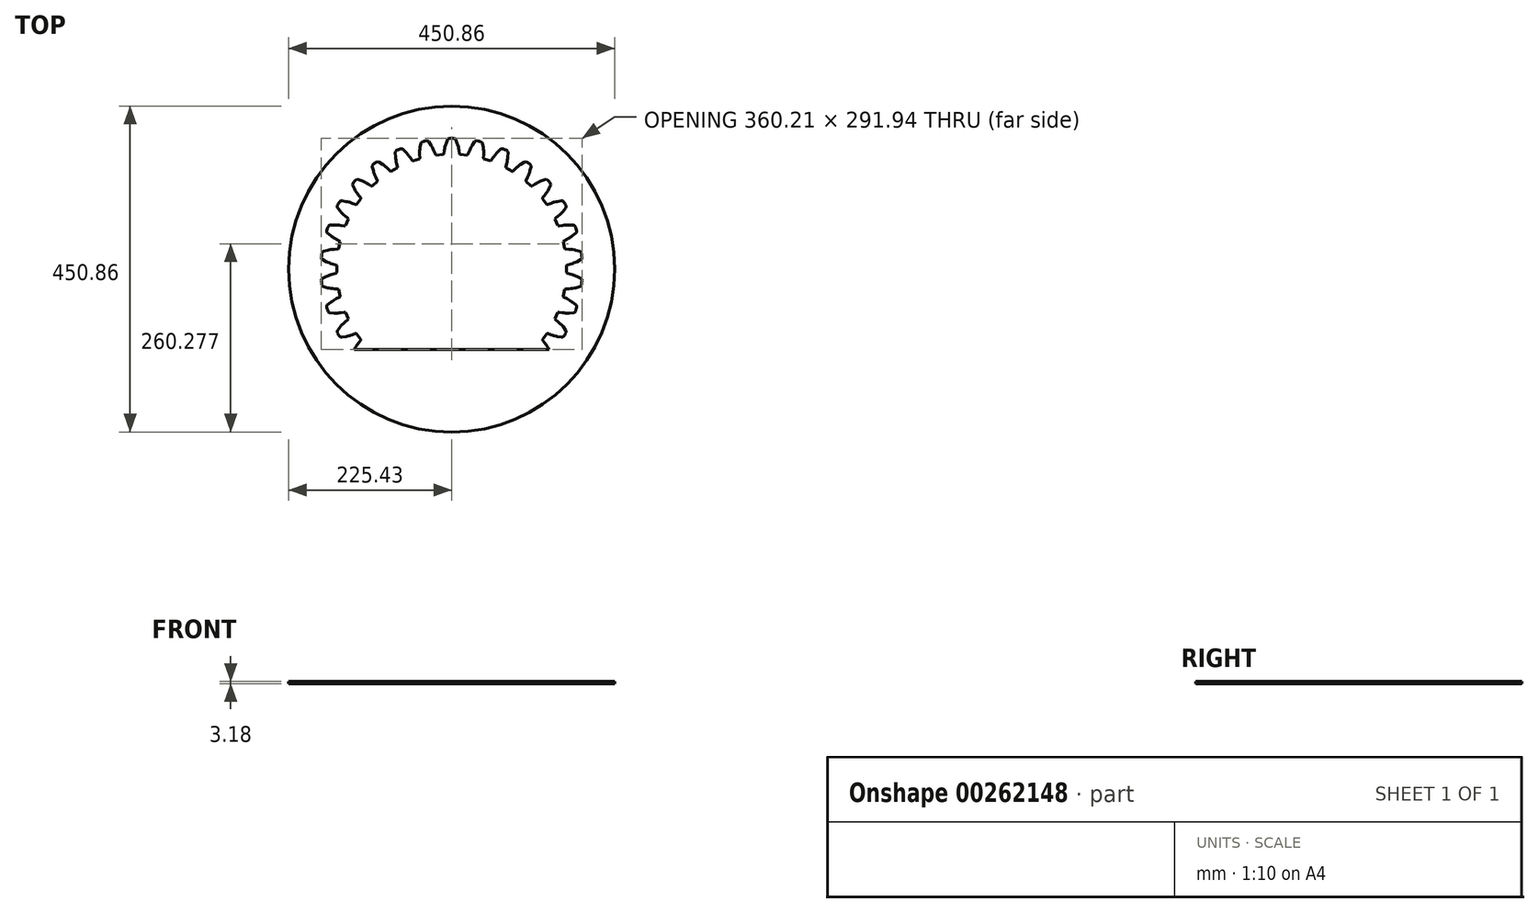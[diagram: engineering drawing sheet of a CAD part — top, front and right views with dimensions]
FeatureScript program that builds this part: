
annotation { "Feature Type Name" : "Feature", "Feature Type Description" : "" }
export const myFeature = defineFeature(function(context is Context, id is Id, definition is map)
    precondition{}
    {
        {
            var Q0;
            Q0=qCreatedBy(makeId("Top.planeOp"),FACE);
            var sketch = newSketch(context, id + "F0", { "sketchPlane" : qUnion([Q0])});
            skLineSegment(sketch, "E0", {"start": v(226.67, 0) * mm, "end": v(221.71, 47.13) * mm});
            skLineSegment(sketch, "E1", {"start": v(221.71, 47.13) * mm, "end": v(207.07, 92.2) * mm});
            skLineSegment(sketch, "E2", {"start": v(207.07, 92.2) * mm, "end": v(183.38, 133.23) * mm});
            skLineSegment(sketch, "E3", {"start": v(183.38, 133.23) * mm, "end": v(151.67, 168.45) * mm});
            skLineSegment(sketch, "E4", {"start": v(151.67, 168.45) * mm, "end": v(113.33, 196.3) * mm});
            skLineSegment(sketch, "E5", {"start": v(113.33, 196.3) * mm, "end": v(70.04, 215.57) * mm});
            skLineSegment(sketch, "E6", {"start": v(70.04, 215.57) * mm, "end": v(23.7, 225.42) * mm});
            skLineSegment(sketch, "E7", {"start": v(23.7, 225.43) * mm, "end": v(-23.7, 225.43) * mm});
            skLineSegment(sketch, "E8", {"start": v(-23.7, 225.43) * mm, "end": v(-70.04, 215.57) * mm});
            skLineSegment(sketch, "E9", {"start": v(-70.04, 215.57) * mm, "end": v(-113.33, 196.3) * mm});
            skLineSegment(sketch, "E10", {"start": v(-113.33, 196.3) * mm, "end": v(-151.67, 168.45) * mm});
            skLineSegment(sketch, "E11", {"start": v(-151.67, 168.45) * mm, "end": v(-183.38, 133.23) * mm});
            skLineSegment(sketch, "E12", {"start": v(-183.38, 133.23) * mm, "end": v(-207.07, 92.2) * mm});
            skLineSegment(sketch, "E13", {"start": v(-207.07, 92.2) * mm, "end": v(-221.71, 47.13) * mm});
            skLineSegment(sketch, "E14", {"start": v(-221.71, 47.13) * mm, "end": v(-226.67, 0) * mm});
            skLineSegment(sketch, "E15", {"start": v(-226.67, 0) * mm, "end": v(-221.71, -47.13) * mm});
            skLineSegment(sketch, "E16", {"start": v(-221.71, -47.13) * mm, "end": v(-207.07, -92.2) * mm});
            skLineSegment(sketch, "E17", {"start": v(-207.07, -92.2) * mm, "end": v(-183.38, -133.23) * mm});
            skLineSegment(sketch, "E18", {"start": v(-183.38, -133.23) * mm, "end": v(-151.67, -168.45) * mm});
            skLineSegment(sketch, "E19", {"start": v(-151.67, -168.45) * mm, "end": v(-113.33, -196.3) * mm});
            skLineSegment(sketch, "E20", {"start": v(-113.33, -196.3) * mm, "end": v(-70.04, -215.57) * mm});
            skLineSegment(sketch, "E21", {"start": v(-70.04, -215.57) * mm, "end": v(-23.7, -225.42) * mm});
            skLineSegment(sketch, "E22", {"start": v(-23.7, -225.43) * mm, "end": v(23.7, -225.43) * mm});
            skLineSegment(sketch, "E23", {"start": v(23.7, -225.43) * mm, "end": v(70.04, -215.57) * mm});
            skLineSegment(sketch, "E24", {"start": v(70.04, -215.57) * mm, "end": v(113.33, -196.3) * mm});
            skLineSegment(sketch, "E25", {"start": v(113.33, -196.3) * mm, "end": v(151.67, -168.45) * mm});
            skLineSegment(sketch, "E26", {"start": v(151.67, -168.45) * mm, "end": v(183.38, -133.23) * mm});
            skLineSegment(sketch, "E27", {"start": v(183.38, -133.23) * mm, "end": v(207.07, -92.2) * mm});
            skLineSegment(sketch, "E28", {"start": v(207.07, -92.2) * mm, "end": v(221.71, -47.13) * mm});
            skLineSegment(sketch, "E29", {"start": v(221.71, -47.13) * mm, "end": v(226.67, 0) * mm});
            skLineSegment(sketch, "E30", {"start": v(-179.94, 17.83) * mm, "end": v(-179.83, 18.9) * mm});
            skLineSegment(sketch, "E31", {"start": v(-179.83, 18.9) * mm, "end": v(-179.72, 19.97) * mm});
            skLineSegment(sketch, "E32", {"start": v(-179.72, 19.97) * mm, "end": v(-179.54, 21.6) * mm});
            skLineSegment(sketch, "E33", {"start": v(-179.54, 21.6) * mm, "end": v(-178.6, 23.6) * mm});
            skLineSegment(sketch, "E34", {"start": v(-178.6, 23.6) * mm, "end": v(-177.2, 24.4) * mm});
            skLineSegment(sketch, "E35", {"start": v(-177.2, 24.4) * mm, "end": v(-171.49, 25.97) * mm});
            skLineSegment(sketch, "E36", {"start": v(-171.49, 25.97) * mm, "end": v(-169.86, 26.35) * mm});
            skLineSegment(sketch, "E37", {"start": v(-169.86, 26.35) * mm, "end": v(-166.94, 26.84) * mm});
            skLineSegment(sketch, "E38", {"start": v(-166.94, 26.84) * mm, "end": v(-166.45, 26.9) * mm});
            skLineSegment(sketch, "E39", {"start": v(-166.45, 26.9) * mm, "end": v(-164.79, 27.1) * mm});
            skLineSegment(sketch, "E40", {"start": v(-164.79, 27.1) * mm, "end": v(-162.13, 27.32) * mm});
            skLineSegment(sketch, "E41", {"start": v(-162.13, 27.32) * mm, "end": v(-157.52, 27.56) * mm});
            skLineSegment(sketch, "E42", {"start": v(-157.52, 27.56) * mm, "end": v(-156.75, 27.92) * mm});
            skLineSegment(sketch, "E43", {"start": v(-156.75, 27.92) * mm, "end": v(-156.27, 28.27) * mm});
            skLineSegment(sketch, "E44", {"start": v(-156.27, 28.27) * mm, "end": v(-154.26, 37.73) * mm});
            skLineSegment(sketch, "E45", {"start": v(-154.26, 37.73) * mm, "end": v(-154.55, 38.25) * mm});
            skLineSegment(sketch, "E46", {"start": v(-154.55, 38.25) * mm, "end": v(-155.1, 38.9) * mm});
            skLineSegment(sketch, "E47", {"start": v(-155.1, 38.9) * mm, "end": v(-159.22, 40.98) * mm});
            skLineSegment(sketch, "E48", {"start": v(-159.22, 40.98) * mm, "end": v(-161.57, 42.26) * mm});
            skLineSegment(sketch, "E49", {"start": v(-161.57, 42.26) * mm, "end": v(-163, 43.12) * mm});
            skLineSegment(sketch, "E50", {"start": v(-163, 43.12) * mm, "end": v(-163.43, 43.38) * mm});
            skLineSegment(sketch, "E51", {"start": v(-163.43, 43.38) * mm, "end": v(-165.9, 45.01) * mm});
            skLineSegment(sketch, "E52", {"start": v(-165.9, 45.01) * mm, "end": v(-167.22, 46.03) * mm});
            skLineSegment(sketch, "E53", {"start": v(-167.22, 46.03) * mm, "end": v(-171.8, 49.77) * mm});
            skLineSegment(sketch, "E54", {"start": v(-171.8, 49.77) * mm, "end": v(-172.76, 51.08) * mm});
            skLineSegment(sketch, "E55", {"start": v(-172.76, 51.08) * mm, "end": v(-172.8, 53.3) * mm});
            skLineSegment(sketch, "E56", {"start": v(-172.8, 53.3) * mm, "end": v(-172.3, 54.85) * mm});
            skLineSegment(sketch, "E57", {"start": v(-172.3, 54.85) * mm, "end": v(-171.97, 55.88) * mm});
            skLineSegment(sketch, "E58", {"start": v(-171.97, 55.88) * mm, "end": v(-171.64, 56.9) * mm});
            skLineSegment(sketch, "E59", {"start": v(-171.64, 56.9) * mm, "end": v(-171.12, 58.45) * mm});
            skLineSegment(sketch, "E60", {"start": v(-171.12, 58.45) * mm, "end": v(-169.79, 60.22) * mm});
            skLineSegment(sketch, "E61", {"start": v(-169.79, 60.22) * mm, "end": v(-168.24, 60.71) * mm});
            skLineSegment(sketch, "E62", {"start": v(-168.24, 60.71) * mm, "end": v(-162.34, 61.06) * mm});
            skLineSegment(sketch, "E63", {"start": v(-162.34, 61.06) * mm, "end": v(-160.67, 61.1) * mm});
            skLineSegment(sketch, "E64", {"start": v(-160.67, 61.1) * mm, "end": v(-157.71, 60.97) * mm});
            skLineSegment(sketch, "E65", {"start": v(-157.71, 60.97) * mm, "end": v(-157.22, 60.93) * mm});
            skLineSegment(sketch, "E66", {"start": v(-157.22, 60.93) * mm, "end": v(-155.55, 60.78) * mm});
            skLineSegment(sketch, "E67", {"start": v(-155.55, 60.78) * mm, "end": v(-152.9, 60.43) * mm});
            skLineSegment(sketch, "E68", {"start": v(-152.9, 60.43) * mm, "end": v(-148.35, 59.7) * mm});
            skLineSegment(sketch, "E69", {"start": v(-148.35, 59.7) * mm, "end": v(-147.52, 59.9) * mm});
            skLineSegment(sketch, "E70", {"start": v(-147.52, 59.9) * mm, "end": v(-146.98, 60.14) * mm});
            skLineSegment(sketch, "E71", {"start": v(-146.98, 60.14) * mm, "end": v(-143.04, 68.98) * mm});
            skLineSegment(sketch, "E72", {"start": v(-143.04, 68.98) * mm, "end": v(-143.22, 69.54) * mm});
            skLineSegment(sketch, "E73", {"start": v(-143.22, 69.54) * mm, "end": v(-143.63, 70.3) * mm});
            skLineSegment(sketch, "E74", {"start": v(-143.63, 70.3) * mm, "end": v(-147.22, 73.19) * mm});
            skLineSegment(sketch, "E75", {"start": v(-147.22, 73.19) * mm, "end": v(-149.25, 74.93) * mm});
            skLineSegment(sketch, "E76", {"start": v(-149.25, 74.93) * mm, "end": v(-150.48, 76.07) * mm});
            skLineSegment(sketch, "E77", {"start": v(-150.48, 76.07) * mm, "end": v(-150.84, 76.4) * mm});
            skLineSegment(sketch, "E78", {"start": v(-150.84, 76.4) * mm, "end": v(-152.91, 78.52) * mm});
            skLineSegment(sketch, "E79", {"start": v(-152.91, 78.52) * mm, "end": v(-154, 79.79) * mm});
            skLineSegment(sketch, "E80", {"start": v(-154, 79.79) * mm, "end": v(-157.7, 84.4) * mm});
            skLineSegment(sketch, "E81", {"start": v(-157.7, 84.4) * mm, "end": v(-158.36, 85.89) * mm});
            skLineSegment(sketch, "E82", {"start": v(-158.36, 85.89) * mm, "end": v(-157.94, 88.06) * mm});
            skLineSegment(sketch, "E83", {"start": v(-157.94, 88.06) * mm, "end": v(-157.13, 89.47) * mm});
            skLineSegment(sketch, "E84", {"start": v(-157.13, 89.47) * mm, "end": v(-156.6, 90.4) * mm});
            skLineSegment(sketch, "E85", {"start": v(-156.6, 90.4) * mm, "end": v(-156.05, 91.34) * mm});
            skLineSegment(sketch, "E86", {"start": v(-156.05, 91.34) * mm, "end": v(-155.23, 92.75) * mm});
            skLineSegment(sketch, "E87", {"start": v(-155.23, 92.75) * mm, "end": v(-153.56, 94.2) * mm});
            skLineSegment(sketch, "E88", {"start": v(-153.56, 94.2) * mm, "end": v(-151.94, 94.37) * mm});
            skLineSegment(sketch, "E89", {"start": v(-151.94, 94.37) * mm, "end": v(-146.1, 93.48) * mm});
            skLineSegment(sketch, "E90", {"start": v(-146.1, 93.48) * mm, "end": v(-144.46, 93.17) * mm});
            skLineSegment(sketch, "E91", {"start": v(-144.46, 93.17) * mm, "end": v(-141.6, 92.43) * mm});
            skLineSegment(sketch, "E92", {"start": v(-141.6, 92.43) * mm, "end": v(-141.11, 92.28) * mm});
            skLineSegment(sketch, "E93", {"start": v(-141.11, 92.28) * mm, "end": v(-139.51, 91.8) * mm});
            skLineSegment(sketch, "E94", {"start": v(-139.51, 91.8) * mm, "end": v(-137, 90.9) * mm});
            skLineSegment(sketch, "E95", {"start": v(-137, 90.9) * mm, "end": v(-132.7, 89.24) * mm});
            skLineSegment(sketch, "E96", {"start": v(-132.7, 89.24) * mm, "end": v(-131.84, 89.26) * mm});
            skLineSegment(sketch, "E97", {"start": v(-131.84, 89.26) * mm, "end": v(-131.26, 89.39) * mm});
            skLineSegment(sketch, "E98", {"start": v(-131.26, 89.39) * mm, "end": v(-125.58, 97.21) * mm});
            skLineSegment(sketch, "E99", {"start": v(-125.58, 97.21) * mm, "end": v(-125.63, 97.8) * mm});
            skLineSegment(sketch, "E100", {"start": v(-125.63, 97.8) * mm, "end": v(-125.88, 98.62) * mm});
            skLineSegment(sketch, "E101", {"start": v(-125.88, 98.62) * mm, "end": v(-128.79, 102.2) * mm});
            skLineSegment(sketch, "E102", {"start": v(-128.79, 102.2) * mm, "end": v(-130.4, 104.32) * mm});
            skLineSegment(sketch, "E103", {"start": v(-130.4, 104.32) * mm, "end": v(-131.37, 105.69) * mm});
            skLineSegment(sketch, "E104", {"start": v(-131.37, 105.69) * mm, "end": v(-131.66, 106.1) * mm});
            skLineSegment(sketch, "E105", {"start": v(-131.66, 106.1) * mm, "end": v(-133.25, 108.6) * mm});
            skLineSegment(sketch, "E106", {"start": v(-133.25, 108.6) * mm, "end": v(-134.05, 110.06) * mm});
            skLineSegment(sketch, "E107", {"start": v(-134.05, 110.06) * mm, "end": v(-136.7, 115.35) * mm});
            skLineSegment(sketch, "E108", {"start": v(-136.7, 115.35) * mm, "end": v(-137.04, 116.93) * mm});
            skLineSegment(sketch, "E109", {"start": v(-137.04, 116.93) * mm, "end": v(-136.18, 118.97) * mm});
            skLineSegment(sketch, "E110", {"start": v(-136.18, 118.97) * mm, "end": v(-135.1, 120.19) * mm});
            skLineSegment(sketch, "E111", {"start": v(-135.1, 120.19) * mm, "end": v(-134.37, 120.99) * mm});
            skLineSegment(sketch, "E112", {"start": v(-134.37, 120.99) * mm, "end": v(-133.65, 121.8) * mm});
            skLineSegment(sketch, "E113", {"start": v(-133.65, 121.8) * mm, "end": v(-132.55, 123) * mm});
            skLineSegment(sketch, "E114", {"start": v(-132.55, 123) * mm, "end": v(-130.62, 124.07) * mm});
            skLineSegment(sketch, "E115", {"start": v(-130.62, 124.07) * mm, "end": v(-129, 123.9) * mm});
            skLineSegment(sketch, "E116", {"start": v(-129, 123.9) * mm, "end": v(-123.47, 121.8) * mm});
            skLineSegment(sketch, "E117", {"start": v(-123.47, 121.8) * mm, "end": v(-121.93, 121.16) * mm});
            skLineSegment(sketch, "E118", {"start": v(-121.93, 121.16) * mm, "end": v(-119.28, 119.84) * mm});
            skLineSegment(sketch, "E119", {"start": v(-119.28, 119.84) * mm, "end": v(-118.84, 119.6) * mm});
            skLineSegment(sketch, "E120", {"start": v(-118.84, 119.6) * mm, "end": v(-117.38, 118.8) * mm});
            skLineSegment(sketch, "E121", {"start": v(-117.38, 118.8) * mm, "end": v(-115.1, 117.4) * mm});
            skLineSegment(sketch, "E122", {"start": v(-115.1, 117.4) * mm, "end": v(-111.24, 114.88) * mm});
            skLineSegment(sketch, "E123", {"start": v(-111.24, 114.88) * mm, "end": v(-110.4, 114.72) * mm});
            skLineSegment(sketch, "E124", {"start": v(-110.4, 114.72) * mm, "end": v(-109.8, 114.73) * mm});
            skLineSegment(sketch, "E125", {"start": v(-109.8, 114.73) * mm, "end": v(-102.62, 121.2) * mm});
            skLineSegment(sketch, "E126", {"start": v(-102.62, 121.2) * mm, "end": v(-102.55, 121.79) * mm});
            skLineSegment(sketch, "E127", {"start": v(-102.55, 121.79) * mm, "end": v(-102.62, 122.64) * mm});
            skLineSegment(sketch, "E128", {"start": v(-102.62, 122.64) * mm, "end": v(-104.73, 126.74) * mm});
            skLineSegment(sketch, "E129", {"start": v(-104.73, 126.74) * mm, "end": v(-105.87, 129.15) * mm});
            skLineSegment(sketch, "E130", {"start": v(-105.87, 129.15) * mm, "end": v(-106.53, 130.7) * mm});
            skLineSegment(sketch, "E131", {"start": v(-106.53, 130.7) * mm, "end": v(-106.72, 131.16) * mm});
            skLineSegment(sketch, "E132", {"start": v(-106.72, 131.16) * mm, "end": v(-107.76, 133.93) * mm});
            skLineSegment(sketch, "E133", {"start": v(-107.76, 133.93) * mm, "end": v(-108.23, 135.53) * mm});
            skLineSegment(sketch, "E134", {"start": v(-108.23, 135.53) * mm, "end": v(-109.73, 141.25) * mm});
            skLineSegment(sketch, "E135", {"start": v(-109.73, 141.25) * mm, "end": v(-109.74, 142.87) * mm});
            skLineSegment(sketch, "E136", {"start": v(-109.74, 142.87) * mm, "end": v(-108.47, 144.68) * mm});
            skLineSegment(sketch, "E137", {"start": v(-108.47, 144.68) * mm, "end": v(-107.16, 145.65) * mm});
            skLineSegment(sketch, "E138", {"start": v(-107.16, 145.65) * mm, "end": v(-106.28, 146.28) * mm});
            skLineSegment(sketch, "E139", {"start": v(-106.28, 146.28) * mm, "end": v(-105.4, 146.92) * mm});
            skLineSegment(sketch, "E140", {"start": v(-105.4, 146.92) * mm, "end": v(-104.08, 147.87) * mm});
            skLineSegment(sketch, "E141", {"start": v(-104.08, 147.87) * mm, "end": v(-101.97, 148.52) * mm});
            skLineSegment(sketch, "E142", {"start": v(-101.97, 148.52) * mm, "end": v(-100.42, 148) * mm});
            skLineSegment(sketch, "E143", {"start": v(-100.42, 148) * mm, "end": v(-95.45, 144.82) * mm});
            skLineSegment(sketch, "E144", {"start": v(-95.45, 144.82) * mm, "end": v(-94.08, 143.87) * mm});
            skLineSegment(sketch, "E145", {"start": v(-94.08, 143.87) * mm, "end": v(-91.76, 142.03) * mm});
            skLineSegment(sketch, "E146", {"start": v(-91.76, 142.03) * mm, "end": v(-91.38, 141.7) * mm});
            skLineSegment(sketch, "E147", {"start": v(-91.38, 141.7) * mm, "end": v(-90.12, 140.6) * mm});
            skLineSegment(sketch, "E148", {"start": v(-90.12, 140.6) * mm, "end": v(-88.18, 138.77) * mm});
            skLineSegment(sketch, "E149", {"start": v(-88.18, 138.77) * mm, "end": v(-84.92, 135.5) * mm});
            skLineSegment(sketch, "E150", {"start": v(-84.92, 135.5) * mm, "end": v(-84.13, 135.17) * mm});
            skLineSegment(sketch, "E151", {"start": v(-84.13, 135.17) * mm, "end": v(-83.55, 135.05) * mm});
            skLineSegment(sketch, "E152", {"start": v(-83.55, 135.05) * mm, "end": v(-75.18, 139.89) * mm});
            skLineSegment(sketch, "E153", {"start": v(-75.18, 139.89) * mm, "end": v(-75, 140.45) * mm});
            skLineSegment(sketch, "E154", {"start": v(-75, 140.45) * mm, "end": v(-74.88, 141.3) * mm});
            skLineSegment(sketch, "E155", {"start": v(-74.88, 141.3) * mm, "end": v(-76.09, 145.75) * mm});
            skLineSegment(sketch, "E156", {"start": v(-76.09, 145.75) * mm, "end": v(-76.7, 148.34) * mm});
            skLineSegment(sketch, "E157", {"start": v(-76.7, 148.34) * mm, "end": v(-77.03, 149.99) * mm});
            skLineSegment(sketch, "E158", {"start": v(-77.03, 149.99) * mm, "end": v(-77.12, 150.48) * mm});
            skLineSegment(sketch, "E159", {"start": v(-77.12, 150.48) * mm, "end": v(-77.56, 153.4) * mm});
            skLineSegment(sketch, "E160", {"start": v(-77.56, 153.4) * mm, "end": v(-77.7, 155.07) * mm});
            skLineSegment(sketch, "E161", {"start": v(-77.7, 155.07) * mm, "end": v(-77.97, 160.98) * mm});
            skLineSegment(sketch, "E162", {"start": v(-77.97, 160.98) * mm, "end": v(-77.63, 162.57) * mm});
            skLineSegment(sketch, "E163", {"start": v(-77.63, 162.57) * mm, "end": v(-76.02, 164.08) * mm});
            skLineSegment(sketch, "E164", {"start": v(-76.02, 164.08) * mm, "end": v(-74.53, 164.75) * mm});
            skLineSegment(sketch, "E165", {"start": v(-74.53, 164.75) * mm, "end": v(-73.54, 165.18) * mm});
            skLineSegment(sketch, "E166", {"start": v(-73.54, 165.18) * mm, "end": v(-72.56, 165.63) * mm});
            skLineSegment(sketch, "E167", {"start": v(-72.56, 165.63) * mm, "end": v(-71.06, 166.28) * mm});
            skLineSegment(sketch, "E168", {"start": v(-71.06, 166.28) * mm, "end": v(-68.86, 166.47) * mm});
            skLineSegment(sketch, "E169", {"start": v(-68.86, 166.47) * mm, "end": v(-67.46, 165.65) * mm});
            skLineSegment(sketch, "E170", {"start": v(-67.46, 165.65) * mm, "end": v(-63.25, 161.5) * mm});
            skLineSegment(sketch, "E171", {"start": v(-63.25, 161.5) * mm, "end": v(-62.1, 160.28) * mm});
            skLineSegment(sketch, "E172", {"start": v(-62.1, 160.28) * mm, "end": v(-60.22, 158) * mm});
            skLineSegment(sketch, "E173", {"start": v(-60.22, 158) * mm, "end": v(-59.92, 157.6) * mm});
            skLineSegment(sketch, "E174", {"start": v(-59.92, 157.6) * mm, "end": v(-58.92, 156.26) * mm});
            skLineSegment(sketch, "E175", {"start": v(-58.92, 156.26) * mm, "end": v(-57.4, 154.07) * mm});
            skLineSegment(sketch, "E176", {"start": v(-57.4, 154.07) * mm, "end": v(-54.9, 150.2) * mm});
            skLineSegment(sketch, "E177", {"start": v(-54.9, 150.2) * mm, "end": v(-54.2, 149.7) * mm});
            skLineSegment(sketch, "E178", {"start": v(-54.2, 149.7) * mm, "end": v(-53.65, 149.47) * mm});
            skLineSegment(sketch, "E179", {"start": v(-53.65, 149.47) * mm, "end": v(-44.45, 152.46) * mm});
            skLineSegment(sketch, "E180", {"start": v(-44.45, 152.46) * mm, "end": v(-44.15, 152.97) * mm});
            skLineSegment(sketch, "E181", {"start": v(-44.15, 152.97) * mm, "end": v(-43.87, 153.78) * mm});
            skLineSegment(sketch, "E182", {"start": v(-43.87, 153.78) * mm, "end": v(-44.12, 158.38) * mm});
            skLineSegment(sketch, "E183", {"start": v(-44.12, 158.38) * mm, "end": v(-44.19, 161.05) * mm});
            skLineSegment(sketch, "E184", {"start": v(-44.19, 161.05) * mm, "end": v(-44.16, 162.72) * mm});
            skLineSegment(sketch, "E185", {"start": v(-44.16, 162.72) * mm, "end": v(-44.15, 163.22) * mm});
            skLineSegment(sketch, "E186", {"start": v(-44.15, 163.22) * mm, "end": v(-43.97, 166.18) * mm});
            skLineSegment(sketch, "E187", {"start": v(-43.97, 166.18) * mm, "end": v(-43.75, 167.83) * mm});
            skLineSegment(sketch, "E188", {"start": v(-43.75, 167.83) * mm, "end": v(-42.8, 173.67) * mm});
            skLineSegment(sketch, "E189", {"start": v(-42.8, 173.67) * mm, "end": v(-42.14, 175.15) * mm});
            skLineSegment(sketch, "E190", {"start": v(-42.14, 175.15) * mm, "end": v(-40.25, 176.3) * mm});
            skLineSegment(sketch, "E191", {"start": v(-40.25, 176.3) * mm, "end": v(-38.65, 176.64) * mm});
            skLineSegment(sketch, "E192", {"start": v(-38.65, 176.64) * mm, "end": v(-37.6, 176.87) * mm});
            skLineSegment(sketch, "E193", {"start": v(-37.6, 176.87) * mm, "end": v(-36.54, 177.1) * mm});
            skLineSegment(sketch, "E194", {"start": v(-36.54, 177.1) * mm, "end": v(-34.94, 177.42) * mm});
            skLineSegment(sketch, "E195", {"start": v(-34.94, 177.42) * mm, "end": v(-32.75, 177.15) * mm});
            skLineSegment(sketch, "E196", {"start": v(-32.75, 177.15) * mm, "end": v(-31.54, 176.06) * mm});
            skLineSegment(sketch, "E197", {"start": v(-31.54, 176.06) * mm, "end": v(-28.3, 171.12) * mm});
            skLineSegment(sketch, "E198", {"start": v(-28.3, 171.12) * mm, "end": v(-27.43, 169.7) * mm});
            skLineSegment(sketch, "E199", {"start": v(-27.43, 169.7) * mm, "end": v(-26.06, 167.07) * mm});
            skLineSegment(sketch, "E200", {"start": v(-26.06, 167.07) * mm, "end": v(-25.84, 166.62) * mm});
            skLineSegment(sketch, "E201", {"start": v(-25.84, 166.62) * mm, "end": v(-25.14, 165.1) * mm});
            skLineSegment(sketch, "E202", {"start": v(-25.14, 165.1) * mm, "end": v(-24.11, 162.63) * mm});
            skLineSegment(sketch, "E203", {"start": v(-24.11, 162.63) * mm, "end": v(-22.47, 158.33) * mm});
            skLineSegment(sketch, "E204", {"start": v(-22.47, 158.33) * mm, "end": v(-21.88, 157.7) * mm});
            skLineSegment(sketch, "E205", {"start": v(-21.88, 157.7) * mm, "end": v(-21.4, 157.36) * mm});
            skLineSegment(sketch, "E206", {"start": v(-21.4, 157.36) * mm, "end": v(-11.78, 158.37) * mm});
            skLineSegment(sketch, "E207", {"start": v(-11.78, 158.37) * mm, "end": v(-11.38, 158.8) * mm});
            skLineSegment(sketch, "E208", {"start": v(-11.38, 158.8) * mm, "end": v(-10.94, 159.54) * mm});
            skLineSegment(sketch, "E209", {"start": v(-10.94, 159.54) * mm, "end": v(-10.23, 164.1) * mm});
            skLineSegment(sketch, "E210", {"start": v(-10.23, 164.1) * mm, "end": v(-9.74, 166.72) * mm});
            skLineSegment(sketch, "E211", {"start": v(-9.74, 166.72) * mm, "end": v(-9.36, 168.35) * mm});
            skLineSegment(sketch, "E212", {"start": v(-9.36, 168.35) * mm, "end": v(-9.25, 168.84) * mm});
            skLineSegment(sketch, "E213", {"start": v(-9.25, 168.84) * mm, "end": v(-8.45, 171.69) * mm});
            skLineSegment(sketch, "E214", {"start": v(-8.45, 171.69) * mm, "end": v(-7.9, 173.26) * mm});
            skLineSegment(sketch, "E215", {"start": v(-7.9, 173.26) * mm, "end": v(-5.75, 178.77) * mm});
            skLineSegment(sketch, "E216", {"start": v(-5.75, 178.77) * mm, "end": v(-4.8, 180.09) * mm});
            skLineSegment(sketch, "E217", {"start": v(-4.8, 180.09) * mm, "end": v(-2.71, 180.81) * mm});
            skLineSegment(sketch, "E218", {"start": v(-2.71, 180.81) * mm, "end": v(-1.08, 180.82) * mm});
            skLineSegment(sketch, "E219", {"start": v(-1.08, 180.82) * mm, "end": v(0, 180.82) * mm});
            skLineSegment(sketch, "E220", {"start": v(0, 180.82) * mm, "end": v(1.08, 180.82) * mm});
            skLineSegment(sketch, "E221", {"start": v(1.08, 180.82) * mm, "end": v(2.71, 180.81) * mm});
            skLineSegment(sketch, "E222", {"start": v(2.71, 180.81) * mm, "end": v(4.8, 180.09) * mm});
            skLineSegment(sketch, "E223", {"start": v(4.8, 180.09) * mm, "end": v(5.75, 178.77) * mm});
            skLineSegment(sketch, "E224", {"start": v(5.75, 178.77) * mm, "end": v(7.9, 173.26) * mm});
            skLineSegment(sketch, "E225", {"start": v(7.9, 173.26) * mm, "end": v(8.45, 171.69) * mm});
            skLineSegment(sketch, "E226", {"start": v(8.45, 171.69) * mm, "end": v(9.25, 168.84) * mm});
            skLineSegment(sketch, "E227", {"start": v(9.25, 168.84) * mm, "end": v(9.36, 168.35) * mm});
            skLineSegment(sketch, "E228", {"start": v(9.36, 168.35) * mm, "end": v(9.74, 166.72) * mm});
            skLineSegment(sketch, "E229", {"start": v(9.74, 166.72) * mm, "end": v(10.23, 164.1) * mm});
            skLineSegment(sketch, "E230", {"start": v(10.23, 164.1) * mm, "end": v(10.94, 159.54) * mm});
            skLineSegment(sketch, "E231", {"start": v(10.94, 159.54) * mm, "end": v(11.38, 158.8) * mm});
            skLineSegment(sketch, "E232", {"start": v(11.38, 158.8) * mm, "end": v(11.78, 158.37) * mm});
            skLineSegment(sketch, "E233", {"start": v(11.78, 158.37) * mm, "end": v(21.4, 157.36) * mm});
            skLineSegment(sketch, "E234", {"start": v(21.4, 157.36) * mm, "end": v(21.88, 157.7) * mm});
            skLineSegment(sketch, "E235", {"start": v(21.88, 157.7) * mm, "end": v(22.47, 158.33) * mm});
            skLineSegment(sketch, "E236", {"start": v(22.47, 158.33) * mm, "end": v(24.11, 162.63) * mm});
            skLineSegment(sketch, "E237", {"start": v(24.11, 162.63) * mm, "end": v(25.14, 165.1) * mm});
            skLineSegment(sketch, "E238", {"start": v(25.14, 165.1) * mm, "end": v(25.84, 166.62) * mm});
            skLineSegment(sketch, "E239", {"start": v(25.84, 166.62) * mm, "end": v(26.06, 167.07) * mm});
            skLineSegment(sketch, "E240", {"start": v(26.06, 167.07) * mm, "end": v(27.43, 169.7) * mm});
            skLineSegment(sketch, "E241", {"start": v(27.43, 169.7) * mm, "end": v(28.3, 171.12) * mm});
            skLineSegment(sketch, "E242", {"start": v(28.3, 171.12) * mm, "end": v(31.54, 176.06) * mm});
            skLineSegment(sketch, "E243", {"start": v(31.54, 176.06) * mm, "end": v(32.75, 177.15) * mm});
            skLineSegment(sketch, "E244", {"start": v(32.75, 177.15) * mm, "end": v(34.94, 177.42) * mm});
            skLineSegment(sketch, "E245", {"start": v(34.94, 177.42) * mm, "end": v(36.54, 177.1) * mm});
            skLineSegment(sketch, "E246", {"start": v(36.54, 177.1) * mm, "end": v(37.6, 176.87) * mm});
            skLineSegment(sketch, "E247", {"start": v(37.6, 176.87) * mm, "end": v(38.65, 176.64) * mm});
            skLineSegment(sketch, "E248", {"start": v(38.65, 176.64) * mm, "end": v(40.25, 176.3) * mm});
            skLineSegment(sketch, "E249", {"start": v(40.25, 176.3) * mm, "end": v(42.14, 175.15) * mm});
            skLineSegment(sketch, "E250", {"start": v(42.14, 175.15) * mm, "end": v(42.8, 173.67) * mm});
            skLineSegment(sketch, "E251", {"start": v(42.8, 173.67) * mm, "end": v(43.75, 167.83) * mm});
            skLineSegment(sketch, "E252", {"start": v(43.75, 167.83) * mm, "end": v(43.97, 166.18) * mm});
            skLineSegment(sketch, "E253", {"start": v(43.97, 166.18) * mm, "end": v(44.15, 163.22) * mm});
            skLineSegment(sketch, "E254", {"start": v(44.15, 163.22) * mm, "end": v(44.16, 162.72) * mm});
            skLineSegment(sketch, "E255", {"start": v(44.16, 162.72) * mm, "end": v(44.19, 161.05) * mm});
            skLineSegment(sketch, "E256", {"start": v(44.19, 161.05) * mm, "end": v(44.12, 158.38) * mm});
            skLineSegment(sketch, "E257", {"start": v(44.12, 158.38) * mm, "end": v(43.87, 153.78) * mm});
            skLineSegment(sketch, "E258", {"start": v(43.87, 153.78) * mm, "end": v(44.15, 152.97) * mm});
            skLineSegment(sketch, "E259", {"start": v(44.15, 152.97) * mm, "end": v(44.45, 152.46) * mm});
            skLineSegment(sketch, "E260", {"start": v(44.45, 152.46) * mm, "end": v(53.65, 149.47) * mm});
            skLineSegment(sketch, "E261", {"start": v(53.65, 149.47) * mm, "end": v(54.2, 149.7) * mm});
            skLineSegment(sketch, "E262", {"start": v(54.2, 149.7) * mm, "end": v(54.9, 150.2) * mm});
            skLineSegment(sketch, "E263", {"start": v(54.9, 150.2) * mm, "end": v(57.4, 154.07) * mm});
            skLineSegment(sketch, "E264", {"start": v(57.4, 154.07) * mm, "end": v(58.92, 156.26) * mm});
            skLineSegment(sketch, "E265", {"start": v(58.92, 156.26) * mm, "end": v(59.92, 157.6) * mm});
            skLineSegment(sketch, "E266", {"start": v(59.92, 157.6) * mm, "end": v(60.22, 158) * mm});
            skLineSegment(sketch, "E267", {"start": v(60.22, 158) * mm, "end": v(62.1, 160.28) * mm});
            skLineSegment(sketch, "E268", {"start": v(62.1, 160.28) * mm, "end": v(63.25, 161.5) * mm});
            skLineSegment(sketch, "E269", {"start": v(63.25, 161.5) * mm, "end": v(67.46, 165.65) * mm});
            skLineSegment(sketch, "E270", {"start": v(67.46, 165.65) * mm, "end": v(68.86, 166.47) * mm});
            skLineSegment(sketch, "E271", {"start": v(68.86, 166.47) * mm, "end": v(71.06, 166.28) * mm});
            skLineSegment(sketch, "E272", {"start": v(71.06, 166.28) * mm, "end": v(72.56, 165.63) * mm});
            skLineSegment(sketch, "E273", {"start": v(72.56, 165.63) * mm, "end": v(73.54, 165.18) * mm});
            skLineSegment(sketch, "E274", {"start": v(73.54, 165.18) * mm, "end": v(74.53, 164.75) * mm});
            skLineSegment(sketch, "E275", {"start": v(74.53, 164.75) * mm, "end": v(76.02, 164.08) * mm});
            skLineSegment(sketch, "E276", {"start": v(76.02, 164.08) * mm, "end": v(77.63, 162.57) * mm});
            skLineSegment(sketch, "E277", {"start": v(77.63, 162.57) * mm, "end": v(77.97, 160.98) * mm});
            skLineSegment(sketch, "E278", {"start": v(77.97, 160.98) * mm, "end": v(77.7, 155.07) * mm});
            skLineSegment(sketch, "E279", {"start": v(77.7, 155.07) * mm, "end": v(77.56, 153.4) * mm});
            skLineSegment(sketch, "E280", {"start": v(77.56, 153.4) * mm, "end": v(77.12, 150.48) * mm});
            skLineSegment(sketch, "E281", {"start": v(77.12, 150.48) * mm, "end": v(77.03, 149.99) * mm});
            skLineSegment(sketch, "E282", {"start": v(77.03, 149.99) * mm, "end": v(76.7, 148.34) * mm});
            skLineSegment(sketch, "E283", {"start": v(76.7, 148.34) * mm, "end": v(76.09, 145.75) * mm});
            skLineSegment(sketch, "E284", {"start": v(76.09, 145.75) * mm, "end": v(74.88, 141.3) * mm});
            skLineSegment(sketch, "E285", {"start": v(74.88, 141.3) * mm, "end": v(75, 140.45) * mm});
            skLineSegment(sketch, "E286", {"start": v(75, 140.45) * mm, "end": v(75.18, 139.89) * mm});
            skLineSegment(sketch, "E287", {"start": v(75.18, 139.89) * mm, "end": v(83.55, 135.05) * mm});
            skLineSegment(sketch, "E288", {"start": v(83.55, 135.05) * mm, "end": v(84.13, 135.17) * mm});
            skLineSegment(sketch, "E289", {"start": v(84.13, 135.17) * mm, "end": v(84.92, 135.5) * mm});
            skLineSegment(sketch, "E290", {"start": v(84.92, 135.5) * mm, "end": v(88.18, 138.77) * mm});
            skLineSegment(sketch, "E291", {"start": v(88.18, 138.77) * mm, "end": v(90.12, 140.6) * mm});
            skLineSegment(sketch, "E292", {"start": v(90.12, 140.6) * mm, "end": v(91.38, 141.7) * mm});
            skLineSegment(sketch, "E293", {"start": v(91.38, 141.7) * mm, "end": v(91.76, 142.03) * mm});
            skLineSegment(sketch, "E294", {"start": v(91.76, 142.03) * mm, "end": v(94.08, 143.87) * mm});
            skLineSegment(sketch, "E295", {"start": v(94.08, 143.87) * mm, "end": v(95.45, 144.82) * mm});
            skLineSegment(sketch, "E296", {"start": v(95.45, 144.82) * mm, "end": v(100.42, 148) * mm});
            skLineSegment(sketch, "E297", {"start": v(100.42, 148) * mm, "end": v(101.97, 148.52) * mm});
            skLineSegment(sketch, "E298", {"start": v(101.97, 148.52) * mm, "end": v(104.08, 147.87) * mm});
            skLineSegment(sketch, "E299", {"start": v(104.08, 147.87) * mm, "end": v(105.4, 146.92) * mm});
            skLineSegment(sketch, "E300", {"start": v(105.4, 146.92) * mm, "end": v(106.28, 146.28) * mm});
            skLineSegment(sketch, "E301", {"start": v(106.28, 146.28) * mm, "end": v(107.16, 145.65) * mm});
            skLineSegment(sketch, "E302", {"start": v(107.16, 145.65) * mm, "end": v(108.47, 144.68) * mm});
            skLineSegment(sketch, "E303", {"start": v(108.47, 144.68) * mm, "end": v(109.74, 142.87) * mm});
            skLineSegment(sketch, "E304", {"start": v(109.74, 142.87) * mm, "end": v(109.73, 141.25) * mm});
            skLineSegment(sketch, "E305", {"start": v(109.73, 141.25) * mm, "end": v(108.23, 135.53) * mm});
            skLineSegment(sketch, "E306", {"start": v(108.23, 135.53) * mm, "end": v(107.76, 133.93) * mm});
            skLineSegment(sketch, "E307", {"start": v(107.76, 133.93) * mm, "end": v(106.72, 131.16) * mm});
            skLineSegment(sketch, "E308", {"start": v(106.72, 131.16) * mm, "end": v(106.53, 130.7) * mm});
            skLineSegment(sketch, "E309", {"start": v(106.53, 130.7) * mm, "end": v(105.87, 129.15) * mm});
            skLineSegment(sketch, "E310", {"start": v(105.87, 129.15) * mm, "end": v(104.73, 126.74) * mm});
            skLineSegment(sketch, "E311", {"start": v(104.73, 126.74) * mm, "end": v(102.62, 122.64) * mm});
            skLineSegment(sketch, "E312", {"start": v(102.62, 122.64) * mm, "end": v(102.55, 121.79) * mm});
            skLineSegment(sketch, "E313", {"start": v(102.55, 121.79) * mm, "end": v(102.62, 121.2) * mm});
            skLineSegment(sketch, "E314", {"start": v(102.62, 121.2) * mm, "end": v(109.8, 114.73) * mm});
            skLineSegment(sketch, "E315", {"start": v(109.8, 114.73) * mm, "end": v(110.4, 114.72) * mm});
            skLineSegment(sketch, "E316", {"start": v(110.4, 114.72) * mm, "end": v(111.24, 114.88) * mm});
            skLineSegment(sketch, "E317", {"start": v(111.24, 114.88) * mm, "end": v(115.1, 117.4) * mm});
            skLineSegment(sketch, "E318", {"start": v(115.1, 117.4) * mm, "end": v(117.38, 118.8) * mm});
            skLineSegment(sketch, "E319", {"start": v(117.38, 118.8) * mm, "end": v(118.84, 119.6) * mm});
            skLineSegment(sketch, "E320", {"start": v(118.84, 119.6) * mm, "end": v(119.28, 119.84) * mm});
            skLineSegment(sketch, "E321", {"start": v(119.28, 119.84) * mm, "end": v(121.93, 121.16) * mm});
            skLineSegment(sketch, "E322", {"start": v(121.93, 121.16) * mm, "end": v(123.47, 121.8) * mm});
            skLineSegment(sketch, "E323", {"start": v(123.47, 121.8) * mm, "end": v(129, 123.9) * mm});
            skLineSegment(sketch, "E324", {"start": v(129, 123.9) * mm, "end": v(130.62, 124.07) * mm});
            skLineSegment(sketch, "E325", {"start": v(130.62, 124.07) * mm, "end": v(132.55, 123) * mm});
            skLineSegment(sketch, "E326", {"start": v(132.55, 123) * mm, "end": v(133.65, 121.8) * mm});
            skLineSegment(sketch, "E327", {"start": v(133.65, 121.8) * mm, "end": v(134.37, 120.99) * mm});
            skLineSegment(sketch, "E328", {"start": v(134.37, 120.99) * mm, "end": v(135.1, 120.19) * mm});
            skLineSegment(sketch, "E329", {"start": v(135.1, 120.19) * mm, "end": v(136.18, 118.97) * mm});
            skLineSegment(sketch, "E330", {"start": v(136.18, 118.97) * mm, "end": v(137.04, 116.93) * mm});
            skLineSegment(sketch, "E331", {"start": v(137.04, 116.93) * mm, "end": v(136.7, 115.35) * mm});
            skLineSegment(sketch, "E332", {"start": v(136.7, 115.35) * mm, "end": v(134.05, 110.06) * mm});
            skLineSegment(sketch, "E333", {"start": v(134.05, 110.06) * mm, "end": v(133.25, 108.6) * mm});
            skLineSegment(sketch, "E334", {"start": v(133.25, 108.6) * mm, "end": v(131.66, 106.1) * mm});
            skLineSegment(sketch, "E335", {"start": v(131.66, 106.1) * mm, "end": v(131.37, 105.69) * mm});
            skLineSegment(sketch, "E336", {"start": v(131.37, 105.69) * mm, "end": v(130.4, 104.32) * mm});
            skLineSegment(sketch, "E337", {"start": v(130.4, 104.32) * mm, "end": v(128.79, 102.2) * mm});
            skLineSegment(sketch, "E338", {"start": v(128.79, 102.2) * mm, "end": v(125.88, 98.62) * mm});
            skLineSegment(sketch, "E339", {"start": v(125.88, 98.62) * mm, "end": v(125.63, 97.8) * mm});
            skLineSegment(sketch, "E340", {"start": v(125.63, 97.8) * mm, "end": v(125.58, 97.21) * mm});
            skLineSegment(sketch, "E341", {"start": v(125.58, 97.21) * mm, "end": v(131.26, 89.39) * mm});
            skLineSegment(sketch, "E342", {"start": v(131.26, 89.39) * mm, "end": v(131.84, 89.26) * mm});
            skLineSegment(sketch, "E343", {"start": v(131.84, 89.26) * mm, "end": v(132.7, 89.24) * mm});
            skLineSegment(sketch, "E344", {"start": v(132.7, 89.24) * mm, "end": v(137, 90.9) * mm});
            skLineSegment(sketch, "E345", {"start": v(137, 90.9) * mm, "end": v(139.51, 91.8) * mm});
            skLineSegment(sketch, "E346", {"start": v(139.51, 91.8) * mm, "end": v(141.11, 92.28) * mm});
            skLineSegment(sketch, "E347", {"start": v(141.11, 92.28) * mm, "end": v(141.6, 92.43) * mm});
            skLineSegment(sketch, "E348", {"start": v(141.6, 92.43) * mm, "end": v(144.46, 93.17) * mm});
            skLineSegment(sketch, "E349", {"start": v(144.46, 93.17) * mm, "end": v(146.1, 93.48) * mm});
            skLineSegment(sketch, "E350", {"start": v(146.1, 93.48) * mm, "end": v(151.94, 94.37) * mm});
            skLineSegment(sketch, "E351", {"start": v(151.94, 94.37) * mm, "end": v(153.56, 94.2) * mm});
            skLineSegment(sketch, "E352", {"start": v(153.56, 94.2) * mm, "end": v(155.23, 92.75) * mm});
            skLineSegment(sketch, "E353", {"start": v(155.23, 92.75) * mm, "end": v(156.05, 91.34) * mm});
            skLineSegment(sketch, "E354", {"start": v(156.05, 91.34) * mm, "end": v(156.6, 90.4) * mm});
            skLineSegment(sketch, "E355", {"start": v(156.6, 90.4) * mm, "end": v(157.13, 89.47) * mm});
            skLineSegment(sketch, "E356", {"start": v(157.13, 89.47) * mm, "end": v(157.94, 88.06) * mm});
            skLineSegment(sketch, "E357", {"start": v(157.94, 88.06) * mm, "end": v(158.36, 85.89) * mm});
            skLineSegment(sketch, "E358", {"start": v(158.36, 85.89) * mm, "end": v(157.7, 84.4) * mm});
            skLineSegment(sketch, "E359", {"start": v(157.7, 84.4) * mm, "end": v(154, 79.79) * mm});
            skLineSegment(sketch, "E360", {"start": v(154, 79.79) * mm, "end": v(152.91, 78.52) * mm});
            skLineSegment(sketch, "E361", {"start": v(152.91, 78.52) * mm, "end": v(150.84, 76.4) * mm});
            skLineSegment(sketch, "E362", {"start": v(150.84, 76.4) * mm, "end": v(150.48, 76.07) * mm});
            skLineSegment(sketch, "E363", {"start": v(150.48, 76.07) * mm, "end": v(149.25, 74.93) * mm});
            skLineSegment(sketch, "E364", {"start": v(149.25, 74.93) * mm, "end": v(147.22, 73.19) * mm});
            skLineSegment(sketch, "E365", {"start": v(147.22, 73.19) * mm, "end": v(143.63, 70.3) * mm});
            skLineSegment(sketch, "E366", {"start": v(143.63, 70.3) * mm, "end": v(143.22, 69.54) * mm});
            skLineSegment(sketch, "E367", {"start": v(143.22, 69.54) * mm, "end": v(143.04, 68.98) * mm});
            skLineSegment(sketch, "E368", {"start": v(143.04, 68.98) * mm, "end": v(146.98, 60.14) * mm});
            skLineSegment(sketch, "E369", {"start": v(146.98, 60.14) * mm, "end": v(147.52, 59.9) * mm});
            skLineSegment(sketch, "E370", {"start": v(147.52, 59.9) * mm, "end": v(148.35, 59.7) * mm});
            skLineSegment(sketch, "E371", {"start": v(148.35, 59.7) * mm, "end": v(152.9, 60.43) * mm});
            skLineSegment(sketch, "E372", {"start": v(152.9, 60.43) * mm, "end": v(155.55, 60.78) * mm});
            skLineSegment(sketch, "E373", {"start": v(155.55, 60.78) * mm, "end": v(157.22, 60.93) * mm});
            skLineSegment(sketch, "E374", {"start": v(157.22, 60.93) * mm, "end": v(157.71, 60.97) * mm});
            skLineSegment(sketch, "E375", {"start": v(157.71, 60.97) * mm, "end": v(160.67, 61.1) * mm});
            skLineSegment(sketch, "E376", {"start": v(160.67, 61.1) * mm, "end": v(162.34, 61.06) * mm});
            skLineSegment(sketch, "E377", {"start": v(162.34, 61.06) * mm, "end": v(168.24, 60.71) * mm});
            skLineSegment(sketch, "E378", {"start": v(168.24, 60.71) * mm, "end": v(169.79, 60.22) * mm});
            skLineSegment(sketch, "E379", {"start": v(169.79, 60.22) * mm, "end": v(171.12, 58.45) * mm});
            skLineSegment(sketch, "E380", {"start": v(171.12, 58.45) * mm, "end": v(171.64, 56.9) * mm});
            skLineSegment(sketch, "E381", {"start": v(171.64, 56.9) * mm, "end": v(171.97, 55.88) * mm});
            skLineSegment(sketch, "E382", {"start": v(171.97, 55.88) * mm, "end": v(172.3, 54.85) * mm});
            skLineSegment(sketch, "E383", {"start": v(172.3, 54.85) * mm, "end": v(172.8, 53.3) * mm});
            skLineSegment(sketch, "E384", {"start": v(172.8, 53.3) * mm, "end": v(172.76, 51.08) * mm});
            skLineSegment(sketch, "E385", {"start": v(172.76, 51.08) * mm, "end": v(171.8, 49.77) * mm});
            skLineSegment(sketch, "E386", {"start": v(171.8, 49.77) * mm, "end": v(167.22, 46.03) * mm});
            skLineSegment(sketch, "E387", {"start": v(167.22, 46.03) * mm, "end": v(165.9, 45.01) * mm});
            skLineSegment(sketch, "E388", {"start": v(165.9, 45.01) * mm, "end": v(163.43, 43.38) * mm});
            skLineSegment(sketch, "E389", {"start": v(163.43, 43.38) * mm, "end": v(163, 43.12) * mm});
            skLineSegment(sketch, "E390", {"start": v(163, 43.12) * mm, "end": v(161.57, 42.26) * mm});
            skLineSegment(sketch, "E391", {"start": v(161.57, 42.26) * mm, "end": v(159.22, 40.98) * mm});
            skLineSegment(sketch, "E392", {"start": v(159.22, 40.98) * mm, "end": v(155.1, 38.9) * mm});
            skLineSegment(sketch, "E393", {"start": v(155.1, 38.9) * mm, "end": v(154.55, 38.25) * mm});
            skLineSegment(sketch, "E394", {"start": v(154.55, 38.25) * mm, "end": v(154.26, 37.73) * mm});
            skLineSegment(sketch, "E395", {"start": v(154.26, 37.73) * mm, "end": v(156.27, 28.27) * mm});
            skLineSegment(sketch, "E396", {"start": v(156.27, 28.27) * mm, "end": v(156.75, 27.92) * mm});
            skLineSegment(sketch, "E397", {"start": v(156.75, 27.92) * mm, "end": v(157.52, 27.56) * mm});
            skLineSegment(sketch, "E398", {"start": v(157.52, 27.56) * mm, "end": v(162.13, 27.32) * mm});
            skLineSegment(sketch, "E399", {"start": v(162.13, 27.32) * mm, "end": v(164.79, 27.1) * mm});
            skLineSegment(sketch, "E400", {"start": v(164.79, 27.1) * mm, "end": v(166.45, 26.9) * mm});
            skLineSegment(sketch, "E401", {"start": v(166.45, 26.9) * mm, "end": v(166.94, 26.84) * mm});
            skLineSegment(sketch, "E402", {"start": v(166.94, 26.84) * mm, "end": v(169.86, 26.35) * mm});
            skLineSegment(sketch, "E403", {"start": v(169.86, 26.35) * mm, "end": v(171.49, 25.97) * mm});
            skLineSegment(sketch, "E404", {"start": v(171.49, 25.97) * mm, "end": v(177.2, 24.4) * mm});
            skLineSegment(sketch, "E405", {"start": v(177.2, 24.4) * mm, "end": v(178.6, 23.6) * mm});
            skLineSegment(sketch, "E406", {"start": v(178.6, 23.6) * mm, "end": v(179.54, 21.6) * mm});
            skLineSegment(sketch, "E407", {"start": v(179.54, 21.6) * mm, "end": v(179.72, 19.97) * mm});
            skLineSegment(sketch, "E408", {"start": v(179.72, 19.97) * mm, "end": v(179.83, 18.9) * mm});
            skLineSegment(sketch, "E409", {"start": v(179.83, 18.9) * mm, "end": v(179.94, 17.83) * mm});
            skLineSegment(sketch, "E410", {"start": v(179.94, 17.83) * mm, "end": v(180.1, 16.2) * mm});
            skLineSegment(sketch, "E411", {"start": v(180.1, 16.2) * mm, "end": v(179.6, 14.05) * mm});
            skLineSegment(sketch, "E412", {"start": v(179.6, 14.05) * mm, "end": v(178.4, 12.97) * mm});
            skLineSegment(sketch, "E413", {"start": v(178.4, 12.97) * mm, "end": v(173.14, 10.25) * mm});
            skLineSegment(sketch, "E414", {"start": v(173.14, 10.25) * mm, "end": v(171.63, 9.54) * mm});
            skLineSegment(sketch, "E415", {"start": v(171.63, 9.54) * mm, "end": v(168.88, 8.45) * mm});
            skLineSegment(sketch, "E416", {"start": v(168.88, 8.45) * mm, "end": v(168.4, 8.29) * mm});
            skLineSegment(sketch, "E417", {"start": v(168.4, 8.29) * mm, "end": v(166.82, 7.74) * mm});
            skLineSegment(sketch, "E418", {"start": v(166.82, 7.74) * mm, "end": v(164.26, 6.98) * mm});
            skLineSegment(sketch, "E419", {"start": v(164.26, 6.98) * mm, "end": v(159.8, 5.8) * mm});
            skLineSegment(sketch, "E420", {"start": v(159.8, 5.8) * mm, "end": v(159.13, 5.28) * mm});
            skLineSegment(sketch, "E421", {"start": v(159.13, 5.28) * mm, "end": v(158.73, 4.84) * mm});
            skLineSegment(sketch, "E422", {"start": v(158.73, 4.84) * mm, "end": v(158.73, -4.84) * mm});
            skLineSegment(sketch, "E423", {"start": v(158.73, -4.84) * mm, "end": v(159.13, -5.28) * mm});
            skLineSegment(sketch, "E424", {"start": v(159.13, -5.28) * mm, "end": v(159.8, -5.8) * mm});
            skLineSegment(sketch, "E425", {"start": v(159.8, -5.8) * mm, "end": v(164.26, -6.98) * mm});
            skLineSegment(sketch, "E426", {"start": v(164.26, -6.98) * mm, "end": v(166.82, -7.74) * mm});
            skLineSegment(sketch, "E427", {"start": v(166.82, -7.74) * mm, "end": v(168.4, -8.29) * mm});
            skLineSegment(sketch, "E428", {"start": v(168.4, -8.29) * mm, "end": v(168.88, -8.45) * mm});
            skLineSegment(sketch, "E429", {"start": v(168.88, -8.45) * mm, "end": v(171.63, -9.54) * mm});
            skLineSegment(sketch, "E430", {"start": v(171.63, -9.54) * mm, "end": v(173.14, -10.25) * mm});
            skLineSegment(sketch, "E431", {"start": v(173.14, -10.25) * mm, "end": v(178.4, -12.97) * mm});
            skLineSegment(sketch, "E432", {"start": v(178.4, -12.97) * mm, "end": v(179.6, -14.05) * mm});
            skLineSegment(sketch, "E433", {"start": v(179.6, -14.05) * mm, "end": v(180.1, -16.2) * mm});
            skLineSegment(sketch, "E434", {"start": v(180.1, -16.2) * mm, "end": v(179.94, -17.83) * mm});
            skLineSegment(sketch, "E435", {"start": v(179.94, -17.83) * mm, "end": v(179.83, -18.9) * mm});
            skLineSegment(sketch, "E436", {"start": v(179.83, -18.9) * mm, "end": v(179.72, -19.97) * mm});
            skLineSegment(sketch, "E437", {"start": v(179.72, -19.97) * mm, "end": v(179.54, -21.6) * mm});
            skLineSegment(sketch, "E438", {"start": v(179.54, -21.6) * mm, "end": v(178.6, -23.6) * mm});
            skLineSegment(sketch, "E439", {"start": v(178.6, -23.6) * mm, "end": v(177.2, -24.4) * mm});
            skLineSegment(sketch, "E440", {"start": v(177.2, -24.4) * mm, "end": v(171.49, -25.97) * mm});
            skLineSegment(sketch, "E441", {"start": v(171.49, -25.97) * mm, "end": v(169.86, -26.35) * mm});
            skLineSegment(sketch, "E442", {"start": v(169.86, -26.35) * mm, "end": v(166.94, -26.84) * mm});
            skLineSegment(sketch, "E443", {"start": v(166.94, -26.84) * mm, "end": v(166.45, -26.9) * mm});
            skLineSegment(sketch, "E444", {"start": v(166.45, -26.9) * mm, "end": v(164.79, -27.1) * mm});
            skLineSegment(sketch, "E445", {"start": v(164.79, -27.1) * mm, "end": v(162.13, -27.32) * mm});
            skLineSegment(sketch, "E446", {"start": v(162.13, -27.32) * mm, "end": v(157.52, -27.56) * mm});
            skLineSegment(sketch, "E447", {"start": v(157.52, -27.56) * mm, "end": v(156.75, -27.92) * mm});
            skLineSegment(sketch, "E448", {"start": v(156.75, -27.92) * mm, "end": v(156.27, -28.27) * mm});
            skLineSegment(sketch, "E449", {"start": v(156.27, -28.27) * mm, "end": v(154.26, -37.73) * mm});
            skLineSegment(sketch, "E450", {"start": v(154.26, -37.73) * mm, "end": v(154.55, -38.25) * mm});
            skLineSegment(sketch, "E451", {"start": v(154.55, -38.25) * mm, "end": v(155.1, -38.9) * mm});
            skLineSegment(sketch, "E452", {"start": v(155.1, -38.9) * mm, "end": v(159.22, -40.98) * mm});
            skLineSegment(sketch, "E453", {"start": v(159.22, -40.98) * mm, "end": v(161.57, -42.26) * mm});
            skLineSegment(sketch, "E454", {"start": v(161.57, -42.26) * mm, "end": v(163, -43.12) * mm});
            skLineSegment(sketch, "E455", {"start": v(163, -43.12) * mm, "end": v(163.43, -43.38) * mm});
            skLineSegment(sketch, "E456", {"start": v(163.43, -43.38) * mm, "end": v(165.9, -45.01) * mm});
            skLineSegment(sketch, "E457", {"start": v(165.9, -45.01) * mm, "end": v(167.22, -46.03) * mm});
            skLineSegment(sketch, "E458", {"start": v(167.22, -46.03) * mm, "end": v(171.8, -49.77) * mm});
            skLineSegment(sketch, "E459", {"start": v(171.8, -49.77) * mm, "end": v(172.76, -51.08) * mm});
            skLineSegment(sketch, "E460", {"start": v(172.76, -51.08) * mm, "end": v(172.8, -53.3) * mm});
            skLineSegment(sketch, "E461", {"start": v(172.8, -53.3) * mm, "end": v(172.3, -54.85) * mm});
            skLineSegment(sketch, "E462", {"start": v(172.3, -54.85) * mm, "end": v(171.97, -55.88) * mm});
            skLineSegment(sketch, "E463", {"start": v(171.97, -55.88) * mm, "end": v(171.64, -56.9) * mm});
            skLineSegment(sketch, "E464", {"start": v(171.64, -56.9) * mm, "end": v(171.12, -58.45) * mm});
            skLineSegment(sketch, "E465", {"start": v(171.12, -58.45) * mm, "end": v(169.79, -60.22) * mm});
            skLineSegment(sketch, "E466", {"start": v(169.79, -60.22) * mm, "end": v(168.24, -60.71) * mm});
            skLineSegment(sketch, "E467", {"start": v(168.24, -60.71) * mm, "end": v(162.34, -61.06) * mm});
            skLineSegment(sketch, "E468", {"start": v(162.34, -61.06) * mm, "end": v(160.67, -61.1) * mm});
            skLineSegment(sketch, "E469", {"start": v(160.67, -61.1) * mm, "end": v(157.71, -60.97) * mm});
            skLineSegment(sketch, "E470", {"start": v(157.71, -60.97) * mm, "end": v(157.22, -60.93) * mm});
            skLineSegment(sketch, "E471", {"start": v(157.22, -60.93) * mm, "end": v(155.55, -60.78) * mm});
            skLineSegment(sketch, "E472", {"start": v(155.55, -60.78) * mm, "end": v(152.9, -60.43) * mm});
            skLineSegment(sketch, "E473", {"start": v(152.9, -60.43) * mm, "end": v(148.35, -59.7) * mm});
            skLineSegment(sketch, "E474", {"start": v(148.35, -59.7) * mm, "end": v(147.52, -59.9) * mm});
            skLineSegment(sketch, "E475", {"start": v(147.52, -59.9) * mm, "end": v(146.98, -60.14) * mm});
            skLineSegment(sketch, "E476", {"start": v(146.98, -60.14) * mm, "end": v(143.04, -68.98) * mm});
            skLineSegment(sketch, "E477", {"start": v(143.04, -68.98) * mm, "end": v(143.22, -69.54) * mm});
            skLineSegment(sketch, "E478", {"start": v(143.22, -69.54) * mm, "end": v(143.63, -70.3) * mm});
            skLineSegment(sketch, "E479", {"start": v(143.63, -70.3) * mm, "end": v(147.22, -73.19) * mm});
            skLineSegment(sketch, "E480", {"start": v(147.22, -73.19) * mm, "end": v(149.25, -74.93) * mm});
            skLineSegment(sketch, "E481", {"start": v(149.25, -74.93) * mm, "end": v(150.48, -76.07) * mm});
            skLineSegment(sketch, "E482", {"start": v(150.48, -76.07) * mm, "end": v(150.84, -76.4) * mm});
            skLineSegment(sketch, "E483", {"start": v(150.84, -76.4) * mm, "end": v(152.91, -78.52) * mm});
            skLineSegment(sketch, "E484", {"start": v(152.91, -78.52) * mm, "end": v(154, -79.79) * mm});
            skLineSegment(sketch, "E485", {"start": v(154, -79.79) * mm, "end": v(157.7, -84.4) * mm});
            skLineSegment(sketch, "E486", {"start": v(157.7, -84.4) * mm, "end": v(158.36, -85.89) * mm});
            skLineSegment(sketch, "E487", {"start": v(158.36, -85.89) * mm, "end": v(157.94, -88.06) * mm});
            skLineSegment(sketch, "E488", {"start": v(157.94, -88.06) * mm, "end": v(157.13, -89.47) * mm});
            skLineSegment(sketch, "E489", {"start": v(157.13, -89.47) * mm, "end": v(156.6, -90.4) * mm});
            skLineSegment(sketch, "E490", {"start": v(156.6, -90.4) * mm, "end": v(156.05, -91.34) * mm});
            skLineSegment(sketch, "E491", {"start": v(156.05, -91.34) * mm, "end": v(155.23, -92.75) * mm});
            skLineSegment(sketch, "E492", {"start": v(155.23, -92.75) * mm, "end": v(153.56, -94.2) * mm});
            skLineSegment(sketch, "E493", {"start": v(153.56, -94.2) * mm, "end": v(151.94, -94.37) * mm});
            skLineSegment(sketch, "E494", {"start": v(151.94, -94.37) * mm, "end": v(146.1, -93.48) * mm});
            skLineSegment(sketch, "E495", {"start": v(146.1, -93.48) * mm, "end": v(144.46, -93.17) * mm});
            skLineSegment(sketch, "E496", {"start": v(144.46, -93.17) * mm, "end": v(141.6, -92.43) * mm});
            skLineSegment(sketch, "E497", {"start": v(141.6, -92.43) * mm, "end": v(141.11, -92.28) * mm});
            skLineSegment(sketch, "E498", {"start": v(141.11, -92.28) * mm, "end": v(139.51, -91.8) * mm});
            skLineSegment(sketch, "E499", {"start": v(139.51, -91.8) * mm, "end": v(137, -90.9) * mm});
            skLineSegment(sketch, "E500", {"start": v(137, -90.9) * mm, "end": v(132.7, -89.24) * mm});
            skLineSegment(sketch, "E501", {"start": v(132.7, -89.24) * mm, "end": v(131.84, -89.26) * mm});
            skLineSegment(sketch, "E502", {"start": v(131.84, -89.26) * mm, "end": v(131.26, -89.39) * mm});
            skLineSegment(sketch, "E503", {"start": v(131.26, -89.39) * mm, "end": v(125.58, -97.21) * mm});
            skLineSegment(sketch, "E504", {"start": v(125.58, -97.21) * mm, "end": v(125.63, -97.8) * mm});
            skLineSegment(sketch, "E505", {"start": v(125.63, -97.8) * mm, "end": v(125.88, -98.62) * mm});
            skLineSegment(sketch, "E506", {"start": v(125.88, -98.62) * mm, "end": v(128.79, -102.2) * mm});
            skLineSegment(sketch, "E507", {"start": v(128.79, -102.2) * mm, "end": v(130.4, -104.32) * mm});
            skLineSegment(sketch, "E508", {"start": v(130.4, -104.32) * mm, "end": v(131.37, -105.69) * mm});
            skLineSegment(sketch, "E509", {"start": v(131.37, -105.69) * mm, "end": v(131.66, -106.1) * mm});
            skLineSegment(sketch, "E510", {"start": v(131.66, -106.1) * mm, "end": v(133.25, -108.6) * mm});
            skLineSegment(sketch, "E511", {"start": v(133.25, -108.6) * mm, "end": v(134.05, -110.06) * mm});
            skLineSegment(sketch, "E512", {"start": v(134.05, -110.06) * mm, "end": v(136.7, -115.35) * mm});
            skLineSegment(sketch, "E513", {"start": v(136.7, -115.35) * mm, "end": v(137.04, -116.93) * mm});
            skLineSegment(sketch, "E514", {"start": v(137.04, -116.93) * mm, "end": v(136.18, -118.97) * mm});
            skLineSegment(sketch, "E515", {"start": v(136.18, -118.97) * mm, "end": v(135.1, -120.19) * mm});
            skLineSegment(sketch, "E516", {"start": v(135.1, -120.19) * mm, "end": v(134.37, -120.99) * mm});
            skLineSegment(sketch, "E517", {"start": v(134.37, -120.99) * mm, "end": v(133.65, -121.8) * mm});
            skLineSegment(sketch, "E518", {"start": v(133.65, -121.8) * mm, "end": v(132.55, -123) * mm});
            skLineSegment(sketch, "E519", {"start": v(132.55, -123) * mm, "end": v(130.62, -124.07) * mm});
            skLineSegment(sketch, "E520", {"start": v(130.62, -124.07) * mm, "end": v(129, -123.9) * mm});
            skLineSegment(sketch, "E521", {"start": v(129, -123.9) * mm, "end": v(123.47, -121.8) * mm});
            skLineSegment(sketch, "E522", {"start": v(123.47, -121.8) * mm, "end": v(121.93, -121.16) * mm});
            skLineSegment(sketch, "E523", {"start": v(121.93, -121.16) * mm, "end": v(119.28, -119.84) * mm});
            skLineSegment(sketch, "E524", {"start": v(119.28, -119.84) * mm, "end": v(118.84, -119.6) * mm});
            skLineSegment(sketch, "E525", {"start": v(118.84, -119.6) * mm, "end": v(117.38, -118.8) * mm});
            skLineSegment(sketch, "E526", {"start": v(117.38, -118.8) * mm, "end": v(115.1, -117.4) * mm});
            skLineSegment(sketch, "E527", {"start": v(115.1, -117.4) * mm, "end": v(111.24, -114.88) * mm});
            skLineSegment(sketch, "E528", {"start": v(111.24, -114.88) * mm, "end": v(110.4, -114.72) * mm});
            skLineSegment(sketch, "E529", {"start": v(110.4, -114.72) * mm, "end": v(109.8, -114.73) * mm});
            skLineSegment(sketch, "E530", {"start": v(109.8, -114.73) * mm, "end": v(102.62, -121.2) * mm});
            skLineSegment(sketch, "E531", {"start": v(102.62, -121.2) * mm, "end": v(102.55, -121.79) * mm});
            skLineSegment(sketch, "E532", {"start": v(102.55, -121.79) * mm, "end": v(102.62, -122.64) * mm});
            skLineSegment(sketch, "E533", {"start": v(102.62, -122.64) * mm, "end": v(104.73, -126.74) * mm});
            skLineSegment(sketch, "E534", {"start": v(104.73, -126.74) * mm, "end": v(105.87, -129.15) * mm});
            skLineSegment(sketch, "E535", {"start": v(105.87, -129.15) * mm, "end": v(106.53, -130.7) * mm});
            skLineSegment(sketch, "E536", {"start": v(106.53, -130.7) * mm, "end": v(106.72, -131.16) * mm});
            skLineSegment(sketch, "E537", {"start": v(106.72, -131.16) * mm, "end": v(107.76, -133.93) * mm});
            skLineSegment(sketch, "E538", {"start": v(107.76, -133.93) * mm, "end": v(108.23, -135.53) * mm});
            skLineSegment(sketch, "E539", {"start": v(108.23, -135.53) * mm, "end": v(109.73, -141.25) * mm});
            skLineSegment(sketch, "E540", {"start": v(109.73, -141.25) * mm, "end": v(109.74, -142.87) * mm});
            skLineSegment(sketch, "E541", {"start": v(109.74, -142.87) * mm, "end": v(108.47, -144.68) * mm});
            skLineSegment(sketch, "E542", {"start": v(108.47, -144.68) * mm, "end": v(107.16, -145.65) * mm});
            skLineSegment(sketch, "E543", {"start": v(107.16, -145.65) * mm, "end": v(106.28, -146.28) * mm});
            skLineSegment(sketch, "E544", {"start": v(106.28, -146.28) * mm, "end": v(105.4, -146.92) * mm});
            skLineSegment(sketch, "E545", {"start": v(105.4, -146.92) * mm, "end": v(104.08, -147.87) * mm});
            skLineSegment(sketch, "E546", {"start": v(104.08, -147.87) * mm, "end": v(101.97, -148.52) * mm});
            skLineSegment(sketch, "E547", {"start": v(101.97, -148.52) * mm, "end": v(100.42, -148) * mm});
            skLineSegment(sketch, "E548", {"start": v(100.42, -148) * mm, "end": v(95.45, -144.82) * mm});
            skLineSegment(sketch, "E549", {"start": v(95.45, -144.82) * mm, "end": v(94.08, -143.87) * mm});
            skLineSegment(sketch, "E550", {"start": v(94.08, -143.87) * mm, "end": v(91.76, -142.03) * mm});
            skLineSegment(sketch, "E551", {"start": v(91.76, -142.03) * mm, "end": v(91.38, -141.7) * mm});
            skLineSegment(sketch, "E552", {"start": v(91.38, -141.7) * mm, "end": v(90.12, -140.6) * mm});
            skLineSegment(sketch, "E553", {"start": v(90.12, -140.6) * mm, "end": v(88.18, -138.77) * mm});
            skLineSegment(sketch, "E554", {"start": v(88.18, -138.77) * mm, "end": v(84.92, -135.5) * mm});
            skLineSegment(sketch, "E555", {"start": v(84.92, -135.5) * mm, "end": v(84.13, -135.17) * mm});
            skLineSegment(sketch, "E556", {"start": v(84.13, -135.17) * mm, "end": v(83.55, -135.05) * mm});
            skLineSegment(sketch, "E557", {"start": v(83.55, -135.05) * mm, "end": v(75.18, -139.89) * mm});
            skLineSegment(sketch, "E558", {"start": v(75.18, -139.89) * mm, "end": v(75, -140.45) * mm});
            skLineSegment(sketch, "E559", {"start": v(75, -140.45) * mm, "end": v(74.88, -141.3) * mm});
            skLineSegment(sketch, "E560", {"start": v(74.88, -141.3) * mm, "end": v(76.09, -145.75) * mm});
            skLineSegment(sketch, "E561", {"start": v(76.09, -145.75) * mm, "end": v(76.7, -148.34) * mm});
            skLineSegment(sketch, "E562", {"start": v(76.7, -148.34) * mm, "end": v(77.03, -149.99) * mm});
            skLineSegment(sketch, "E563", {"start": v(77.03, -149.99) * mm, "end": v(77.12, -150.48) * mm});
            skLineSegment(sketch, "E564", {"start": v(77.12, -150.48) * mm, "end": v(77.56, -153.4) * mm});
            skLineSegment(sketch, "E565", {"start": v(77.56, -153.4) * mm, "end": v(77.7, -155.07) * mm});
            skLineSegment(sketch, "E566", {"start": v(77.7, -155.07) * mm, "end": v(77.97, -160.98) * mm});
            skLineSegment(sketch, "E567", {"start": v(77.97, -160.98) * mm, "end": v(77.63, -162.57) * mm});
            skLineSegment(sketch, "E568", {"start": v(77.63, -162.57) * mm, "end": v(76.02, -164.08) * mm});
            skLineSegment(sketch, "E569", {"start": v(76.02, -164.08) * mm, "end": v(74.53, -164.75) * mm});
            skLineSegment(sketch, "E570", {"start": v(74.53, -164.75) * mm, "end": v(73.54, -165.18) * mm});
            skLineSegment(sketch, "E571", {"start": v(73.54, -165.18) * mm, "end": v(72.56, -165.63) * mm});
            skLineSegment(sketch, "E572", {"start": v(72.56, -165.63) * mm, "end": v(71.06, -166.28) * mm});
            skLineSegment(sketch, "E573", {"start": v(71.06, -166.28) * mm, "end": v(68.86, -166.47) * mm});
            skLineSegment(sketch, "E574", {"start": v(68.86, -166.47) * mm, "end": v(67.46, -165.65) * mm});
            skLineSegment(sketch, "E575", {"start": v(67.46, -165.65) * mm, "end": v(63.25, -161.5) * mm});
            skLineSegment(sketch, "E576", {"start": v(63.25, -161.5) * mm, "end": v(62.1, -160.28) * mm});
            skLineSegment(sketch, "E577", {"start": v(62.1, -160.28) * mm, "end": v(60.22, -158) * mm});
            skLineSegment(sketch, "E578", {"start": v(60.22, -158) * mm, "end": v(59.92, -157.6) * mm});
            skLineSegment(sketch, "E579", {"start": v(59.92, -157.6) * mm, "end": v(58.92, -156.26) * mm});
            skLineSegment(sketch, "E580", {"start": v(58.92, -156.26) * mm, "end": v(57.4, -154.07) * mm});
            skLineSegment(sketch, "E581", {"start": v(57.4, -154.07) * mm, "end": v(54.9, -150.2) * mm});
            skLineSegment(sketch, "E582", {"start": v(54.9, -150.2) * mm, "end": v(54.2, -149.7) * mm});
            skLineSegment(sketch, "E583", {"start": v(54.2, -149.7) * mm, "end": v(53.65, -149.47) * mm});
            skLineSegment(sketch, "E584", {"start": v(53.65, -149.47) * mm, "end": v(44.45, -152.46) * mm});
            skLineSegment(sketch, "E585", {"start": v(44.45, -152.46) * mm, "end": v(44.15, -152.97) * mm});
            skLineSegment(sketch, "E586", {"start": v(44.15, -152.97) * mm, "end": v(43.87, -153.78) * mm});
            skLineSegment(sketch, "E587", {"start": v(43.87, -153.78) * mm, "end": v(44.12, -158.38) * mm});
            skLineSegment(sketch, "E588", {"start": v(44.12, -158.38) * mm, "end": v(44.19, -161.05) * mm});
            skLineSegment(sketch, "E589", {"start": v(44.19, -161.05) * mm, "end": v(44.16, -162.72) * mm});
            skLineSegment(sketch, "E590", {"start": v(44.16, -162.72) * mm, "end": v(44.15, -163.22) * mm});
            skLineSegment(sketch, "E591", {"start": v(44.15, -163.22) * mm, "end": v(43.97, -166.18) * mm});
            skLineSegment(sketch, "E592", {"start": v(43.97, -166.18) * mm, "end": v(43.75, -167.83) * mm});
            skLineSegment(sketch, "E593", {"start": v(43.75, -167.83) * mm, "end": v(42.8, -173.67) * mm});
            skLineSegment(sketch, "E594", {"start": v(42.8, -173.67) * mm, "end": v(42.14, -175.15) * mm});
            skLineSegment(sketch, "E595", {"start": v(42.14, -175.15) * mm, "end": v(40.25, -176.3) * mm});
            skLineSegment(sketch, "E596", {"start": v(40.25, -176.3) * mm, "end": v(38.65, -176.64) * mm});
            skLineSegment(sketch, "E597", {"start": v(38.65, -176.64) * mm, "end": v(37.6, -176.87) * mm});
            skLineSegment(sketch, "E598", {"start": v(37.6, -176.87) * mm, "end": v(36.54, -177.1) * mm});
            skLineSegment(sketch, "E599", {"start": v(36.54, -177.1) * mm, "end": v(34.94, -177.42) * mm});
            skLineSegment(sketch, "E600", {"start": v(34.94, -177.42) * mm, "end": v(32.75, -177.15) * mm});
            skLineSegment(sketch, "E601", {"start": v(32.75, -177.15) * mm, "end": v(31.54, -176.06) * mm});
            skLineSegment(sketch, "E602", {"start": v(31.54, -176.06) * mm, "end": v(28.3, -171.12) * mm});
            skLineSegment(sketch, "E603", {"start": v(28.3, -171.12) * mm, "end": v(27.43, -169.7) * mm});
            skLineSegment(sketch, "E604", {"start": v(27.43, -169.7) * mm, "end": v(26.06, -167.07) * mm});
            skLineSegment(sketch, "E605", {"start": v(26.06, -167.07) * mm, "end": v(25.84, -166.62) * mm});
            skLineSegment(sketch, "E606", {"start": v(25.84, -166.62) * mm, "end": v(25.14, -165.1) * mm});
            skLineSegment(sketch, "E607", {"start": v(25.14, -165.1) * mm, "end": v(24.11, -162.63) * mm});
            skLineSegment(sketch, "E608", {"start": v(24.11, -162.63) * mm, "end": v(22.47, -158.33) * mm});
            skLineSegment(sketch, "E609", {"start": v(22.47, -158.33) * mm, "end": v(21.88, -157.7) * mm});
            skLineSegment(sketch, "E610", {"start": v(21.88, -157.7) * mm, "end": v(21.4, -157.36) * mm});
            skLineSegment(sketch, "E611", {"start": v(21.4, -157.36) * mm, "end": v(11.78, -158.37) * mm});
            skLineSegment(sketch, "E612", {"start": v(11.78, -158.37) * mm, "end": v(11.38, -158.8) * mm});
            skLineSegment(sketch, "E613", {"start": v(11.38, -158.8) * mm, "end": v(10.94, -159.54) * mm});
            skLineSegment(sketch, "E614", {"start": v(10.94, -159.54) * mm, "end": v(10.23, -164.1) * mm});
            skLineSegment(sketch, "E615", {"start": v(10.23, -164.1) * mm, "end": v(9.74, -166.72) * mm});
            skLineSegment(sketch, "E616", {"start": v(9.74, -166.72) * mm, "end": v(9.36, -168.35) * mm});
            skLineSegment(sketch, "E617", {"start": v(9.36, -168.35) * mm, "end": v(9.25, -168.84) * mm});
            skLineSegment(sketch, "E618", {"start": v(9.25, -168.84) * mm, "end": v(8.45, -171.69) * mm});
            skLineSegment(sketch, "E619", {"start": v(8.45, -171.69) * mm, "end": v(7.9, -173.26) * mm});
            skLineSegment(sketch, "E620", {"start": v(7.9, -173.26) * mm, "end": v(5.75, -178.77) * mm});
            skLineSegment(sketch, "E621", {"start": v(5.75, -178.77) * mm, "end": v(4.8, -180.09) * mm});
            skLineSegment(sketch, "E622", {"start": v(4.8, -180.09) * mm, "end": v(2.71, -180.81) * mm});
            skLineSegment(sketch, "E623", {"start": v(2.71, -180.81) * mm, "end": v(1.08, -180.82) * mm});
            skLineSegment(sketch, "E624", {"start": v(1.08, -180.82) * mm, "end": v(0, -180.82) * mm});
            skLineSegment(sketch, "E625", {"start": v(0, -180.82) * mm, "end": v(-1.08, -180.82) * mm});
            skLineSegment(sketch, "E626", {"start": v(-1.08, -180.82) * mm, "end": v(-2.71, -180.81) * mm});
            skLineSegment(sketch, "E627", {"start": v(-2.71, -180.81) * mm, "end": v(-4.8, -180.09) * mm});
            skLineSegment(sketch, "E628", {"start": v(-4.8, -180.09) * mm, "end": v(-5.75, -178.77) * mm});
            skLineSegment(sketch, "E629", {"start": v(-5.75, -178.77) * mm, "end": v(-7.9, -173.26) * mm});
            skLineSegment(sketch, "E630", {"start": v(-7.9, -173.26) * mm, "end": v(-8.45, -171.69) * mm});
            skLineSegment(sketch, "E631", {"start": v(-8.45, -171.69) * mm, "end": v(-9.25, -168.84) * mm});
            skLineSegment(sketch, "E632", {"start": v(-9.25, -168.84) * mm, "end": v(-9.36, -168.35) * mm});
            skLineSegment(sketch, "E633", {"start": v(-9.36, -168.35) * mm, "end": v(-9.74, -166.72) * mm});
            skLineSegment(sketch, "E634", {"start": v(-9.74, -166.72) * mm, "end": v(-10.23, -164.1) * mm});
            skLineSegment(sketch, "E635", {"start": v(-10.23, -164.1) * mm, "end": v(-10.94, -159.54) * mm});
            skLineSegment(sketch, "E636", {"start": v(-10.94, -159.54) * mm, "end": v(-11.38, -158.8) * mm});
            skLineSegment(sketch, "E637", {"start": v(-11.38, -158.8) * mm, "end": v(-11.78, -158.37) * mm});
            skLineSegment(sketch, "E638", {"start": v(-11.78, -158.37) * mm, "end": v(-21.4, -157.36) * mm});
            skLineSegment(sketch, "E639", {"start": v(-21.4, -157.36) * mm, "end": v(-21.88, -157.7) * mm});
            skLineSegment(sketch, "E640", {"start": v(-21.88, -157.7) * mm, "end": v(-22.47, -158.33) * mm});
            skLineSegment(sketch, "E641", {"start": v(-22.47, -158.33) * mm, "end": v(-24.11, -162.63) * mm});
            skLineSegment(sketch, "E642", {"start": v(-24.11, -162.63) * mm, "end": v(-25.14, -165.1) * mm});
            skLineSegment(sketch, "E643", {"start": v(-25.14, -165.1) * mm, "end": v(-25.84, -166.62) * mm});
            skLineSegment(sketch, "E644", {"start": v(-25.84, -166.62) * mm, "end": v(-26.06, -167.07) * mm});
            skLineSegment(sketch, "E645", {"start": v(-26.06, -167.07) * mm, "end": v(-27.43, -169.7) * mm});
            skLineSegment(sketch, "E646", {"start": v(-27.43, -169.7) * mm, "end": v(-28.3, -171.12) * mm});
            skLineSegment(sketch, "E647", {"start": v(-28.3, -171.12) * mm, "end": v(-31.54, -176.06) * mm});
            skLineSegment(sketch, "E648", {"start": v(-31.54, -176.06) * mm, "end": v(-32.75, -177.15) * mm});
            skLineSegment(sketch, "E649", {"start": v(-32.75, -177.15) * mm, "end": v(-34.94, -177.42) * mm});
            skLineSegment(sketch, "E650", {"start": v(-34.94, -177.42) * mm, "end": v(-36.54, -177.1) * mm});
            skLineSegment(sketch, "E651", {"start": v(-36.54, -177.1) * mm, "end": v(-37.6, -176.87) * mm});
            skLineSegment(sketch, "E652", {"start": v(-37.6, -176.87) * mm, "end": v(-38.65, -176.64) * mm});
            skLineSegment(sketch, "E653", {"start": v(-38.65, -176.64) * mm, "end": v(-40.25, -176.3) * mm});
            skLineSegment(sketch, "E654", {"start": v(-40.25, -176.3) * mm, "end": v(-42.14, -175.15) * mm});
            skLineSegment(sketch, "E655", {"start": v(-42.14, -175.15) * mm, "end": v(-42.8, -173.67) * mm});
            skLineSegment(sketch, "E656", {"start": v(-42.8, -173.67) * mm, "end": v(-43.75, -167.83) * mm});
            skLineSegment(sketch, "E657", {"start": v(-43.75, -167.83) * mm, "end": v(-43.97, -166.18) * mm});
            skLineSegment(sketch, "E658", {"start": v(-43.97, -166.18) * mm, "end": v(-44.15, -163.22) * mm});
            skLineSegment(sketch, "E659", {"start": v(-44.15, -163.22) * mm, "end": v(-44.16, -162.72) * mm});
            skLineSegment(sketch, "E660", {"start": v(-44.16, -162.72) * mm, "end": v(-44.19, -161.05) * mm});
            skLineSegment(sketch, "E661", {"start": v(-44.19, -161.05) * mm, "end": v(-44.12, -158.38) * mm});
            skLineSegment(sketch, "E662", {"start": v(-44.12, -158.38) * mm, "end": v(-43.87, -153.78) * mm});
            skLineSegment(sketch, "E663", {"start": v(-43.87, -153.78) * mm, "end": v(-44.15, -152.97) * mm});
            skLineSegment(sketch, "E664", {"start": v(-44.15, -152.97) * mm, "end": v(-44.45, -152.46) * mm});
            skLineSegment(sketch, "E665", {"start": v(-44.45, -152.46) * mm, "end": v(-53.65, -149.47) * mm});
            skLineSegment(sketch, "E666", {"start": v(-53.65, -149.47) * mm, "end": v(-54.2, -149.7) * mm});
            skLineSegment(sketch, "E667", {"start": v(-54.2, -149.7) * mm, "end": v(-54.9, -150.2) * mm});
            skLineSegment(sketch, "E668", {"start": v(-54.9, -150.2) * mm, "end": v(-57.4, -154.07) * mm});
            skLineSegment(sketch, "E669", {"start": v(-57.4, -154.07) * mm, "end": v(-58.92, -156.26) * mm});
            skLineSegment(sketch, "E670", {"start": v(-58.92, -156.26) * mm, "end": v(-59.92, -157.6) * mm});
            skLineSegment(sketch, "E671", {"start": v(-59.92, -157.6) * mm, "end": v(-60.22, -158) * mm});
            skLineSegment(sketch, "E672", {"start": v(-60.22, -158) * mm, "end": v(-62.1, -160.28) * mm});
            skLineSegment(sketch, "E673", {"start": v(-62.1, -160.28) * mm, "end": v(-63.25, -161.5) * mm});
            skLineSegment(sketch, "E674", {"start": v(-63.25, -161.5) * mm, "end": v(-67.46, -165.65) * mm});
            skLineSegment(sketch, "E675", {"start": v(-67.46, -165.65) * mm, "end": v(-68.86, -166.47) * mm});
            skLineSegment(sketch, "E676", {"start": v(-68.86, -166.47) * mm, "end": v(-71.06, -166.28) * mm});
            skLineSegment(sketch, "E677", {"start": v(-71.06, -166.28) * mm, "end": v(-72.56, -165.63) * mm});
            skLineSegment(sketch, "E678", {"start": v(-72.56, -165.63) * mm, "end": v(-73.54, -165.18) * mm});
            skLineSegment(sketch, "E679", {"start": v(-73.54, -165.18) * mm, "end": v(-74.53, -164.75) * mm});
            skLineSegment(sketch, "E680", {"start": v(-74.53, -164.75) * mm, "end": v(-76.02, -164.08) * mm});
            skLineSegment(sketch, "E681", {"start": v(-76.02, -164.08) * mm, "end": v(-77.63, -162.57) * mm});
            skLineSegment(sketch, "E682", {"start": v(-77.63, -162.57) * mm, "end": v(-77.97, -160.98) * mm});
            skLineSegment(sketch, "E683", {"start": v(-77.97, -160.98) * mm, "end": v(-77.7, -155.07) * mm});
            skLineSegment(sketch, "E684", {"start": v(-77.7, -155.07) * mm, "end": v(-77.56, -153.4) * mm});
            skLineSegment(sketch, "E685", {"start": v(-77.56, -153.4) * mm, "end": v(-77.12, -150.48) * mm});
            skLineSegment(sketch, "E686", {"start": v(-77.12, -150.48) * mm, "end": v(-77.03, -149.99) * mm});
            skLineSegment(sketch, "E687", {"start": v(-77.03, -149.99) * mm, "end": v(-76.7, -148.34) * mm});
            skLineSegment(sketch, "E688", {"start": v(-76.7, -148.34) * mm, "end": v(-76.09, -145.75) * mm});
            skLineSegment(sketch, "E689", {"start": v(-76.09, -145.75) * mm, "end": v(-74.88, -141.3) * mm});
            skLineSegment(sketch, "E690", {"start": v(-74.88, -141.3) * mm, "end": v(-75, -140.45) * mm});
            skLineSegment(sketch, "E691", {"start": v(-75, -140.45) * mm, "end": v(-75.18, -139.89) * mm});
            skLineSegment(sketch, "E692", {"start": v(-75.18, -139.89) * mm, "end": v(-83.55, -135.05) * mm});
            skLineSegment(sketch, "E693", {"start": v(-83.55, -135.05) * mm, "end": v(-84.13, -135.17) * mm});
            skLineSegment(sketch, "E694", {"start": v(-84.13, -135.17) * mm, "end": v(-84.92, -135.5) * mm});
            skLineSegment(sketch, "E695", {"start": v(-84.92, -135.5) * mm, "end": v(-88.18, -138.77) * mm});
            skLineSegment(sketch, "E696", {"start": v(-88.18, -138.77) * mm, "end": v(-90.12, -140.6) * mm});
            skLineSegment(sketch, "E697", {"start": v(-90.12, -140.6) * mm, "end": v(-91.38, -141.7) * mm});
            skLineSegment(sketch, "E698", {"start": v(-91.38, -141.7) * mm, "end": v(-91.76, -142.03) * mm});
            skLineSegment(sketch, "E699", {"start": v(-91.76, -142.03) * mm, "end": v(-94.08, -143.87) * mm});
            skLineSegment(sketch, "E700", {"start": v(-94.08, -143.87) * mm, "end": v(-95.45, -144.82) * mm});
            skLineSegment(sketch, "E701", {"start": v(-95.45, -144.82) * mm, "end": v(-100.42, -148) * mm});
            skLineSegment(sketch, "E702", {"start": v(-100.42, -148) * mm, "end": v(-101.97, -148.52) * mm});
            skLineSegment(sketch, "E703", {"start": v(-101.97, -148.52) * mm, "end": v(-104.08, -147.87) * mm});
            skLineSegment(sketch, "E704", {"start": v(-104.08, -147.87) * mm, "end": v(-105.4, -146.92) * mm});
            skLineSegment(sketch, "E705", {"start": v(-105.4, -146.92) * mm, "end": v(-106.28, -146.28) * mm});
            skLineSegment(sketch, "E706", {"start": v(-106.28, -146.28) * mm, "end": v(-107.16, -145.65) * mm});
            skLineSegment(sketch, "E707", {"start": v(-107.16, -145.65) * mm, "end": v(-108.47, -144.68) * mm});
            skLineSegment(sketch, "E708", {"start": v(-108.47, -144.68) * mm, "end": v(-109.74, -142.87) * mm});
            skLineSegment(sketch, "E709", {"start": v(-109.74, -142.87) * mm, "end": v(-109.73, -141.25) * mm});
            skLineSegment(sketch, "E710", {"start": v(-109.73, -141.25) * mm, "end": v(-108.23, -135.53) * mm});
            skLineSegment(sketch, "E711", {"start": v(-108.23, -135.53) * mm, "end": v(-107.76, -133.93) * mm});
            skLineSegment(sketch, "E712", {"start": v(-107.76, -133.93) * mm, "end": v(-106.72, -131.16) * mm});
            skLineSegment(sketch, "E713", {"start": v(-106.72, -131.16) * mm, "end": v(-106.53, -130.7) * mm});
            skLineSegment(sketch, "E714", {"start": v(-106.53, -130.7) * mm, "end": v(-105.87, -129.15) * mm});
            skLineSegment(sketch, "E715", {"start": v(-105.87, -129.15) * mm, "end": v(-104.73, -126.74) * mm});
            skLineSegment(sketch, "E716", {"start": v(-104.73, -126.74) * mm, "end": v(-102.62, -122.64) * mm});
            skLineSegment(sketch, "E717", {"start": v(-102.62, -122.64) * mm, "end": v(-102.55, -121.79) * mm});
            skLineSegment(sketch, "E718", {"start": v(-102.55, -121.79) * mm, "end": v(-102.62, -121.2) * mm});
            skLineSegment(sketch, "E719", {"start": v(-102.62, -121.2) * mm, "end": v(-109.8, -114.73) * mm});
            skLineSegment(sketch, "E720", {"start": v(-109.8, -114.73) * mm, "end": v(-110.4, -114.72) * mm});
            skLineSegment(sketch, "E721", {"start": v(-110.4, -114.72) * mm, "end": v(-111.24, -114.88) * mm});
            skLineSegment(sketch, "E722", {"start": v(-111.24, -114.88) * mm, "end": v(-115.1, -117.4) * mm});
            skLineSegment(sketch, "E723", {"start": v(-115.1, -117.4) * mm, "end": v(-117.38, -118.8) * mm});
            skLineSegment(sketch, "E724", {"start": v(-117.38, -118.8) * mm, "end": v(-118.84, -119.6) * mm});
            skLineSegment(sketch, "E725", {"start": v(-118.84, -119.6) * mm, "end": v(-119.28, -119.84) * mm});
            skLineSegment(sketch, "E726", {"start": v(-119.28, -119.84) * mm, "end": v(-121.93, -121.16) * mm});
            skLineSegment(sketch, "E727", {"start": v(-121.93, -121.16) * mm, "end": v(-123.47, -121.8) * mm});
            skLineSegment(sketch, "E728", {"start": v(-123.47, -121.8) * mm, "end": v(-129, -123.9) * mm});
            skLineSegment(sketch, "E729", {"start": v(-129, -123.9) * mm, "end": v(-130.62, -124.07) * mm});
            skLineSegment(sketch, "E730", {"start": v(-130.62, -124.07) * mm, "end": v(-132.55, -123) * mm});
            skLineSegment(sketch, "E731", {"start": v(-132.55, -123) * mm, "end": v(-133.65, -121.8) * mm});
            skLineSegment(sketch, "E732", {"start": v(-133.65, -121.8) * mm, "end": v(-134.37, -120.99) * mm});
            skLineSegment(sketch, "E733", {"start": v(-134.37, -120.99) * mm, "end": v(-135.1, -120.19) * mm});
            skLineSegment(sketch, "E734", {"start": v(-135.1, -120.19) * mm, "end": v(-136.18, -118.97) * mm});
            skLineSegment(sketch, "E735", {"start": v(-136.18, -118.97) * mm, "end": v(-137.04, -116.93) * mm});
            skLineSegment(sketch, "E736", {"start": v(-137.04, -116.93) * mm, "end": v(-136.7, -115.35) * mm});
            skLineSegment(sketch, "E737", {"start": v(-136.7, -115.35) * mm, "end": v(-134.05, -110.06) * mm});
            skLineSegment(sketch, "E738", {"start": v(-134.05, -110.06) * mm, "end": v(-133.25, -108.6) * mm});
            skLineSegment(sketch, "E739", {"start": v(-133.25, -108.6) * mm, "end": v(-131.66, -106.1) * mm});
            skLineSegment(sketch, "E740", {"start": v(-131.66, -106.1) * mm, "end": v(-131.37, -105.69) * mm});
            skLineSegment(sketch, "E741", {"start": v(-131.37, -105.69) * mm, "end": v(-130.4, -104.32) * mm});
            skLineSegment(sketch, "E742", {"start": v(-130.4, -104.32) * mm, "end": v(-128.79, -102.2) * mm});
            skLineSegment(sketch, "E743", {"start": v(-128.79, -102.2) * mm, "end": v(-125.88, -98.62) * mm});
            skLineSegment(sketch, "E744", {"start": v(-125.88, -98.62) * mm, "end": v(-125.63, -97.8) * mm});
            skLineSegment(sketch, "E745", {"start": v(-125.63, -97.8) * mm, "end": v(-125.58, -97.21) * mm});
            skLineSegment(sketch, "E746", {"start": v(-125.58, -97.21) * mm, "end": v(-131.26, -89.39) * mm});
            skLineSegment(sketch, "E747", {"start": v(-131.26, -89.39) * mm, "end": v(-131.84, -89.26) * mm});
            skLineSegment(sketch, "E748", {"start": v(-131.84, -89.26) * mm, "end": v(-132.7, -89.24) * mm});
            skLineSegment(sketch, "E749", {"start": v(-132.7, -89.24) * mm, "end": v(-137, -90.9) * mm});
            skLineSegment(sketch, "E750", {"start": v(-137, -90.9) * mm, "end": v(-139.51, -91.8) * mm});
            skLineSegment(sketch, "E751", {"start": v(-139.51, -91.8) * mm, "end": v(-141.11, -92.28) * mm});
            skLineSegment(sketch, "E752", {"start": v(-141.11, -92.28) * mm, "end": v(-141.6, -92.43) * mm});
            skLineSegment(sketch, "E753", {"start": v(-141.6, -92.43) * mm, "end": v(-144.46, -93.17) * mm});
            skLineSegment(sketch, "E754", {"start": v(-144.46, -93.17) * mm, "end": v(-146.1, -93.48) * mm});
            skLineSegment(sketch, "E755", {"start": v(-146.1, -93.48) * mm, "end": v(-151.94, -94.37) * mm});
            skLineSegment(sketch, "E756", {"start": v(-151.94, -94.37) * mm, "end": v(-153.56, -94.2) * mm});
            skLineSegment(sketch, "E757", {"start": v(-153.56, -94.2) * mm, "end": v(-155.23, -92.75) * mm});
            skLineSegment(sketch, "E758", {"start": v(-155.23, -92.75) * mm, "end": v(-156.05, -91.34) * mm});
            skLineSegment(sketch, "E759", {"start": v(-156.05, -91.34) * mm, "end": v(-156.6, -90.4) * mm});
            skLineSegment(sketch, "E760", {"start": v(-156.6, -90.4) * mm, "end": v(-157.13, -89.47) * mm});
            skLineSegment(sketch, "E761", {"start": v(-157.13, -89.47) * mm, "end": v(-157.94, -88.06) * mm});
            skLineSegment(sketch, "E762", {"start": v(-157.94, -88.06) * mm, "end": v(-158.36, -85.89) * mm});
            skLineSegment(sketch, "E763", {"start": v(-158.36, -85.89) * mm, "end": v(-157.7, -84.4) * mm});
            skLineSegment(sketch, "E764", {"start": v(-157.7, -84.4) * mm, "end": v(-154, -79.79) * mm});
            skLineSegment(sketch, "E765", {"start": v(-154, -79.79) * mm, "end": v(-152.91, -78.52) * mm});
            skLineSegment(sketch, "E766", {"start": v(-152.91, -78.52) * mm, "end": v(-150.84, -76.4) * mm});
            skLineSegment(sketch, "E767", {"start": v(-150.84, -76.4) * mm, "end": v(-150.48, -76.07) * mm});
            skLineSegment(sketch, "E768", {"start": v(-150.48, -76.07) * mm, "end": v(-149.25, -74.93) * mm});
            skLineSegment(sketch, "E769", {"start": v(-149.25, -74.93) * mm, "end": v(-147.22, -73.19) * mm});
            skLineSegment(sketch, "E770", {"start": v(-147.22, -73.19) * mm, "end": v(-143.63, -70.3) * mm});
            skLineSegment(sketch, "E771", {"start": v(-143.63, -70.3) * mm, "end": v(-143.22, -69.54) * mm});
            skLineSegment(sketch, "E772", {"start": v(-143.22, -69.54) * mm, "end": v(-143.04, -68.98) * mm});
            skLineSegment(sketch, "E773", {"start": v(-143.04, -68.98) * mm, "end": v(-146.98, -60.14) * mm});
            skLineSegment(sketch, "E774", {"start": v(-146.98, -60.14) * mm, "end": v(-147.52, -59.9) * mm});
            skLineSegment(sketch, "E775", {"start": v(-147.52, -59.9) * mm, "end": v(-148.35, -59.7) * mm});
            skLineSegment(sketch, "E776", {"start": v(-148.35, -59.7) * mm, "end": v(-152.9, -60.43) * mm});
            skLineSegment(sketch, "E777", {"start": v(-152.9, -60.43) * mm, "end": v(-155.55, -60.78) * mm});
            skLineSegment(sketch, "E778", {"start": v(-155.55, -60.78) * mm, "end": v(-157.22, -60.93) * mm});
            skLineSegment(sketch, "E779", {"start": v(-157.22, -60.93) * mm, "end": v(-157.71, -60.97) * mm});
            skLineSegment(sketch, "E780", {"start": v(-157.71, -60.97) * mm, "end": v(-160.67, -61.1) * mm});
            skLineSegment(sketch, "E781", {"start": v(-160.67, -61.1) * mm, "end": v(-162.34, -61.06) * mm});
            skLineSegment(sketch, "E782", {"start": v(-162.34, -61.06) * mm, "end": v(-168.24, -60.71) * mm});
            skLineSegment(sketch, "E783", {"start": v(-168.24, -60.71) * mm, "end": v(-169.79, -60.22) * mm});
            skLineSegment(sketch, "E784", {"start": v(-169.79, -60.22) * mm, "end": v(-171.12, -58.45) * mm});
            skLineSegment(sketch, "E785", {"start": v(-171.12, -58.45) * mm, "end": v(-171.64, -56.9) * mm});
            skLineSegment(sketch, "E786", {"start": v(-171.64, -56.9) * mm, "end": v(-171.97, -55.88) * mm});
            skLineSegment(sketch, "E787", {"start": v(-171.97, -55.88) * mm, "end": v(-172.3, -54.85) * mm});
            skLineSegment(sketch, "E788", {"start": v(-172.3, -54.85) * mm, "end": v(-172.8, -53.3) * mm});
            skLineSegment(sketch, "E789", {"start": v(-172.8, -53.3) * mm, "end": v(-172.76, -51.08) * mm});
            skLineSegment(sketch, "E790", {"start": v(-172.76, -51.08) * mm, "end": v(-171.8, -49.77) * mm});
            skLineSegment(sketch, "E791", {"start": v(-171.8, -49.77) * mm, "end": v(-167.22, -46.03) * mm});
            skLineSegment(sketch, "E792", {"start": v(-167.22, -46.03) * mm, "end": v(-165.9, -45.01) * mm});
            skLineSegment(sketch, "E793", {"start": v(-165.9, -45.01) * mm, "end": v(-163.43, -43.38) * mm});
            skLineSegment(sketch, "E794", {"start": v(-163.43, -43.38) * mm, "end": v(-163, -43.12) * mm});
            skLineSegment(sketch, "E795", {"start": v(-163, -43.12) * mm, "end": v(-161.57, -42.26) * mm});
            skLineSegment(sketch, "E796", {"start": v(-161.57, -42.26) * mm, "end": v(-159.22, -40.98) * mm});
            skLineSegment(sketch, "E797", {"start": v(-159.22, -40.98) * mm, "end": v(-155.1, -38.9) * mm});
            skLineSegment(sketch, "E798", {"start": v(-155.1, -38.9) * mm, "end": v(-154.55, -38.25) * mm});
            skLineSegment(sketch, "E799", {"start": v(-154.55, -38.25) * mm, "end": v(-154.26, -37.73) * mm});
            skLineSegment(sketch, "E800", {"start": v(-154.26, -37.73) * mm, "end": v(-156.27, -28.27) * mm});
            skLineSegment(sketch, "E801", {"start": v(-156.27, -28.27) * mm, "end": v(-156.75, -27.92) * mm});
            skLineSegment(sketch, "E802", {"start": v(-156.75, -27.92) * mm, "end": v(-157.52, -27.56) * mm});
            skLineSegment(sketch, "E803", {"start": v(-157.52, -27.56) * mm, "end": v(-162.13, -27.32) * mm});
            skLineSegment(sketch, "E804", {"start": v(-162.13, -27.32) * mm, "end": v(-164.79, -27.1) * mm});
            skLineSegment(sketch, "E805", {"start": v(-164.79, -27.1) * mm, "end": v(-166.45, -26.9) * mm});
            skLineSegment(sketch, "E806", {"start": v(-166.45, -26.9) * mm, "end": v(-166.94, -26.84) * mm});
            skLineSegment(sketch, "E807", {"start": v(-166.94, -26.84) * mm, "end": v(-169.86, -26.35) * mm});
            skLineSegment(sketch, "E808", {"start": v(-169.86, -26.35) * mm, "end": v(-171.49, -25.97) * mm});
            skLineSegment(sketch, "E809", {"start": v(-171.49, -25.97) * mm, "end": v(-177.2, -24.4) * mm});
            skLineSegment(sketch, "E810", {"start": v(-177.2, -24.4) * mm, "end": v(-178.6, -23.6) * mm});
            skLineSegment(sketch, "E811", {"start": v(-178.6, -23.6) * mm, "end": v(-179.54, -21.6) * mm});
            skLineSegment(sketch, "E812", {"start": v(-179.54, -21.6) * mm, "end": v(-179.72, -19.97) * mm});
            skLineSegment(sketch, "E813", {"start": v(-179.72, -19.97) * mm, "end": v(-179.83, -18.9) * mm});
            skLineSegment(sketch, "E814", {"start": v(-179.83, -18.9) * mm, "end": v(-179.94, -17.83) * mm});
            skLineSegment(sketch, "E815", {"start": v(-179.94, -17.83) * mm, "end": v(-180.1, -16.2) * mm});
            skLineSegment(sketch, "E816", {"start": v(-180.1, -16.2) * mm, "end": v(-179.6, -14.05) * mm});
            skLineSegment(sketch, "E817", {"start": v(-179.6, -14.05) * mm, "end": v(-178.4, -12.97) * mm});
            skLineSegment(sketch, "E818", {"start": v(-178.4, -12.97) * mm, "end": v(-173.14, -10.25) * mm});
            skLineSegment(sketch, "E819", {"start": v(-173.14, -10.25) * mm, "end": v(-171.63, -9.54) * mm});
            skLineSegment(sketch, "E820", {"start": v(-171.63, -9.54) * mm, "end": v(-168.88, -8.45) * mm});
            skLineSegment(sketch, "E821", {"start": v(-168.88, -8.45) * mm, "end": v(-168.4, -8.29) * mm});
            skLineSegment(sketch, "E822", {"start": v(-168.4, -8.29) * mm, "end": v(-166.82, -7.74) * mm});
            skLineSegment(sketch, "E823", {"start": v(-166.82, -7.74) * mm, "end": v(-164.26, -6.98) * mm});
            skLineSegment(sketch, "E824", {"start": v(-164.26, -6.98) * mm, "end": v(-159.8, -5.8) * mm});
            skLineSegment(sketch, "E825", {"start": v(-159.8, -5.8) * mm, "end": v(-159.13, -5.28) * mm});
            skLineSegment(sketch, "E826", {"start": v(-159.13, -5.28) * mm, "end": v(-158.73, -4.84) * mm});
            skLineSegment(sketch, "E827", {"start": v(-158.73, -4.84) * mm, "end": v(-158.73, 4.84) * mm});
            skLineSegment(sketch, "E828", {"start": v(-158.73, 4.84) * mm, "end": v(-159.13, 5.28) * mm});
            skLineSegment(sketch, "E829", {"start": v(-159.13, 5.28) * mm, "end": v(-159.8, 5.8) * mm});
            skLineSegment(sketch, "E830", {"start": v(-159.8, 5.8) * mm, "end": v(-164.26, 6.98) * mm});
            skLineSegment(sketch, "E831", {"start": v(-164.26, 6.98) * mm, "end": v(-166.82, 7.74) * mm});
            skLineSegment(sketch, "E832", {"start": v(-166.82, 7.74) * mm, "end": v(-168.4, 8.29) * mm});
            skLineSegment(sketch, "E833", {"start": v(-168.4, 8.29) * mm, "end": v(-168.88, 8.45) * mm});
            skLineSegment(sketch, "E834", {"start": v(-168.88, 8.45) * mm, "end": v(-171.63, 9.54) * mm});
            skLineSegment(sketch, "E835", {"start": v(-171.63, 9.54) * mm, "end": v(-173.14, 10.25) * mm});
            skLineSegment(sketch, "E836", {"start": v(-173.14, 10.25) * mm, "end": v(-178.4, 12.97) * mm});
            skLineSegment(sketch, "E837", {"start": v(-178.4, 12.97) * mm, "end": v(-179.6, 14.05) * mm});
            skLineSegment(sketch, "E838", {"start": v(-179.6, 14.05) * mm, "end": v(-180.1, 16.2) * mm});
            skLineSegment(sketch, "E839", {"start": v(-180.1, 16.2) * mm, "end": v(-179.94, 17.83) * mm});
            skSolve(sketch);
        }
        {
            var Q0;
            Q0=makeQuery(id+"F0.imprint","IMPRINT",FACE,{"disambiguationData":[TD([[makeQuery(id+"F0.imprint","IMPRINT",EDGE,{"derivedFrom":sQuery(id+"F0.wireOp",EDGE,"E0")}),1.0]])]});
            extrude(context, id + "F1", {"entities" : qUnion([Q0]), "depth" : 3.17 * mm});
        }
        {
            var Q0;
            Q0=makeQuery(id+"F1.opExtrude","CAP_FACE",FACE,{"disambiguationData":[OSD([sQuery(id+"F0.wireOp",EDGE,"E0"),sQuery(id+"F0.wireOp",EDGE,"E1"),sQuery(id+"F0.wireOp",EDGE,"E2"),sQuery(id+"F0.wireOp",EDGE,"E3"),sQuery(id+"F0.wireOp",EDGE,"E4"),sQuery(id+"F0.wireOp",EDGE,"E5"),sQuery(id+"F0.wireOp",EDGE,"E6"),sQuery(id+"F0.wireOp",EDGE,"E7"),sQuery(id+"F0.wireOp",EDGE,"E8"),sQuery(id+"F0.wireOp",EDGE,"E9"),sQuery(id+"F0.wireOp",EDGE,"E10"),sQuery(id+"F0.wireOp",EDGE,"E11"),sQuery(id+"F0.wireOp",EDGE,"E12"),sQuery(id+"F0.wireOp",EDGE,"E13"),sQuery(id+"F0.wireOp",EDGE,"E14"),sQuery(id+"F0.wireOp",EDGE,"E15"),sQuery(id+"F0.wireOp",EDGE,"E16"),sQuery(id+"F0.wireOp",EDGE,"E17"),sQuery(id+"F0.wireOp",EDGE,"E18"),sQuery(id+"F0.wireOp",EDGE,"E19"),sQuery(id+"F0.wireOp",EDGE,"E20"),sQuery(id+"F0.wireOp",EDGE,"E21"),sQuery(id+"F0.wireOp",EDGE,"E22"),sQuery(id+"F0.wireOp",EDGE,"E23"),sQuery(id+"F0.wireOp",EDGE,"E24"),sQuery(id+"F0.wireOp",EDGE,"E25"),sQuery(id+"F0.wireOp",EDGE,"E26"),sQuery(id+"F0.wireOp",EDGE,"E27"),sQuery(id+"F0.wireOp",EDGE,"E28"),sQuery(id+"F0.wireOp",EDGE,"E29"),sQuery(id+"F0.wireOp",EDGE,"E30"),sQuery(id+"F0.wireOp",EDGE,"E31"),sQuery(id+"F0.wireOp",EDGE,"E32"),sQuery(id+"F0.wireOp",EDGE,"E33"),sQuery(id+"F0.wireOp",EDGE,"E34"),sQuery(id+"F0.wireOp",EDGE,"E35"),sQuery(id+"F0.wireOp",EDGE,"E36"),sQuery(id+"F0.wireOp",EDGE,"E37"),sQuery(id+"F0.wireOp",EDGE,"E38"),sQuery(id+"F0.wireOp",EDGE,"E39"),sQuery(id+"F0.wireOp",EDGE,"E40"),sQuery(id+"F0.wireOp",EDGE,"E41"),sQuery(id+"F0.wireOp",EDGE,"E42"),sQuery(id+"F0.wireOp",EDGE,"E43"),sQuery(id+"F0.wireOp",EDGE,"E44"),sQuery(id+"F0.wireOp",EDGE,"E45"),sQuery(id+"F0.wireOp",EDGE,"E46"),sQuery(id+"F0.wireOp",EDGE,"E47"),sQuery(id+"F0.wireOp",EDGE,"E48"),sQuery(id+"F0.wireOp",EDGE,"E49"),sQuery(id+"F0.wireOp",EDGE,"E50"),sQuery(id+"F0.wireOp",EDGE,"E51"),sQuery(id+"F0.wireOp",EDGE,"E52"),sQuery(id+"F0.wireOp",EDGE,"E53"),sQuery(id+"F0.wireOp",EDGE,"E54"),sQuery(id+"F0.wireOp",EDGE,"E55"),sQuery(id+"F0.wireOp",EDGE,"E56"),sQuery(id+"F0.wireOp",EDGE,"E57"),sQuery(id+"F0.wireOp",EDGE,"E58"),sQuery(id+"F0.wireOp",EDGE,"E59"),sQuery(id+"F0.wireOp",EDGE,"E60"),sQuery(id+"F0.wireOp",EDGE,"E61"),sQuery(id+"F0.wireOp",EDGE,"E62"),sQuery(id+"F0.wireOp",EDGE,"E63"),sQuery(id+"F0.wireOp",EDGE,"E64"),sQuery(id+"F0.wireOp",EDGE,"E65"),sQuery(id+"F0.wireOp",EDGE,"E66"),sQuery(id+"F0.wireOp",EDGE,"E67"),sQuery(id+"F0.wireOp",EDGE,"E68"),sQuery(id+"F0.wireOp",EDGE,"E69"),sQuery(id+"F0.wireOp",EDGE,"E70"),sQuery(id+"F0.wireOp",EDGE,"E71"),sQuery(id+"F0.wireOp",EDGE,"E72"),sQuery(id+"F0.wireOp",EDGE,"E73"),sQuery(id+"F0.wireOp",EDGE,"E74"),sQuery(id+"F0.wireOp",EDGE,"E75"),sQuery(id+"F0.wireOp",EDGE,"E76"),sQuery(id+"F0.wireOp",EDGE,"E77"),sQuery(id+"F0.wireOp",EDGE,"E78"),sQuery(id+"F0.wireOp",EDGE,"E79"),sQuery(id+"F0.wireOp",EDGE,"E80"),sQuery(id+"F0.wireOp",EDGE,"E81"),sQuery(id+"F0.wireOp",EDGE,"E82"),sQuery(id+"F0.wireOp",EDGE,"E83"),sQuery(id+"F0.wireOp",EDGE,"E84"),sQuery(id+"F0.wireOp",EDGE,"E85"),sQuery(id+"F0.wireOp",EDGE,"E86"),sQuery(id+"F0.wireOp",EDGE,"E87"),sQuery(id+"F0.wireOp",EDGE,"E88"),sQuery(id+"F0.wireOp",EDGE,"E89"),sQuery(id+"F0.wireOp",EDGE,"E90"),sQuery(id+"F0.wireOp",EDGE,"E91"),sQuery(id+"F0.wireOp",EDGE,"E92"),sQuery(id+"F0.wireOp",EDGE,"E93"),sQuery(id+"F0.wireOp",EDGE,"E94"),sQuery(id+"F0.wireOp",EDGE,"E95"),sQuery(id+"F0.wireOp",EDGE,"E96"),sQuery(id+"F0.wireOp",EDGE,"E97"),sQuery(id+"F0.wireOp",EDGE,"E98"),sQuery(id+"F0.wireOp",EDGE,"E99"),sQuery(id+"F0.wireOp",EDGE,"E100"),sQuery(id+"F0.wireOp",EDGE,"E101"),sQuery(id+"F0.wireOp",EDGE,"E102"),sQuery(id+"F0.wireOp",EDGE,"E103"),sQuery(id+"F0.wireOp",EDGE,"E104"),sQuery(id+"F0.wireOp",EDGE,"E105"),sQuery(id+"F0.wireOp",EDGE,"E106"),sQuery(id+"F0.wireOp",EDGE,"E107"),sQuery(id+"F0.wireOp",EDGE,"E108"),sQuery(id+"F0.wireOp",EDGE,"E109"),sQuery(id+"F0.wireOp",EDGE,"E110"),sQuery(id+"F0.wireOp",EDGE,"E111"),sQuery(id+"F0.wireOp",EDGE,"E112"),sQuery(id+"F0.wireOp",EDGE,"E113"),sQuery(id+"F0.wireOp",EDGE,"E114"),sQuery(id+"F0.wireOp",EDGE,"E115"),sQuery(id+"F0.wireOp",EDGE,"E116"),sQuery(id+"F0.wireOp",EDGE,"E117"),sQuery(id+"F0.wireOp",EDGE,"E118"),sQuery(id+"F0.wireOp",EDGE,"E119"),sQuery(id+"F0.wireOp",EDGE,"E120"),sQuery(id+"F0.wireOp",EDGE,"E121"),sQuery(id+"F0.wireOp",EDGE,"E122"),sQuery(id+"F0.wireOp",EDGE,"E123"),sQuery(id+"F0.wireOp",EDGE,"E124"),sQuery(id+"F0.wireOp",EDGE,"E125"),sQuery(id+"F0.wireOp",EDGE,"E126"),sQuery(id+"F0.wireOp",EDGE,"E127"),sQuery(id+"F0.wireOp",EDGE,"E128"),sQuery(id+"F0.wireOp",EDGE,"E129"),sQuery(id+"F0.wireOp",EDGE,"E130"),sQuery(id+"F0.wireOp",EDGE,"E131"),sQuery(id+"F0.wireOp",EDGE,"E132"),sQuery(id+"F0.wireOp",EDGE,"E133"),sQuery(id+"F0.wireOp",EDGE,"E134"),sQuery(id+"F0.wireOp",EDGE,"E135"),sQuery(id+"F0.wireOp",EDGE,"E136"),sQuery(id+"F0.wireOp",EDGE,"E137"),sQuery(id+"F0.wireOp",EDGE,"E138"),sQuery(id+"F0.wireOp",EDGE,"E139"),sQuery(id+"F0.wireOp",EDGE,"E140"),sQuery(id+"F0.wireOp",EDGE,"E141"),sQuery(id+"F0.wireOp",EDGE,"E142"),sQuery(id+"F0.wireOp",EDGE,"E143"),sQuery(id+"F0.wireOp",EDGE,"E144"),sQuery(id+"F0.wireOp",EDGE,"E145"),sQuery(id+"F0.wireOp",EDGE,"E146"),sQuery(id+"F0.wireOp",EDGE,"E147"),sQuery(id+"F0.wireOp",EDGE,"E148"),sQuery(id+"F0.wireOp",EDGE,"E149"),sQuery(id+"F0.wireOp",EDGE,"E150"),sQuery(id+"F0.wireOp",EDGE,"E151"),sQuery(id+"F0.wireOp",EDGE,"E152"),sQuery(id+"F0.wireOp",EDGE,"E153"),sQuery(id+"F0.wireOp",EDGE,"E154"),sQuery(id+"F0.wireOp",EDGE,"E155"),sQuery(id+"F0.wireOp",EDGE,"E156"),sQuery(id+"F0.wireOp",EDGE,"E157"),sQuery(id+"F0.wireOp",EDGE,"E158"),sQuery(id+"F0.wireOp",EDGE,"E159"),sQuery(id+"F0.wireOp",EDGE,"E160"),sQuery(id+"F0.wireOp",EDGE,"E161"),sQuery(id+"F0.wireOp",EDGE,"E162"),sQuery(id+"F0.wireOp",EDGE,"E163"),sQuery(id+"F0.wireOp",EDGE,"E164"),sQuery(id+"F0.wireOp",EDGE,"E165"),sQuery(id+"F0.wireOp",EDGE,"E166"),sQuery(id+"F0.wireOp",EDGE,"E167"),sQuery(id+"F0.wireOp",EDGE,"E168"),sQuery(id+"F0.wireOp",EDGE,"E169"),sQuery(id+"F0.wireOp",EDGE,"E170"),sQuery(id+"F0.wireOp",EDGE,"E171"),sQuery(id+"F0.wireOp",EDGE,"E172"),sQuery(id+"F0.wireOp",EDGE,"E173"),sQuery(id+"F0.wireOp",EDGE,"E174"),sQuery(id+"F0.wireOp",EDGE,"E175"),sQuery(id+"F0.wireOp",EDGE,"E176"),sQuery(id+"F0.wireOp",EDGE,"E177"),sQuery(id+"F0.wireOp",EDGE,"E178"),sQuery(id+"F0.wireOp",EDGE,"E179"),sQuery(id+"F0.wireOp",EDGE,"E180"),sQuery(id+"F0.wireOp",EDGE,"E181"),sQuery(id+"F0.wireOp",EDGE,"E182"),sQuery(id+"F0.wireOp",EDGE,"E183"),sQuery(id+"F0.wireOp",EDGE,"E184"),sQuery(id+"F0.wireOp",EDGE,"E185"),sQuery(id+"F0.wireOp",EDGE,"E186"),sQuery(id+"F0.wireOp",EDGE,"E187"),sQuery(id+"F0.wireOp",EDGE,"E188"),sQuery(id+"F0.wireOp",EDGE,"E189"),sQuery(id+"F0.wireOp",EDGE,"E190"),sQuery(id+"F0.wireOp",EDGE,"E191"),sQuery(id+"F0.wireOp",EDGE,"E192"),sQuery(id+"F0.wireOp",EDGE,"E193"),sQuery(id+"F0.wireOp",EDGE,"E194"),sQuery(id+"F0.wireOp",EDGE,"E195"),sQuery(id+"F0.wireOp",EDGE,"E196"),sQuery(id+"F0.wireOp",EDGE,"E197"),sQuery(id+"F0.wireOp",EDGE,"E198"),sQuery(id+"F0.wireOp",EDGE,"E199"),sQuery(id+"F0.wireOp",EDGE,"E200"),sQuery(id+"F0.wireOp",EDGE,"E201"),sQuery(id+"F0.wireOp",EDGE,"E202"),sQuery(id+"F0.wireOp",EDGE,"E203"),sQuery(id+"F0.wireOp",EDGE,"E204"),sQuery(id+"F0.wireOp",EDGE,"E205"),sQuery(id+"F0.wireOp",EDGE,"E206"),sQuery(id+"F0.wireOp",EDGE,"E207"),sQuery(id+"F0.wireOp",EDGE,"E208"),sQuery(id+"F0.wireOp",EDGE,"E209"),sQuery(id+"F0.wireOp",EDGE,"E210"),sQuery(id+"F0.wireOp",EDGE,"E211"),sQuery(id+"F0.wireOp",EDGE,"E212"),sQuery(id+"F0.wireOp",EDGE,"E213"),sQuery(id+"F0.wireOp",EDGE,"E214"),sQuery(id+"F0.wireOp",EDGE,"E215"),sQuery(id+"F0.wireOp",EDGE,"E216"),sQuery(id+"F0.wireOp",EDGE,"E217"),sQuery(id+"F0.wireOp",EDGE,"E218"),sQuery(id+"F0.wireOp",EDGE,"E219"),sQuery(id+"F0.wireOp",EDGE,"E220"),sQuery(id+"F0.wireOp",EDGE,"E221"),sQuery(id+"F0.wireOp",EDGE,"E222"),sQuery(id+"F0.wireOp",EDGE,"E223"),sQuery(id+"F0.wireOp",EDGE,"E224"),sQuery(id+"F0.wireOp",EDGE,"E225"),sQuery(id+"F0.wireOp",EDGE,"E226"),sQuery(id+"F0.wireOp",EDGE,"E227"),sQuery(id+"F0.wireOp",EDGE,"E228"),sQuery(id+"F0.wireOp",EDGE,"E229"),sQuery(id+"F0.wireOp",EDGE,"E230"),sQuery(id+"F0.wireOp",EDGE,"E231"),sQuery(id+"F0.wireOp",EDGE,"E232"),sQuery(id+"F0.wireOp",EDGE,"E233"),sQuery(id+"F0.wireOp",EDGE,"E234"),sQuery(id+"F0.wireOp",EDGE,"E235"),sQuery(id+"F0.wireOp",EDGE,"E236"),sQuery(id+"F0.wireOp",EDGE,"E237"),sQuery(id+"F0.wireOp",EDGE,"E238"),sQuery(id+"F0.wireOp",EDGE,"E239"),sQuery(id+"F0.wireOp",EDGE,"E240"),sQuery(id+"F0.wireOp",EDGE,"E241"),sQuery(id+"F0.wireOp",EDGE,"E242"),sQuery(id+"F0.wireOp",EDGE,"E243"),sQuery(id+"F0.wireOp",EDGE,"E244"),sQuery(id+"F0.wireOp",EDGE,"E245"),sQuery(id+"F0.wireOp",EDGE,"E246"),sQuery(id+"F0.wireOp",EDGE,"E247"),sQuery(id+"F0.wireOp",EDGE,"E248"),sQuery(id+"F0.wireOp",EDGE,"E249"),sQuery(id+"F0.wireOp",EDGE,"E250"),sQuery(id+"F0.wireOp",EDGE,"E251"),sQuery(id+"F0.wireOp",EDGE,"E252"),sQuery(id+"F0.wireOp",EDGE,"E253"),sQuery(id+"F0.wireOp",EDGE,"E254"),sQuery(id+"F0.wireOp",EDGE,"E255"),sQuery(id+"F0.wireOp",EDGE,"E256"),sQuery(id+"F0.wireOp",EDGE,"E257"),sQuery(id+"F0.wireOp",EDGE,"E258"),sQuery(id+"F0.wireOp",EDGE,"E259"),sQuery(id+"F0.wireOp",EDGE,"E260"),sQuery(id+"F0.wireOp",EDGE,"E261"),sQuery(id+"F0.wireOp",EDGE,"E262"),sQuery(id+"F0.wireOp",EDGE,"E263"),sQuery(id+"F0.wireOp",EDGE,"E264"),sQuery(id+"F0.wireOp",EDGE,"E265"),sQuery(id+"F0.wireOp",EDGE,"E266"),sQuery(id+"F0.wireOp",EDGE,"E267"),sQuery(id+"F0.wireOp",EDGE,"E268"),sQuery(id+"F0.wireOp",EDGE,"E269"),sQuery(id+"F0.wireOp",EDGE,"E270"),sQuery(id+"F0.wireOp",EDGE,"E271"),sQuery(id+"F0.wireOp",EDGE,"E272"),sQuery(id+"F0.wireOp",EDGE,"E273"),sQuery(id+"F0.wireOp",EDGE,"E274"),sQuery(id+"F0.wireOp",EDGE,"E275"),sQuery(id+"F0.wireOp",EDGE,"E276"),sQuery(id+"F0.wireOp",EDGE,"E277"),sQuery(id+"F0.wireOp",EDGE,"E278"),sQuery(id+"F0.wireOp",EDGE,"E279"),sQuery(id+"F0.wireOp",EDGE,"E280"),sQuery(id+"F0.wireOp",EDGE,"E281"),sQuery(id+"F0.wireOp",EDGE,"E282"),sQuery(id+"F0.wireOp",EDGE,"E283"),sQuery(id+"F0.wireOp",EDGE,"E284"),sQuery(id+"F0.wireOp",EDGE,"E285"),sQuery(id+"F0.wireOp",EDGE,"E286"),sQuery(id+"F0.wireOp",EDGE,"E287"),sQuery(id+"F0.wireOp",EDGE,"E288"),sQuery(id+"F0.wireOp",EDGE,"E289"),sQuery(id+"F0.wireOp",EDGE,"E290"),sQuery(id+"F0.wireOp",EDGE,"E291"),sQuery(id+"F0.wireOp",EDGE,"E292"),sQuery(id+"F0.wireOp",EDGE,"E293"),sQuery(id+"F0.wireOp",EDGE,"E294"),sQuery(id+"F0.wireOp",EDGE,"E295"),sQuery(id+"F0.wireOp",EDGE,"E296"),sQuery(id+"F0.wireOp",EDGE,"E297"),sQuery(id+"F0.wireOp",EDGE,"E298"),sQuery(id+"F0.wireOp",EDGE,"E299"),sQuery(id+"F0.wireOp",EDGE,"E300"),sQuery(id+"F0.wireOp",EDGE,"E301"),sQuery(id+"F0.wireOp",EDGE,"E302"),sQuery(id+"F0.wireOp",EDGE,"E303"),sQuery(id+"F0.wireOp",EDGE,"E304"),sQuery(id+"F0.wireOp",EDGE,"E305"),sQuery(id+"F0.wireOp",EDGE,"E306"),sQuery(id+"F0.wireOp",EDGE,"E307"),sQuery(id+"F0.wireOp",EDGE,"E308"),sQuery(id+"F0.wireOp",EDGE,"E309"),sQuery(id+"F0.wireOp",EDGE,"E310"),sQuery(id+"F0.wireOp",EDGE,"E311"),sQuery(id+"F0.wireOp",EDGE,"E312"),sQuery(id+"F0.wireOp",EDGE,"E313"),sQuery(id+"F0.wireOp",EDGE,"E314"),sQuery(id+"F0.wireOp",EDGE,"E315"),sQuery(id+"F0.wireOp",EDGE,"E316"),sQuery(id+"F0.wireOp",EDGE,"E317"),sQuery(id+"F0.wireOp",EDGE,"E318"),sQuery(id+"F0.wireOp",EDGE,"E319"),sQuery(id+"F0.wireOp",EDGE,"E320"),sQuery(id+"F0.wireOp",EDGE,"E321"),sQuery(id+"F0.wireOp",EDGE,"E322"),sQuery(id+"F0.wireOp",EDGE,"E323"),sQuery(id+"F0.wireOp",EDGE,"E324"),sQuery(id+"F0.wireOp",EDGE,"E325"),sQuery(id+"F0.wireOp",EDGE,"E326"),sQuery(id+"F0.wireOp",EDGE,"E327"),sQuery(id+"F0.wireOp",EDGE,"E328"),sQuery(id+"F0.wireOp",EDGE,"E329"),sQuery(id+"F0.wireOp",EDGE,"E330"),sQuery(id+"F0.wireOp",EDGE,"E331"),sQuery(id+"F0.wireOp",EDGE,"E332"),sQuery(id+"F0.wireOp",EDGE,"E333"),sQuery(id+"F0.wireOp",EDGE,"E334"),sQuery(id+"F0.wireOp",EDGE,"E335"),sQuery(id+"F0.wireOp",EDGE,"E336"),sQuery(id+"F0.wireOp",EDGE,"E337"),sQuery(id+"F0.wireOp",EDGE,"E338"),sQuery(id+"F0.wireOp",EDGE,"E339"),sQuery(id+"F0.wireOp",EDGE,"E340"),sQuery(id+"F0.wireOp",EDGE,"E341"),sQuery(id+"F0.wireOp",EDGE,"E342"),sQuery(id+"F0.wireOp",EDGE,"E343"),sQuery(id+"F0.wireOp",EDGE,"E344"),sQuery(id+"F0.wireOp",EDGE,"E345"),sQuery(id+"F0.wireOp",EDGE,"E346"),sQuery(id+"F0.wireOp",EDGE,"E347"),sQuery(id+"F0.wireOp",EDGE,"E348"),sQuery(id+"F0.wireOp",EDGE,"E349"),sQuery(id+"F0.wireOp",EDGE,"E350"),sQuery(id+"F0.wireOp",EDGE,"E351"),sQuery(id+"F0.wireOp",EDGE,"E352"),sQuery(id+"F0.wireOp",EDGE,"E353"),sQuery(id+"F0.wireOp",EDGE,"E354"),sQuery(id+"F0.wireOp",EDGE,"E355"),sQuery(id+"F0.wireOp",EDGE,"E356"),sQuery(id+"F0.wireOp",EDGE,"E357"),sQuery(id+"F0.wireOp",EDGE,"E358"),sQuery(id+"F0.wireOp",EDGE,"E359"),sQuery(id+"F0.wireOp",EDGE,"E360"),sQuery(id+"F0.wireOp",EDGE,"E361"),sQuery(id+"F0.wireOp",EDGE,"E362"),sQuery(id+"F0.wireOp",EDGE,"E363"),sQuery(id+"F0.wireOp",EDGE,"E364"),sQuery(id+"F0.wireOp",EDGE,"E365"),sQuery(id+"F0.wireOp",EDGE,"E366"),sQuery(id+"F0.wireOp",EDGE,"E367"),sQuery(id+"F0.wireOp",EDGE,"E368"),sQuery(id+"F0.wireOp",EDGE,"E369"),sQuery(id+"F0.wireOp",EDGE,"E370"),sQuery(id+"F0.wireOp",EDGE,"E371"),sQuery(id+"F0.wireOp",EDGE,"E372"),sQuery(id+"F0.wireOp",EDGE,"E373"),sQuery(id+"F0.wireOp",EDGE,"E374"),sQuery(id+"F0.wireOp",EDGE,"E375"),sQuery(id+"F0.wireOp",EDGE,"E376"),sQuery(id+"F0.wireOp",EDGE,"E377"),sQuery(id+"F0.wireOp",EDGE,"E378"),sQuery(id+"F0.wireOp",EDGE,"E379"),sQuery(id+"F0.wireOp",EDGE,"E380"),sQuery(id+"F0.wireOp",EDGE,"E381"),sQuery(id+"F0.wireOp",EDGE,"E382"),sQuery(id+"F0.wireOp",EDGE,"E383"),sQuery(id+"F0.wireOp",EDGE,"E384"),sQuery(id+"F0.wireOp",EDGE,"E385"),sQuery(id+"F0.wireOp",EDGE,"E386"),sQuery(id+"F0.wireOp",EDGE,"E387"),sQuery(id+"F0.wireOp",EDGE,"E388"),sQuery(id+"F0.wireOp",EDGE,"E389"),sQuery(id+"F0.wireOp",EDGE,"E390"),sQuery(id+"F0.wireOp",EDGE,"E391"),sQuery(id+"F0.wireOp",EDGE,"E392"),sQuery(id+"F0.wireOp",EDGE,"E393"),sQuery(id+"F0.wireOp",EDGE,"E394"),sQuery(id+"F0.wireOp",EDGE,"E395"),sQuery(id+"F0.wireOp",EDGE,"E396"),sQuery(id+"F0.wireOp",EDGE,"E397"),sQuery(id+"F0.wireOp",EDGE,"E398"),sQuery(id+"F0.wireOp",EDGE,"E399"),sQuery(id+"F0.wireOp",EDGE,"E400"),sQuery(id+"F0.wireOp",EDGE,"E401"),sQuery(id+"F0.wireOp",EDGE,"E402"),sQuery(id+"F0.wireOp",EDGE,"E403"),sQuery(id+"F0.wireOp",EDGE,"E404"),sQuery(id+"F0.wireOp",EDGE,"E405"),sQuery(id+"F0.wireOp",EDGE,"E406"),sQuery(id+"F0.wireOp",EDGE,"E407"),sQuery(id+"F0.wireOp",EDGE,"E408"),sQuery(id+"F0.wireOp",EDGE,"E409"),sQuery(id+"F0.wireOp",EDGE,"E410"),sQuery(id+"F0.wireOp",EDGE,"E411"),sQuery(id+"F0.wireOp",EDGE,"E412"),sQuery(id+"F0.wireOp",EDGE,"E413"),sQuery(id+"F0.wireOp",EDGE,"E414"),sQuery(id+"F0.wireOp",EDGE,"E415"),sQuery(id+"F0.wireOp",EDGE,"E416"),sQuery(id+"F0.wireOp",EDGE,"E417"),sQuery(id+"F0.wireOp",EDGE,"E418"),sQuery(id+"F0.wireOp",EDGE,"E419"),sQuery(id+"F0.wireOp",EDGE,"E420"),sQuery(id+"F0.wireOp",EDGE,"E421"),sQuery(id+"F0.wireOp",EDGE,"E422"),sQuery(id+"F0.wireOp",EDGE,"E423"),sQuery(id+"F0.wireOp",EDGE,"E424"),sQuery(id+"F0.wireOp",EDGE,"E425"),sQuery(id+"F0.wireOp",EDGE,"E426"),sQuery(id+"F0.wireOp",EDGE,"E427"),sQuery(id+"F0.wireOp",EDGE,"E428"),sQuery(id+"F0.wireOp",EDGE,"E429"),sQuery(id+"F0.wireOp",EDGE,"E430"),sQuery(id+"F0.wireOp",EDGE,"E431"),sQuery(id+"F0.wireOp",EDGE,"E432"),sQuery(id+"F0.wireOp",EDGE,"E433"),sQuery(id+"F0.wireOp",EDGE,"E434"),sQuery(id+"F0.wireOp",EDGE,"E435"),sQuery(id+"F0.wireOp",EDGE,"E436"),sQuery(id+"F0.wireOp",EDGE,"E437"),sQuery(id+"F0.wireOp",EDGE,"E438"),sQuery(id+"F0.wireOp",EDGE,"E439"),sQuery(id+"F0.wireOp",EDGE,"E440"),sQuery(id+"F0.wireOp",EDGE,"E441"),sQuery(id+"F0.wireOp",EDGE,"E442"),sQuery(id+"F0.wireOp",EDGE,"E443"),sQuery(id+"F0.wireOp",EDGE,"E444"),sQuery(id+"F0.wireOp",EDGE,"E445"),sQuery(id+"F0.wireOp",EDGE,"E446"),sQuery(id+"F0.wireOp",EDGE,"E447"),sQuery(id+"F0.wireOp",EDGE,"E448"),sQuery(id+"F0.wireOp",EDGE,"E449"),sQuery(id+"F0.wireOp",EDGE,"E450"),sQuery(id+"F0.wireOp",EDGE,"E451"),sQuery(id+"F0.wireOp",EDGE,"E452"),sQuery(id+"F0.wireOp",EDGE,"E453"),sQuery(id+"F0.wireOp",EDGE,"E454"),sQuery(id+"F0.wireOp",EDGE,"E455"),sQuery(id+"F0.wireOp",EDGE,"E456"),sQuery(id+"F0.wireOp",EDGE,"E457"),sQuery(id+"F0.wireOp",EDGE,"E458"),sQuery(id+"F0.wireOp",EDGE,"E459"),sQuery(id+"F0.wireOp",EDGE,"E460"),sQuery(id+"F0.wireOp",EDGE,"E461"),sQuery(id+"F0.wireOp",EDGE,"E462"),sQuery(id+"F0.wireOp",EDGE,"E463"),sQuery(id+"F0.wireOp",EDGE,"E464"),sQuery(id+"F0.wireOp",EDGE,"E465"),sQuery(id+"F0.wireOp",EDGE,"E466"),sQuery(id+"F0.wireOp",EDGE,"E467"),sQuery(id+"F0.wireOp",EDGE,"E468"),sQuery(id+"F0.wireOp",EDGE,"E469"),sQuery(id+"F0.wireOp",EDGE,"E470"),sQuery(id+"F0.wireOp",EDGE,"E471"),sQuery(id+"F0.wireOp",EDGE,"E472"),sQuery(id+"F0.wireOp",EDGE,"E473"),sQuery(id+"F0.wireOp",EDGE,"E474"),sQuery(id+"F0.wireOp",EDGE,"E475"),sQuery(id+"F0.wireOp",EDGE,"E476"),sQuery(id+"F0.wireOp",EDGE,"E477"),sQuery(id+"F0.wireOp",EDGE,"E478"),sQuery(id+"F0.wireOp",EDGE,"E479"),sQuery(id+"F0.wireOp",EDGE,"E480"),sQuery(id+"F0.wireOp",EDGE,"E481"),sQuery(id+"F0.wireOp",EDGE,"E482"),sQuery(id+"F0.wireOp",EDGE,"E483"),sQuery(id+"F0.wireOp",EDGE,"E484"),sQuery(id+"F0.wireOp",EDGE,"E485"),sQuery(id+"F0.wireOp",EDGE,"E486"),sQuery(id+"F0.wireOp",EDGE,"E487"),sQuery(id+"F0.wireOp",EDGE,"E488"),sQuery(id+"F0.wireOp",EDGE,"E489"),sQuery(id+"F0.wireOp",EDGE,"E490"),sQuery(id+"F0.wireOp",EDGE,"E491"),sQuery(id+"F0.wireOp",EDGE,"E492"),sQuery(id+"F0.wireOp",EDGE,"E493"),sQuery(id+"F0.wireOp",EDGE,"E494"),sQuery(id+"F0.wireOp",EDGE,"E495"),sQuery(id+"F0.wireOp",EDGE,"E496"),sQuery(id+"F0.wireOp",EDGE,"E497"),sQuery(id+"F0.wireOp",EDGE,"E498"),sQuery(id+"F0.wireOp",EDGE,"E499"),sQuery(id+"F0.wireOp",EDGE,"E500"),sQuery(id+"F0.wireOp",EDGE,"E501"),sQuery(id+"F0.wireOp",EDGE,"E502"),sQuery(id+"F0.wireOp",EDGE,"E503"),sQuery(id+"F0.wireOp",EDGE,"E504"),sQuery(id+"F0.wireOp",EDGE,"E505"),sQuery(id+"F0.wireOp",EDGE,"E506"),sQuery(id+"F0.wireOp",EDGE,"E507"),sQuery(id+"F0.wireOp",EDGE,"E508"),sQuery(id+"F0.wireOp",EDGE,"E509"),sQuery(id+"F0.wireOp",EDGE,"E510"),sQuery(id+"F0.wireOp",EDGE,"E511"),sQuery(id+"F0.wireOp",EDGE,"E512"),sQuery(id+"F0.wireOp",EDGE,"E513"),sQuery(id+"F0.wireOp",EDGE,"E514"),sQuery(id+"F0.wireOp",EDGE,"E515"),sQuery(id+"F0.wireOp",EDGE,"E516"),sQuery(id+"F0.wireOp",EDGE,"E517"),sQuery(id+"F0.wireOp",EDGE,"E518"),sQuery(id+"F0.wireOp",EDGE,"E519"),sQuery(id+"F0.wireOp",EDGE,"E520"),sQuery(id+"F0.wireOp",EDGE,"E521"),sQuery(id+"F0.wireOp",EDGE,"E522"),sQuery(id+"F0.wireOp",EDGE,"E523"),sQuery(id+"F0.wireOp",EDGE,"E524"),sQuery(id+"F0.wireOp",EDGE,"E525"),sQuery(id+"F0.wireOp",EDGE,"E526"),sQuery(id+"F0.wireOp",EDGE,"E527"),sQuery(id+"F0.wireOp",EDGE,"E528"),sQuery(id+"F0.wireOp",EDGE,"E529"),sQuery(id+"F0.wireOp",EDGE,"E530"),sQuery(id+"F0.wireOp",EDGE,"E531"),sQuery(id+"F0.wireOp",EDGE,"E532"),sQuery(id+"F0.wireOp",EDGE,"E533"),sQuery(id+"F0.wireOp",EDGE,"E534"),sQuery(id+"F0.wireOp",EDGE,"E535"),sQuery(id+"F0.wireOp",EDGE,"E536"),sQuery(id+"F0.wireOp",EDGE,"E537"),sQuery(id+"F0.wireOp",EDGE,"E538"),sQuery(id+"F0.wireOp",EDGE,"E539"),sQuery(id+"F0.wireOp",EDGE,"E540"),sQuery(id+"F0.wireOp",EDGE,"E541"),sQuery(id+"F0.wireOp",EDGE,"E542"),sQuery(id+"F0.wireOp",EDGE,"E543"),sQuery(id+"F0.wireOp",EDGE,"E544"),sQuery(id+"F0.wireOp",EDGE,"E545"),sQuery(id+"F0.wireOp",EDGE,"E546"),sQuery(id+"F0.wireOp",EDGE,"E547"),sQuery(id+"F0.wireOp",EDGE,"E548"),sQuery(id+"F0.wireOp",EDGE,"E549"),sQuery(id+"F0.wireOp",EDGE,"E550"),sQuery(id+"F0.wireOp",EDGE,"E551"),sQuery(id+"F0.wireOp",EDGE,"E552"),sQuery(id+"F0.wireOp",EDGE,"E553"),sQuery(id+"F0.wireOp",EDGE,"E554"),sQuery(id+"F0.wireOp",EDGE,"E555"),sQuery(id+"F0.wireOp",EDGE,"E556"),sQuery(id+"F0.wireOp",EDGE,"E557"),sQuery(id+"F0.wireOp",EDGE,"E558"),sQuery(id+"F0.wireOp",EDGE,"E559"),sQuery(id+"F0.wireOp",EDGE,"E560"),sQuery(id+"F0.wireOp",EDGE,"E561"),sQuery(id+"F0.wireOp",EDGE,"E562"),sQuery(id+"F0.wireOp",EDGE,"E563"),sQuery(id+"F0.wireOp",EDGE,"E564"),sQuery(id+"F0.wireOp",EDGE,"E565"),sQuery(id+"F0.wireOp",EDGE,"E566"),sQuery(id+"F0.wireOp",EDGE,"E567"),sQuery(id+"F0.wireOp",EDGE,"E568"),sQuery(id+"F0.wireOp",EDGE,"E569"),sQuery(id+"F0.wireOp",EDGE,"E570"),sQuery(id+"F0.wireOp",EDGE,"E571"),sQuery(id+"F0.wireOp",EDGE,"E572"),sQuery(id+"F0.wireOp",EDGE,"E573"),sQuery(id+"F0.wireOp",EDGE,"E574"),sQuery(id+"F0.wireOp",EDGE,"E575"),sQuery(id+"F0.wireOp",EDGE,"E576"),sQuery(id+"F0.wireOp",EDGE,"E577"),sQuery(id+"F0.wireOp",EDGE,"E578"),sQuery(id+"F0.wireOp",EDGE,"E579"),sQuery(id+"F0.wireOp",EDGE,"E580"),sQuery(id+"F0.wireOp",EDGE,"E581"),sQuery(id+"F0.wireOp",EDGE,"E582"),sQuery(id+"F0.wireOp",EDGE,"E583"),sQuery(id+"F0.wireOp",EDGE,"E584"),sQuery(id+"F0.wireOp",EDGE,"E585"),sQuery(id+"F0.wireOp",EDGE,"E586"),sQuery(id+"F0.wireOp",EDGE,"E587"),sQuery(id+"F0.wireOp",EDGE,"E588"),sQuery(id+"F0.wireOp",EDGE,"E589"),sQuery(id+"F0.wireOp",EDGE,"E590"),sQuery(id+"F0.wireOp",EDGE,"E591"),sQuery(id+"F0.wireOp",EDGE,"E592"),sQuery(id+"F0.wireOp",EDGE,"E593"),sQuery(id+"F0.wireOp",EDGE,"E594"),sQuery(id+"F0.wireOp",EDGE,"E595"),sQuery(id+"F0.wireOp",EDGE,"E596"),sQuery(id+"F0.wireOp",EDGE,"E597"),sQuery(id+"F0.wireOp",EDGE,"E598"),sQuery(id+"F0.wireOp",EDGE,"E599"),sQuery(id+"F0.wireOp",EDGE,"E600"),sQuery(id+"F0.wireOp",EDGE,"E601"),sQuery(id+"F0.wireOp",EDGE,"E602"),sQuery(id+"F0.wireOp",EDGE,"E603"),sQuery(id+"F0.wireOp",EDGE,"E604"),sQuery(id+"F0.wireOp",EDGE,"E605"),sQuery(id+"F0.wireOp",EDGE,"E606"),sQuery(id+"F0.wireOp",EDGE,"E607"),sQuery(id+"F0.wireOp",EDGE,"E608"),sQuery(id+"F0.wireOp",EDGE,"E609"),sQuery(id+"F0.wireOp",EDGE,"E610"),sQuery(id+"F0.wireOp",EDGE,"E611"),sQuery(id+"F0.wireOp",EDGE,"E612"),sQuery(id+"F0.wireOp",EDGE,"E613"),sQuery(id+"F0.wireOp",EDGE,"E614"),sQuery(id+"F0.wireOp",EDGE,"E615"),sQuery(id+"F0.wireOp",EDGE,"E616"),sQuery(id+"F0.wireOp",EDGE,"E617"),sQuery(id+"F0.wireOp",EDGE,"E618"),sQuery(id+"F0.wireOp",EDGE,"E619"),sQuery(id+"F0.wireOp",EDGE,"E620"),sQuery(id+"F0.wireOp",EDGE,"E621"),sQuery(id+"F0.wireOp",EDGE,"E622"),sQuery(id+"F0.wireOp",EDGE,"E623"),sQuery(id+"F0.wireOp",EDGE,"E624"),sQuery(id+"F0.wireOp",EDGE,"E625"),sQuery(id+"F0.wireOp",EDGE,"E626"),sQuery(id+"F0.wireOp",EDGE,"E627"),sQuery(id+"F0.wireOp",EDGE,"E628"),sQuery(id+"F0.wireOp",EDGE,"E629"),sQuery(id+"F0.wireOp",EDGE,"E630"),sQuery(id+"F0.wireOp",EDGE,"E631"),sQuery(id+"F0.wireOp",EDGE,"E632"),sQuery(id+"F0.wireOp",EDGE,"E633"),sQuery(id+"F0.wireOp",EDGE,"E634"),sQuery(id+"F0.wireOp",EDGE,"E635"),sQuery(id+"F0.wireOp",EDGE,"E636"),sQuery(id+"F0.wireOp",EDGE,"E637"),sQuery(id+"F0.wireOp",EDGE,"E638"),sQuery(id+"F0.wireOp",EDGE,"E639"),sQuery(id+"F0.wireOp",EDGE,"E640"),sQuery(id+"F0.wireOp",EDGE,"E641"),sQuery(id+"F0.wireOp",EDGE,"E642"),sQuery(id+"F0.wireOp",EDGE,"E643"),sQuery(id+"F0.wireOp",EDGE,"E644"),sQuery(id+"F0.wireOp",EDGE,"E645"),sQuery(id+"F0.wireOp",EDGE,"E646"),sQuery(id+"F0.wireOp",EDGE,"E647"),sQuery(id+"F0.wireOp",EDGE,"E648"),sQuery(id+"F0.wireOp",EDGE,"E649"),sQuery(id+"F0.wireOp",EDGE,"E650"),sQuery(id+"F0.wireOp",EDGE,"E651"),sQuery(id+"F0.wireOp",EDGE,"E652"),sQuery(id+"F0.wireOp",EDGE,"E653"),sQuery(id+"F0.wireOp",EDGE,"E654"),sQuery(id+"F0.wireOp",EDGE,"E655"),sQuery(id+"F0.wireOp",EDGE,"E656"),sQuery(id+"F0.wireOp",EDGE,"E657"),sQuery(id+"F0.wireOp",EDGE,"E658"),sQuery(id+"F0.wireOp",EDGE,"E659"),sQuery(id+"F0.wireOp",EDGE,"E660"),sQuery(id+"F0.wireOp",EDGE,"E661"),sQuery(id+"F0.wireOp",EDGE,"E662"),sQuery(id+"F0.wireOp",EDGE,"E663"),sQuery(id+"F0.wireOp",EDGE,"E664"),sQuery(id+"F0.wireOp",EDGE,"E665"),sQuery(id+"F0.wireOp",EDGE,"E666"),sQuery(id+"F0.wireOp",EDGE,"E667"),sQuery(id+"F0.wireOp",EDGE,"E668"),sQuery(id+"F0.wireOp",EDGE,"E669"),sQuery(id+"F0.wireOp",EDGE,"E670"),sQuery(id+"F0.wireOp",EDGE,"E671"),sQuery(id+"F0.wireOp",EDGE,"E672"),sQuery(id+"F0.wireOp",EDGE,"E673"),sQuery(id+"F0.wireOp",EDGE,"E674"),sQuery(id+"F0.wireOp",EDGE,"E675"),sQuery(id+"F0.wireOp",EDGE,"E676"),sQuery(id+"F0.wireOp",EDGE,"E677"),sQuery(id+"F0.wireOp",EDGE,"E678"),sQuery(id+"F0.wireOp",EDGE,"E679"),sQuery(id+"F0.wireOp",EDGE,"E680"),sQuery(id+"F0.wireOp",EDGE,"E681"),sQuery(id+"F0.wireOp",EDGE,"E682"),sQuery(id+"F0.wireOp",EDGE,"E683"),sQuery(id+"F0.wireOp",EDGE,"E684"),sQuery(id+"F0.wireOp",EDGE,"E685"),sQuery(id+"F0.wireOp",EDGE,"E686"),sQuery(id+"F0.wireOp",EDGE,"E687"),sQuery(id+"F0.wireOp",EDGE,"E688"),sQuery(id+"F0.wireOp",EDGE,"E689"),sQuery(id+"F0.wireOp",EDGE,"E690"),sQuery(id+"F0.wireOp",EDGE,"E691"),sQuery(id+"F0.wireOp",EDGE,"E692"),sQuery(id+"F0.wireOp",EDGE,"E693"),sQuery(id+"F0.wireOp",EDGE,"E694"),sQuery(id+"F0.wireOp",EDGE,"E695"),sQuery(id+"F0.wireOp",EDGE,"E696"),sQuery(id+"F0.wireOp",EDGE,"E697"),sQuery(id+"F0.wireOp",EDGE,"E698"),sQuery(id+"F0.wireOp",EDGE,"E699"),sQuery(id+"F0.wireOp",EDGE,"E700"),sQuery(id+"F0.wireOp",EDGE,"E701"),sQuery(id+"F0.wireOp",EDGE,"E702"),sQuery(id+"F0.wireOp",EDGE,"E703"),sQuery(id+"F0.wireOp",EDGE,"E704"),sQuery(id+"F0.wireOp",EDGE,"E705"),sQuery(id+"F0.wireOp",EDGE,"E706"),sQuery(id+"F0.wireOp",EDGE,"E707"),sQuery(id+"F0.wireOp",EDGE,"E708"),sQuery(id+"F0.wireOp",EDGE,"E709"),sQuery(id+"F0.wireOp",EDGE,"E710"),sQuery(id+"F0.wireOp",EDGE,"E711"),sQuery(id+"F0.wireOp",EDGE,"E712"),sQuery(id+"F0.wireOp",EDGE,"E713"),sQuery(id+"F0.wireOp",EDGE,"E714"),sQuery(id+"F0.wireOp",EDGE,"E715"),sQuery(id+"F0.wireOp",EDGE,"E716"),sQuery(id+"F0.wireOp",EDGE,"E717"),sQuery(id+"F0.wireOp",EDGE,"E718"),sQuery(id+"F0.wireOp",EDGE,"E719"),sQuery(id+"F0.wireOp",EDGE,"E720"),sQuery(id+"F0.wireOp",EDGE,"E721"),sQuery(id+"F0.wireOp",EDGE,"E722"),sQuery(id+"F0.wireOp",EDGE,"E723"),sQuery(id+"F0.wireOp",EDGE,"E724"),sQuery(id+"F0.wireOp",EDGE,"E725"),sQuery(id+"F0.wireOp",EDGE,"E726"),sQuery(id+"F0.wireOp",EDGE,"E727"),sQuery(id+"F0.wireOp",EDGE,"E728"),sQuery(id+"F0.wireOp",EDGE,"E729"),sQuery(id+"F0.wireOp",EDGE,"E730"),sQuery(id+"F0.wireOp",EDGE,"E731"),sQuery(id+"F0.wireOp",EDGE,"E732"),sQuery(id+"F0.wireOp",EDGE,"E733"),sQuery(id+"F0.wireOp",EDGE,"E734"),sQuery(id+"F0.wireOp",EDGE,"E735"),sQuery(id+"F0.wireOp",EDGE,"E736"),sQuery(id+"F0.wireOp",EDGE,"E737"),sQuery(id+"F0.wireOp",EDGE,"E738"),sQuery(id+"F0.wireOp",EDGE,"E739"),sQuery(id+"F0.wireOp",EDGE,"E740"),sQuery(id+"F0.wireOp",EDGE,"E741"),sQuery(id+"F0.wireOp",EDGE,"E742"),sQuery(id+"F0.wireOp",EDGE,"E743"),sQuery(id+"F0.wireOp",EDGE,"E744"),sQuery(id+"F0.wireOp",EDGE,"E745"),sQuery(id+"F0.wireOp",EDGE,"E746"),sQuery(id+"F0.wireOp",EDGE,"E747"),sQuery(id+"F0.wireOp",EDGE,"E748"),sQuery(id+"F0.wireOp",EDGE,"E749"),sQuery(id+"F0.wireOp",EDGE,"E750"),sQuery(id+"F0.wireOp",EDGE,"E751"),sQuery(id+"F0.wireOp",EDGE,"E752"),sQuery(id+"F0.wireOp",EDGE,"E753"),sQuery(id+"F0.wireOp",EDGE,"E754"),sQuery(id+"F0.wireOp",EDGE,"E755"),sQuery(id+"F0.wireOp",EDGE,"E756"),sQuery(id+"F0.wireOp",EDGE,"E757"),sQuery(id+"F0.wireOp",EDGE,"E758"),sQuery(id+"F0.wireOp",EDGE,"E759"),sQuery(id+"F0.wireOp",EDGE,"E760"),sQuery(id+"F0.wireOp",EDGE,"E761"),sQuery(id+"F0.wireOp",EDGE,"E762"),sQuery(id+"F0.wireOp",EDGE,"E763"),sQuery(id+"F0.wireOp",EDGE,"E764"),sQuery(id+"F0.wireOp",EDGE,"E765"),sQuery(id+"F0.wireOp",EDGE,"E766"),sQuery(id+"F0.wireOp",EDGE,"E767"),sQuery(id+"F0.wireOp",EDGE,"E768"),sQuery(id+"F0.wireOp",EDGE,"E769"),sQuery(id+"F0.wireOp",EDGE,"E770"),sQuery(id+"F0.wireOp",EDGE,"E771"),sQuery(id+"F0.wireOp",EDGE,"E772"),sQuery(id+"F0.wireOp",EDGE,"E773"),sQuery(id+"F0.wireOp",EDGE,"E774"),sQuery(id+"F0.wireOp",EDGE,"E775"),sQuery(id+"F0.wireOp",EDGE,"E776"),sQuery(id+"F0.wireOp",EDGE,"E777"),sQuery(id+"F0.wireOp",EDGE,"E778"),sQuery(id+"F0.wireOp",EDGE,"E779"),sQuery(id+"F0.wireOp",EDGE,"E780"),sQuery(id+"F0.wireOp",EDGE,"E781"),sQuery(id+"F0.wireOp",EDGE,"E782"),sQuery(id+"F0.wireOp",EDGE,"E783"),sQuery(id+"F0.wireOp",EDGE,"E784"),sQuery(id+"F0.wireOp",EDGE,"E785"),sQuery(id+"F0.wireOp",EDGE,"E786"),sQuery(id+"F0.wireOp",EDGE,"E787"),sQuery(id+"F0.wireOp",EDGE,"E788"),sQuery(id+"F0.wireOp",EDGE,"E789"),sQuery(id+"F0.wireOp",EDGE,"E790"),sQuery(id+"F0.wireOp",EDGE,"E791"),sQuery(id+"F0.wireOp",EDGE,"E792"),sQuery(id+"F0.wireOp",EDGE,"E793"),sQuery(id+"F0.wireOp",EDGE,"E794"),sQuery(id+"F0.wireOp",EDGE,"E795"),sQuery(id+"F0.wireOp",EDGE,"E796"),sQuery(id+"F0.wireOp",EDGE,"E797"),sQuery(id+"F0.wireOp",EDGE,"E798"),sQuery(id+"F0.wireOp",EDGE,"E799"),sQuery(id+"F0.wireOp",EDGE,"E800"),sQuery(id+"F0.wireOp",EDGE,"E801"),sQuery(id+"F0.wireOp",EDGE,"E802"),sQuery(id+"F0.wireOp",EDGE,"E803"),sQuery(id+"F0.wireOp",EDGE,"E804"),sQuery(id+"F0.wireOp",EDGE,"E805"),sQuery(id+"F0.wireOp",EDGE,"E806"),sQuery(id+"F0.wireOp",EDGE,"E807"),sQuery(id+"F0.wireOp",EDGE,"E808"),sQuery(id+"F0.wireOp",EDGE,"E809"),sQuery(id+"F0.wireOp",EDGE,"E810"),sQuery(id+"F0.wireOp",EDGE,"E811"),sQuery(id+"F0.wireOp",EDGE,"E812"),sQuery(id+"F0.wireOp",EDGE,"E813"),sQuery(id+"F0.wireOp",EDGE,"E814"),sQuery(id+"F0.wireOp",EDGE,"E815"),sQuery(id+"F0.wireOp",EDGE,"E816"),sQuery(id+"F0.wireOp",EDGE,"E817"),sQuery(id+"F0.wireOp",EDGE,"E818"),sQuery(id+"F0.wireOp",EDGE,"E819"),sQuery(id+"F0.wireOp",EDGE,"E820"),sQuery(id+"F0.wireOp",EDGE,"E821"),sQuery(id+"F0.wireOp",EDGE,"E822"),sQuery(id+"F0.wireOp",EDGE,"E823"),sQuery(id+"F0.wireOp",EDGE,"E824"),sQuery(id+"F0.wireOp",EDGE,"E825"),sQuery(id+"F0.wireOp",EDGE,"E826"),sQuery(id+"F0.wireOp",EDGE,"E827"),sQuery(id+"F0.wireOp",EDGE,"E828"),sQuery(id+"F0.wireOp",EDGE,"E829"),sQuery(id+"F0.wireOp",EDGE,"E830"),sQuery(id+"F0.wireOp",EDGE,"E831"),sQuery(id+"F0.wireOp",EDGE,"E832"),sQuery(id+"F0.wireOp",EDGE,"E833"),sQuery(id+"F0.wireOp",EDGE,"E834"),sQuery(id+"F0.wireOp",EDGE,"E835"),sQuery(id+"F0.wireOp",EDGE,"E836"),sQuery(id+"F0.wireOp",EDGE,"E837"),sQuery(id+"F0.wireOp",EDGE,"E838"),sQuery(id+"F0.wireOp",EDGE,"E839")])],"isStart":false});
            var sketch = newSketch(context, id + "F2", { "sketchPlane" : qUnion([Q0])});
            skCircle(sketch, "E840", {"center": v(0, 0) * mm, "radius": 225.43 * mm});
            skSolve(sketch);
        }
        {
            var Q0;
            Q0=makeQuery(id+"F2.imprint","IMPRINT",FACE,{"disambiguationData":[TD([[makeQuery(id+"F2.imprint","IMPRINT",EDGE,{"derivedFrom":makeQuery(id+"F1.opExtrude","CAP_EDGE",EDGE,{"disambiguationData":[OSD([sQuery(id+"F0.wireOp",EDGE,"E30")])],"isStart":false})}),1.0]])]});
            extrude(context, id + "F3", {"entities" : qUnion([Q0]), "operationType" : NewBodyOperationType.INTERSECT, "endBound" : BoundingType.UP_TO_NEXT, "oppositeDirection" : true, "depth" : 25.4 * mm});
        }
        {
            var Q0;
            Q0=makeQuery(id+"F1.opExtrude","CAP_FACE",FACE,{"disambiguationData":[OSD([sQuery(id+"F0.wireOp",EDGE,"E0"),sQuery(id+"F0.wireOp",EDGE,"E1"),sQuery(id+"F0.wireOp",EDGE,"E2"),sQuery(id+"F0.wireOp",EDGE,"E3"),sQuery(id+"F0.wireOp",EDGE,"E4"),sQuery(id+"F0.wireOp",EDGE,"E5"),sQuery(id+"F0.wireOp",EDGE,"E6"),sQuery(id+"F0.wireOp",EDGE,"E7"),sQuery(id+"F0.wireOp",EDGE,"E8"),sQuery(id+"F0.wireOp",EDGE,"E9"),sQuery(id+"F0.wireOp",EDGE,"E10"),sQuery(id+"F0.wireOp",EDGE,"E11"),sQuery(id+"F0.wireOp",EDGE,"E12"),sQuery(id+"F0.wireOp",EDGE,"E13"),sQuery(id+"F0.wireOp",EDGE,"E14"),sQuery(id+"F0.wireOp",EDGE,"E15"),sQuery(id+"F0.wireOp",EDGE,"E16"),sQuery(id+"F0.wireOp",EDGE,"E17"),sQuery(id+"F0.wireOp",EDGE,"E18"),sQuery(id+"F0.wireOp",EDGE,"E19"),sQuery(id+"F0.wireOp",EDGE,"E20"),sQuery(id+"F0.wireOp",EDGE,"E21"),sQuery(id+"F0.wireOp",EDGE,"E22"),sQuery(id+"F0.wireOp",EDGE,"E23"),sQuery(id+"F0.wireOp",EDGE,"E24"),sQuery(id+"F0.wireOp",EDGE,"E25"),sQuery(id+"F0.wireOp",EDGE,"E26"),sQuery(id+"F0.wireOp",EDGE,"E27"),sQuery(id+"F0.wireOp",EDGE,"E28"),sQuery(id+"F0.wireOp",EDGE,"E29"),sQuery(id+"F0.wireOp",EDGE,"E30"),sQuery(id+"F0.wireOp",EDGE,"E31"),sQuery(id+"F0.wireOp",EDGE,"E32"),sQuery(id+"F0.wireOp",EDGE,"E33"),sQuery(id+"F0.wireOp",EDGE,"E34"),sQuery(id+"F0.wireOp",EDGE,"E35"),sQuery(id+"F0.wireOp",EDGE,"E36"),sQuery(id+"F0.wireOp",EDGE,"E37"),sQuery(id+"F0.wireOp",EDGE,"E38"),sQuery(id+"F0.wireOp",EDGE,"E39"),sQuery(id+"F0.wireOp",EDGE,"E40"),sQuery(id+"F0.wireOp",EDGE,"E41"),sQuery(id+"F0.wireOp",EDGE,"E42"),sQuery(id+"F0.wireOp",EDGE,"E43"),sQuery(id+"F0.wireOp",EDGE,"E44"),sQuery(id+"F0.wireOp",EDGE,"E45"),sQuery(id+"F0.wireOp",EDGE,"E46"),sQuery(id+"F0.wireOp",EDGE,"E47"),sQuery(id+"F0.wireOp",EDGE,"E48"),sQuery(id+"F0.wireOp",EDGE,"E49"),sQuery(id+"F0.wireOp",EDGE,"E50"),sQuery(id+"F0.wireOp",EDGE,"E51"),sQuery(id+"F0.wireOp",EDGE,"E52"),sQuery(id+"F0.wireOp",EDGE,"E53"),sQuery(id+"F0.wireOp",EDGE,"E54"),sQuery(id+"F0.wireOp",EDGE,"E55"),sQuery(id+"F0.wireOp",EDGE,"E56"),sQuery(id+"F0.wireOp",EDGE,"E57"),sQuery(id+"F0.wireOp",EDGE,"E58"),sQuery(id+"F0.wireOp",EDGE,"E59"),sQuery(id+"F0.wireOp",EDGE,"E60"),sQuery(id+"F0.wireOp",EDGE,"E61"),sQuery(id+"F0.wireOp",EDGE,"E62"),sQuery(id+"F0.wireOp",EDGE,"E63"),sQuery(id+"F0.wireOp",EDGE,"E64"),sQuery(id+"F0.wireOp",EDGE,"E65"),sQuery(id+"F0.wireOp",EDGE,"E66"),sQuery(id+"F0.wireOp",EDGE,"E67"),sQuery(id+"F0.wireOp",EDGE,"E68"),sQuery(id+"F0.wireOp",EDGE,"E69"),sQuery(id+"F0.wireOp",EDGE,"E70"),sQuery(id+"F0.wireOp",EDGE,"E71"),sQuery(id+"F0.wireOp",EDGE,"E72"),sQuery(id+"F0.wireOp",EDGE,"E73"),sQuery(id+"F0.wireOp",EDGE,"E74"),sQuery(id+"F0.wireOp",EDGE,"E75"),sQuery(id+"F0.wireOp",EDGE,"E76"),sQuery(id+"F0.wireOp",EDGE,"E77"),sQuery(id+"F0.wireOp",EDGE,"E78"),sQuery(id+"F0.wireOp",EDGE,"E79"),sQuery(id+"F0.wireOp",EDGE,"E80"),sQuery(id+"F0.wireOp",EDGE,"E81"),sQuery(id+"F0.wireOp",EDGE,"E82"),sQuery(id+"F0.wireOp",EDGE,"E83"),sQuery(id+"F0.wireOp",EDGE,"E84"),sQuery(id+"F0.wireOp",EDGE,"E85"),sQuery(id+"F0.wireOp",EDGE,"E86"),sQuery(id+"F0.wireOp",EDGE,"E87"),sQuery(id+"F0.wireOp",EDGE,"E88"),sQuery(id+"F0.wireOp",EDGE,"E89"),sQuery(id+"F0.wireOp",EDGE,"E90"),sQuery(id+"F0.wireOp",EDGE,"E91"),sQuery(id+"F0.wireOp",EDGE,"E92"),sQuery(id+"F0.wireOp",EDGE,"E93"),sQuery(id+"F0.wireOp",EDGE,"E94"),sQuery(id+"F0.wireOp",EDGE,"E95"),sQuery(id+"F0.wireOp",EDGE,"E96"),sQuery(id+"F0.wireOp",EDGE,"E97"),sQuery(id+"F0.wireOp",EDGE,"E98"),sQuery(id+"F0.wireOp",EDGE,"E99"),sQuery(id+"F0.wireOp",EDGE,"E100"),sQuery(id+"F0.wireOp",EDGE,"E101"),sQuery(id+"F0.wireOp",EDGE,"E102"),sQuery(id+"F0.wireOp",EDGE,"E103"),sQuery(id+"F0.wireOp",EDGE,"E104"),sQuery(id+"F0.wireOp",EDGE,"E105"),sQuery(id+"F0.wireOp",EDGE,"E106"),sQuery(id+"F0.wireOp",EDGE,"E107"),sQuery(id+"F0.wireOp",EDGE,"E108"),sQuery(id+"F0.wireOp",EDGE,"E109"),sQuery(id+"F0.wireOp",EDGE,"E110"),sQuery(id+"F0.wireOp",EDGE,"E111"),sQuery(id+"F0.wireOp",EDGE,"E112"),sQuery(id+"F0.wireOp",EDGE,"E113"),sQuery(id+"F0.wireOp",EDGE,"E114"),sQuery(id+"F0.wireOp",EDGE,"E115"),sQuery(id+"F0.wireOp",EDGE,"E116"),sQuery(id+"F0.wireOp",EDGE,"E117"),sQuery(id+"F0.wireOp",EDGE,"E118"),sQuery(id+"F0.wireOp",EDGE,"E119"),sQuery(id+"F0.wireOp",EDGE,"E120"),sQuery(id+"F0.wireOp",EDGE,"E121"),sQuery(id+"F0.wireOp",EDGE,"E122"),sQuery(id+"F0.wireOp",EDGE,"E123"),sQuery(id+"F0.wireOp",EDGE,"E124"),sQuery(id+"F0.wireOp",EDGE,"E125"),sQuery(id+"F0.wireOp",EDGE,"E126"),sQuery(id+"F0.wireOp",EDGE,"E127"),sQuery(id+"F0.wireOp",EDGE,"E128"),sQuery(id+"F0.wireOp",EDGE,"E129"),sQuery(id+"F0.wireOp",EDGE,"E130"),sQuery(id+"F0.wireOp",EDGE,"E131"),sQuery(id+"F0.wireOp",EDGE,"E132"),sQuery(id+"F0.wireOp",EDGE,"E133"),sQuery(id+"F0.wireOp",EDGE,"E134"),sQuery(id+"F0.wireOp",EDGE,"E135"),sQuery(id+"F0.wireOp",EDGE,"E136"),sQuery(id+"F0.wireOp",EDGE,"E137"),sQuery(id+"F0.wireOp",EDGE,"E138"),sQuery(id+"F0.wireOp",EDGE,"E139"),sQuery(id+"F0.wireOp",EDGE,"E140"),sQuery(id+"F0.wireOp",EDGE,"E141"),sQuery(id+"F0.wireOp",EDGE,"E142"),sQuery(id+"F0.wireOp",EDGE,"E143"),sQuery(id+"F0.wireOp",EDGE,"E144"),sQuery(id+"F0.wireOp",EDGE,"E145"),sQuery(id+"F0.wireOp",EDGE,"E146"),sQuery(id+"F0.wireOp",EDGE,"E147"),sQuery(id+"F0.wireOp",EDGE,"E148"),sQuery(id+"F0.wireOp",EDGE,"E149"),sQuery(id+"F0.wireOp",EDGE,"E150"),sQuery(id+"F0.wireOp",EDGE,"E151"),sQuery(id+"F0.wireOp",EDGE,"E152"),sQuery(id+"F0.wireOp",EDGE,"E153"),sQuery(id+"F0.wireOp",EDGE,"E154"),sQuery(id+"F0.wireOp",EDGE,"E155"),sQuery(id+"F0.wireOp",EDGE,"E156"),sQuery(id+"F0.wireOp",EDGE,"E157"),sQuery(id+"F0.wireOp",EDGE,"E158"),sQuery(id+"F0.wireOp",EDGE,"E159"),sQuery(id+"F0.wireOp",EDGE,"E160"),sQuery(id+"F0.wireOp",EDGE,"E161"),sQuery(id+"F0.wireOp",EDGE,"E162"),sQuery(id+"F0.wireOp",EDGE,"E163"),sQuery(id+"F0.wireOp",EDGE,"E164"),sQuery(id+"F0.wireOp",EDGE,"E165"),sQuery(id+"F0.wireOp",EDGE,"E166"),sQuery(id+"F0.wireOp",EDGE,"E167"),sQuery(id+"F0.wireOp",EDGE,"E168"),sQuery(id+"F0.wireOp",EDGE,"E169"),sQuery(id+"F0.wireOp",EDGE,"E170"),sQuery(id+"F0.wireOp",EDGE,"E171"),sQuery(id+"F0.wireOp",EDGE,"E172"),sQuery(id+"F0.wireOp",EDGE,"E173"),sQuery(id+"F0.wireOp",EDGE,"E174"),sQuery(id+"F0.wireOp",EDGE,"E175"),sQuery(id+"F0.wireOp",EDGE,"E176"),sQuery(id+"F0.wireOp",EDGE,"E177"),sQuery(id+"F0.wireOp",EDGE,"E178"),sQuery(id+"F0.wireOp",EDGE,"E179"),sQuery(id+"F0.wireOp",EDGE,"E180"),sQuery(id+"F0.wireOp",EDGE,"E181"),sQuery(id+"F0.wireOp",EDGE,"E182"),sQuery(id+"F0.wireOp",EDGE,"E183"),sQuery(id+"F0.wireOp",EDGE,"E184"),sQuery(id+"F0.wireOp",EDGE,"E185"),sQuery(id+"F0.wireOp",EDGE,"E186"),sQuery(id+"F0.wireOp",EDGE,"E187"),sQuery(id+"F0.wireOp",EDGE,"E188"),sQuery(id+"F0.wireOp",EDGE,"E189"),sQuery(id+"F0.wireOp",EDGE,"E190"),sQuery(id+"F0.wireOp",EDGE,"E191"),sQuery(id+"F0.wireOp",EDGE,"E192"),sQuery(id+"F0.wireOp",EDGE,"E193"),sQuery(id+"F0.wireOp",EDGE,"E194"),sQuery(id+"F0.wireOp",EDGE,"E195"),sQuery(id+"F0.wireOp",EDGE,"E196"),sQuery(id+"F0.wireOp",EDGE,"E197"),sQuery(id+"F0.wireOp",EDGE,"E198"),sQuery(id+"F0.wireOp",EDGE,"E199"),sQuery(id+"F0.wireOp",EDGE,"E200"),sQuery(id+"F0.wireOp",EDGE,"E201"),sQuery(id+"F0.wireOp",EDGE,"E202"),sQuery(id+"F0.wireOp",EDGE,"E203"),sQuery(id+"F0.wireOp",EDGE,"E204"),sQuery(id+"F0.wireOp",EDGE,"E205"),sQuery(id+"F0.wireOp",EDGE,"E206"),sQuery(id+"F0.wireOp",EDGE,"E207"),sQuery(id+"F0.wireOp",EDGE,"E208"),sQuery(id+"F0.wireOp",EDGE,"E209"),sQuery(id+"F0.wireOp",EDGE,"E210"),sQuery(id+"F0.wireOp",EDGE,"E211"),sQuery(id+"F0.wireOp",EDGE,"E212"),sQuery(id+"F0.wireOp",EDGE,"E213"),sQuery(id+"F0.wireOp",EDGE,"E214"),sQuery(id+"F0.wireOp",EDGE,"E215"),sQuery(id+"F0.wireOp",EDGE,"E216"),sQuery(id+"F0.wireOp",EDGE,"E217"),sQuery(id+"F0.wireOp",EDGE,"E218"),sQuery(id+"F0.wireOp",EDGE,"E219"),sQuery(id+"F0.wireOp",EDGE,"E220"),sQuery(id+"F0.wireOp",EDGE,"E221"),sQuery(id+"F0.wireOp",EDGE,"E222"),sQuery(id+"F0.wireOp",EDGE,"E223"),sQuery(id+"F0.wireOp",EDGE,"E224"),sQuery(id+"F0.wireOp",EDGE,"E225"),sQuery(id+"F0.wireOp",EDGE,"E226"),sQuery(id+"F0.wireOp",EDGE,"E227"),sQuery(id+"F0.wireOp",EDGE,"E228"),sQuery(id+"F0.wireOp",EDGE,"E229"),sQuery(id+"F0.wireOp",EDGE,"E230"),sQuery(id+"F0.wireOp",EDGE,"E231"),sQuery(id+"F0.wireOp",EDGE,"E232"),sQuery(id+"F0.wireOp",EDGE,"E233"),sQuery(id+"F0.wireOp",EDGE,"E234"),sQuery(id+"F0.wireOp",EDGE,"E235"),sQuery(id+"F0.wireOp",EDGE,"E236"),sQuery(id+"F0.wireOp",EDGE,"E237"),sQuery(id+"F0.wireOp",EDGE,"E238"),sQuery(id+"F0.wireOp",EDGE,"E239"),sQuery(id+"F0.wireOp",EDGE,"E240"),sQuery(id+"F0.wireOp",EDGE,"E241"),sQuery(id+"F0.wireOp",EDGE,"E242"),sQuery(id+"F0.wireOp",EDGE,"E243"),sQuery(id+"F0.wireOp",EDGE,"E244"),sQuery(id+"F0.wireOp",EDGE,"E245"),sQuery(id+"F0.wireOp",EDGE,"E246"),sQuery(id+"F0.wireOp",EDGE,"E247"),sQuery(id+"F0.wireOp",EDGE,"E248"),sQuery(id+"F0.wireOp",EDGE,"E249"),sQuery(id+"F0.wireOp",EDGE,"E250"),sQuery(id+"F0.wireOp",EDGE,"E251"),sQuery(id+"F0.wireOp",EDGE,"E252"),sQuery(id+"F0.wireOp",EDGE,"E253"),sQuery(id+"F0.wireOp",EDGE,"E254"),sQuery(id+"F0.wireOp",EDGE,"E255"),sQuery(id+"F0.wireOp",EDGE,"E256"),sQuery(id+"F0.wireOp",EDGE,"E257"),sQuery(id+"F0.wireOp",EDGE,"E258"),sQuery(id+"F0.wireOp",EDGE,"E259"),sQuery(id+"F0.wireOp",EDGE,"E260"),sQuery(id+"F0.wireOp",EDGE,"E261"),sQuery(id+"F0.wireOp",EDGE,"E262"),sQuery(id+"F0.wireOp",EDGE,"E263"),sQuery(id+"F0.wireOp",EDGE,"E264"),sQuery(id+"F0.wireOp",EDGE,"E265"),sQuery(id+"F0.wireOp",EDGE,"E266"),sQuery(id+"F0.wireOp",EDGE,"E267"),sQuery(id+"F0.wireOp",EDGE,"E268"),sQuery(id+"F0.wireOp",EDGE,"E269"),sQuery(id+"F0.wireOp",EDGE,"E270"),sQuery(id+"F0.wireOp",EDGE,"E271"),sQuery(id+"F0.wireOp",EDGE,"E272"),sQuery(id+"F0.wireOp",EDGE,"E273"),sQuery(id+"F0.wireOp",EDGE,"E274"),sQuery(id+"F0.wireOp",EDGE,"E275"),sQuery(id+"F0.wireOp",EDGE,"E276"),sQuery(id+"F0.wireOp",EDGE,"E277"),sQuery(id+"F0.wireOp",EDGE,"E278"),sQuery(id+"F0.wireOp",EDGE,"E279"),sQuery(id+"F0.wireOp",EDGE,"E280"),sQuery(id+"F0.wireOp",EDGE,"E281"),sQuery(id+"F0.wireOp",EDGE,"E282"),sQuery(id+"F0.wireOp",EDGE,"E283"),sQuery(id+"F0.wireOp",EDGE,"E284"),sQuery(id+"F0.wireOp",EDGE,"E285"),sQuery(id+"F0.wireOp",EDGE,"E286"),sQuery(id+"F0.wireOp",EDGE,"E287"),sQuery(id+"F0.wireOp",EDGE,"E288"),sQuery(id+"F0.wireOp",EDGE,"E289"),sQuery(id+"F0.wireOp",EDGE,"E290"),sQuery(id+"F0.wireOp",EDGE,"E291"),sQuery(id+"F0.wireOp",EDGE,"E292"),sQuery(id+"F0.wireOp",EDGE,"E293"),sQuery(id+"F0.wireOp",EDGE,"E294"),sQuery(id+"F0.wireOp",EDGE,"E295"),sQuery(id+"F0.wireOp",EDGE,"E296"),sQuery(id+"F0.wireOp",EDGE,"E297"),sQuery(id+"F0.wireOp",EDGE,"E298"),sQuery(id+"F0.wireOp",EDGE,"E299"),sQuery(id+"F0.wireOp",EDGE,"E300"),sQuery(id+"F0.wireOp",EDGE,"E301"),sQuery(id+"F0.wireOp",EDGE,"E302"),sQuery(id+"F0.wireOp",EDGE,"E303"),sQuery(id+"F0.wireOp",EDGE,"E304"),sQuery(id+"F0.wireOp",EDGE,"E305"),sQuery(id+"F0.wireOp",EDGE,"E306"),sQuery(id+"F0.wireOp",EDGE,"E307"),sQuery(id+"F0.wireOp",EDGE,"E308"),sQuery(id+"F0.wireOp",EDGE,"E309"),sQuery(id+"F0.wireOp",EDGE,"E310"),sQuery(id+"F0.wireOp",EDGE,"E311"),sQuery(id+"F0.wireOp",EDGE,"E312"),sQuery(id+"F0.wireOp",EDGE,"E313"),sQuery(id+"F0.wireOp",EDGE,"E314"),sQuery(id+"F0.wireOp",EDGE,"E315"),sQuery(id+"F0.wireOp",EDGE,"E316"),sQuery(id+"F0.wireOp",EDGE,"E317"),sQuery(id+"F0.wireOp",EDGE,"E318"),sQuery(id+"F0.wireOp",EDGE,"E319"),sQuery(id+"F0.wireOp",EDGE,"E320"),sQuery(id+"F0.wireOp",EDGE,"E321"),sQuery(id+"F0.wireOp",EDGE,"E322"),sQuery(id+"F0.wireOp",EDGE,"E323"),sQuery(id+"F0.wireOp",EDGE,"E324"),sQuery(id+"F0.wireOp",EDGE,"E325"),sQuery(id+"F0.wireOp",EDGE,"E326"),sQuery(id+"F0.wireOp",EDGE,"E327"),sQuery(id+"F0.wireOp",EDGE,"E328"),sQuery(id+"F0.wireOp",EDGE,"E329"),sQuery(id+"F0.wireOp",EDGE,"E330"),sQuery(id+"F0.wireOp",EDGE,"E331"),sQuery(id+"F0.wireOp",EDGE,"E332"),sQuery(id+"F0.wireOp",EDGE,"E333"),sQuery(id+"F0.wireOp",EDGE,"E334"),sQuery(id+"F0.wireOp",EDGE,"E335"),sQuery(id+"F0.wireOp",EDGE,"E336"),sQuery(id+"F0.wireOp",EDGE,"E337"),sQuery(id+"F0.wireOp",EDGE,"E338"),sQuery(id+"F0.wireOp",EDGE,"E339"),sQuery(id+"F0.wireOp",EDGE,"E340"),sQuery(id+"F0.wireOp",EDGE,"E341"),sQuery(id+"F0.wireOp",EDGE,"E342"),sQuery(id+"F0.wireOp",EDGE,"E343"),sQuery(id+"F0.wireOp",EDGE,"E344"),sQuery(id+"F0.wireOp",EDGE,"E345"),sQuery(id+"F0.wireOp",EDGE,"E346"),sQuery(id+"F0.wireOp",EDGE,"E347"),sQuery(id+"F0.wireOp",EDGE,"E348"),sQuery(id+"F0.wireOp",EDGE,"E349"),sQuery(id+"F0.wireOp",EDGE,"E350"),sQuery(id+"F0.wireOp",EDGE,"E351"),sQuery(id+"F0.wireOp",EDGE,"E352"),sQuery(id+"F0.wireOp",EDGE,"E353"),sQuery(id+"F0.wireOp",EDGE,"E354"),sQuery(id+"F0.wireOp",EDGE,"E355"),sQuery(id+"F0.wireOp",EDGE,"E356"),sQuery(id+"F0.wireOp",EDGE,"E357"),sQuery(id+"F0.wireOp",EDGE,"E358"),sQuery(id+"F0.wireOp",EDGE,"E359"),sQuery(id+"F0.wireOp",EDGE,"E360"),sQuery(id+"F0.wireOp",EDGE,"E361"),sQuery(id+"F0.wireOp",EDGE,"E362"),sQuery(id+"F0.wireOp",EDGE,"E363"),sQuery(id+"F0.wireOp",EDGE,"E364"),sQuery(id+"F0.wireOp",EDGE,"E365"),sQuery(id+"F0.wireOp",EDGE,"E366"),sQuery(id+"F0.wireOp",EDGE,"E367"),sQuery(id+"F0.wireOp",EDGE,"E368"),sQuery(id+"F0.wireOp",EDGE,"E369"),sQuery(id+"F0.wireOp",EDGE,"E370"),sQuery(id+"F0.wireOp",EDGE,"E371"),sQuery(id+"F0.wireOp",EDGE,"E372"),sQuery(id+"F0.wireOp",EDGE,"E373"),sQuery(id+"F0.wireOp",EDGE,"E374"),sQuery(id+"F0.wireOp",EDGE,"E375"),sQuery(id+"F0.wireOp",EDGE,"E376"),sQuery(id+"F0.wireOp",EDGE,"E377"),sQuery(id+"F0.wireOp",EDGE,"E378"),sQuery(id+"F0.wireOp",EDGE,"E379"),sQuery(id+"F0.wireOp",EDGE,"E380"),sQuery(id+"F0.wireOp",EDGE,"E381"),sQuery(id+"F0.wireOp",EDGE,"E382"),sQuery(id+"F0.wireOp",EDGE,"E383"),sQuery(id+"F0.wireOp",EDGE,"E384"),sQuery(id+"F0.wireOp",EDGE,"E385"),sQuery(id+"F0.wireOp",EDGE,"E386"),sQuery(id+"F0.wireOp",EDGE,"E387"),sQuery(id+"F0.wireOp",EDGE,"E388"),sQuery(id+"F0.wireOp",EDGE,"E389"),sQuery(id+"F0.wireOp",EDGE,"E390"),sQuery(id+"F0.wireOp",EDGE,"E391"),sQuery(id+"F0.wireOp",EDGE,"E392"),sQuery(id+"F0.wireOp",EDGE,"E393"),sQuery(id+"F0.wireOp",EDGE,"E394"),sQuery(id+"F0.wireOp",EDGE,"E395"),sQuery(id+"F0.wireOp",EDGE,"E396"),sQuery(id+"F0.wireOp",EDGE,"E397"),sQuery(id+"F0.wireOp",EDGE,"E398"),sQuery(id+"F0.wireOp",EDGE,"E399"),sQuery(id+"F0.wireOp",EDGE,"E400"),sQuery(id+"F0.wireOp",EDGE,"E401"),sQuery(id+"F0.wireOp",EDGE,"E402"),sQuery(id+"F0.wireOp",EDGE,"E403"),sQuery(id+"F0.wireOp",EDGE,"E404"),sQuery(id+"F0.wireOp",EDGE,"E405"),sQuery(id+"F0.wireOp",EDGE,"E406"),sQuery(id+"F0.wireOp",EDGE,"E407"),sQuery(id+"F0.wireOp",EDGE,"E408"),sQuery(id+"F0.wireOp",EDGE,"E409"),sQuery(id+"F0.wireOp",EDGE,"E410"),sQuery(id+"F0.wireOp",EDGE,"E411"),sQuery(id+"F0.wireOp",EDGE,"E412"),sQuery(id+"F0.wireOp",EDGE,"E413"),sQuery(id+"F0.wireOp",EDGE,"E414"),sQuery(id+"F0.wireOp",EDGE,"E415"),sQuery(id+"F0.wireOp",EDGE,"E416"),sQuery(id+"F0.wireOp",EDGE,"E417"),sQuery(id+"F0.wireOp",EDGE,"E418"),sQuery(id+"F0.wireOp",EDGE,"E419"),sQuery(id+"F0.wireOp",EDGE,"E420"),sQuery(id+"F0.wireOp",EDGE,"E421"),sQuery(id+"F0.wireOp",EDGE,"E422"),sQuery(id+"F0.wireOp",EDGE,"E423"),sQuery(id+"F0.wireOp",EDGE,"E424"),sQuery(id+"F0.wireOp",EDGE,"E425"),sQuery(id+"F0.wireOp",EDGE,"E426"),sQuery(id+"F0.wireOp",EDGE,"E427"),sQuery(id+"F0.wireOp",EDGE,"E428"),sQuery(id+"F0.wireOp",EDGE,"E429"),sQuery(id+"F0.wireOp",EDGE,"E430"),sQuery(id+"F0.wireOp",EDGE,"E431"),sQuery(id+"F0.wireOp",EDGE,"E432"),sQuery(id+"F0.wireOp",EDGE,"E433"),sQuery(id+"F0.wireOp",EDGE,"E434"),sQuery(id+"F0.wireOp",EDGE,"E435"),sQuery(id+"F0.wireOp",EDGE,"E436"),sQuery(id+"F0.wireOp",EDGE,"E437"),sQuery(id+"F0.wireOp",EDGE,"E438"),sQuery(id+"F0.wireOp",EDGE,"E439"),sQuery(id+"F0.wireOp",EDGE,"E440"),sQuery(id+"F0.wireOp",EDGE,"E441"),sQuery(id+"F0.wireOp",EDGE,"E442"),sQuery(id+"F0.wireOp",EDGE,"E443"),sQuery(id+"F0.wireOp",EDGE,"E444"),sQuery(id+"F0.wireOp",EDGE,"E445"),sQuery(id+"F0.wireOp",EDGE,"E446"),sQuery(id+"F0.wireOp",EDGE,"E447"),sQuery(id+"F0.wireOp",EDGE,"E448"),sQuery(id+"F0.wireOp",EDGE,"E449"),sQuery(id+"F0.wireOp",EDGE,"E450"),sQuery(id+"F0.wireOp",EDGE,"E451"),sQuery(id+"F0.wireOp",EDGE,"E452"),sQuery(id+"F0.wireOp",EDGE,"E453"),sQuery(id+"F0.wireOp",EDGE,"E454"),sQuery(id+"F0.wireOp",EDGE,"E455"),sQuery(id+"F0.wireOp",EDGE,"E456"),sQuery(id+"F0.wireOp",EDGE,"E457"),sQuery(id+"F0.wireOp",EDGE,"E458"),sQuery(id+"F0.wireOp",EDGE,"E459"),sQuery(id+"F0.wireOp",EDGE,"E460"),sQuery(id+"F0.wireOp",EDGE,"E461"),sQuery(id+"F0.wireOp",EDGE,"E462"),sQuery(id+"F0.wireOp",EDGE,"E463"),sQuery(id+"F0.wireOp",EDGE,"E464"),sQuery(id+"F0.wireOp",EDGE,"E465"),sQuery(id+"F0.wireOp",EDGE,"E466"),sQuery(id+"F0.wireOp",EDGE,"E467"),sQuery(id+"F0.wireOp",EDGE,"E468"),sQuery(id+"F0.wireOp",EDGE,"E469"),sQuery(id+"F0.wireOp",EDGE,"E470"),sQuery(id+"F0.wireOp",EDGE,"E471"),sQuery(id+"F0.wireOp",EDGE,"E472"),sQuery(id+"F0.wireOp",EDGE,"E473"),sQuery(id+"F0.wireOp",EDGE,"E474"),sQuery(id+"F0.wireOp",EDGE,"E475"),sQuery(id+"F0.wireOp",EDGE,"E476"),sQuery(id+"F0.wireOp",EDGE,"E477"),sQuery(id+"F0.wireOp",EDGE,"E478"),sQuery(id+"F0.wireOp",EDGE,"E479"),sQuery(id+"F0.wireOp",EDGE,"E480"),sQuery(id+"F0.wireOp",EDGE,"E481"),sQuery(id+"F0.wireOp",EDGE,"E482"),sQuery(id+"F0.wireOp",EDGE,"E483"),sQuery(id+"F0.wireOp",EDGE,"E484"),sQuery(id+"F0.wireOp",EDGE,"E485"),sQuery(id+"F0.wireOp",EDGE,"E486"),sQuery(id+"F0.wireOp",EDGE,"E487"),sQuery(id+"F0.wireOp",EDGE,"E488"),sQuery(id+"F0.wireOp",EDGE,"E489"),sQuery(id+"F0.wireOp",EDGE,"E490"),sQuery(id+"F0.wireOp",EDGE,"E491"),sQuery(id+"F0.wireOp",EDGE,"E492"),sQuery(id+"F0.wireOp",EDGE,"E493"),sQuery(id+"F0.wireOp",EDGE,"E494"),sQuery(id+"F0.wireOp",EDGE,"E495"),sQuery(id+"F0.wireOp",EDGE,"E496"),sQuery(id+"F0.wireOp",EDGE,"E497"),sQuery(id+"F0.wireOp",EDGE,"E498"),sQuery(id+"F0.wireOp",EDGE,"E499"),sQuery(id+"F0.wireOp",EDGE,"E500"),sQuery(id+"F0.wireOp",EDGE,"E501"),sQuery(id+"F0.wireOp",EDGE,"E502"),sQuery(id+"F0.wireOp",EDGE,"E503"),sQuery(id+"F0.wireOp",EDGE,"E504"),sQuery(id+"F0.wireOp",EDGE,"E505"),sQuery(id+"F0.wireOp",EDGE,"E506"),sQuery(id+"F0.wireOp",EDGE,"E507"),sQuery(id+"F0.wireOp",EDGE,"E508"),sQuery(id+"F0.wireOp",EDGE,"E509"),sQuery(id+"F0.wireOp",EDGE,"E510"),sQuery(id+"F0.wireOp",EDGE,"E511"),sQuery(id+"F0.wireOp",EDGE,"E512"),sQuery(id+"F0.wireOp",EDGE,"E513"),sQuery(id+"F0.wireOp",EDGE,"E514"),sQuery(id+"F0.wireOp",EDGE,"E515"),sQuery(id+"F0.wireOp",EDGE,"E516"),sQuery(id+"F0.wireOp",EDGE,"E517"),sQuery(id+"F0.wireOp",EDGE,"E518"),sQuery(id+"F0.wireOp",EDGE,"E519"),sQuery(id+"F0.wireOp",EDGE,"E520"),sQuery(id+"F0.wireOp",EDGE,"E521"),sQuery(id+"F0.wireOp",EDGE,"E522"),sQuery(id+"F0.wireOp",EDGE,"E523"),sQuery(id+"F0.wireOp",EDGE,"E524"),sQuery(id+"F0.wireOp",EDGE,"E525"),sQuery(id+"F0.wireOp",EDGE,"E526"),sQuery(id+"F0.wireOp",EDGE,"E527"),sQuery(id+"F0.wireOp",EDGE,"E528"),sQuery(id+"F0.wireOp",EDGE,"E529"),sQuery(id+"F0.wireOp",EDGE,"E530"),sQuery(id+"F0.wireOp",EDGE,"E531"),sQuery(id+"F0.wireOp",EDGE,"E532"),sQuery(id+"F0.wireOp",EDGE,"E533"),sQuery(id+"F0.wireOp",EDGE,"E534"),sQuery(id+"F0.wireOp",EDGE,"E535"),sQuery(id+"F0.wireOp",EDGE,"E536"),sQuery(id+"F0.wireOp",EDGE,"E537"),sQuery(id+"F0.wireOp",EDGE,"E538"),sQuery(id+"F0.wireOp",EDGE,"E539"),sQuery(id+"F0.wireOp",EDGE,"E540"),sQuery(id+"F0.wireOp",EDGE,"E541"),sQuery(id+"F0.wireOp",EDGE,"E542"),sQuery(id+"F0.wireOp",EDGE,"E543"),sQuery(id+"F0.wireOp",EDGE,"E544"),sQuery(id+"F0.wireOp",EDGE,"E545"),sQuery(id+"F0.wireOp",EDGE,"E546"),sQuery(id+"F0.wireOp",EDGE,"E547"),sQuery(id+"F0.wireOp",EDGE,"E548"),sQuery(id+"F0.wireOp",EDGE,"E549"),sQuery(id+"F0.wireOp",EDGE,"E550"),sQuery(id+"F0.wireOp",EDGE,"E551"),sQuery(id+"F0.wireOp",EDGE,"E552"),sQuery(id+"F0.wireOp",EDGE,"E553"),sQuery(id+"F0.wireOp",EDGE,"E554"),sQuery(id+"F0.wireOp",EDGE,"E555"),sQuery(id+"F0.wireOp",EDGE,"E556"),sQuery(id+"F0.wireOp",EDGE,"E557"),sQuery(id+"F0.wireOp",EDGE,"E558"),sQuery(id+"F0.wireOp",EDGE,"E559"),sQuery(id+"F0.wireOp",EDGE,"E560"),sQuery(id+"F0.wireOp",EDGE,"E561"),sQuery(id+"F0.wireOp",EDGE,"E562"),sQuery(id+"F0.wireOp",EDGE,"E563"),sQuery(id+"F0.wireOp",EDGE,"E564"),sQuery(id+"F0.wireOp",EDGE,"E565"),sQuery(id+"F0.wireOp",EDGE,"E566"),sQuery(id+"F0.wireOp",EDGE,"E567"),sQuery(id+"F0.wireOp",EDGE,"E568"),sQuery(id+"F0.wireOp",EDGE,"E569"),sQuery(id+"F0.wireOp",EDGE,"E570"),sQuery(id+"F0.wireOp",EDGE,"E571"),sQuery(id+"F0.wireOp",EDGE,"E572"),sQuery(id+"F0.wireOp",EDGE,"E573"),sQuery(id+"F0.wireOp",EDGE,"E574"),sQuery(id+"F0.wireOp",EDGE,"E575"),sQuery(id+"F0.wireOp",EDGE,"E576"),sQuery(id+"F0.wireOp",EDGE,"E577"),sQuery(id+"F0.wireOp",EDGE,"E578"),sQuery(id+"F0.wireOp",EDGE,"E579"),sQuery(id+"F0.wireOp",EDGE,"E580"),sQuery(id+"F0.wireOp",EDGE,"E581"),sQuery(id+"F0.wireOp",EDGE,"E582"),sQuery(id+"F0.wireOp",EDGE,"E583"),sQuery(id+"F0.wireOp",EDGE,"E584"),sQuery(id+"F0.wireOp",EDGE,"E585"),sQuery(id+"F0.wireOp",EDGE,"E586"),sQuery(id+"F0.wireOp",EDGE,"E587"),sQuery(id+"F0.wireOp",EDGE,"E588"),sQuery(id+"F0.wireOp",EDGE,"E589"),sQuery(id+"F0.wireOp",EDGE,"E590"),sQuery(id+"F0.wireOp",EDGE,"E591"),sQuery(id+"F0.wireOp",EDGE,"E592"),sQuery(id+"F0.wireOp",EDGE,"E593"),sQuery(id+"F0.wireOp",EDGE,"E594"),sQuery(id+"F0.wireOp",EDGE,"E595"),sQuery(id+"F0.wireOp",EDGE,"E596"),sQuery(id+"F0.wireOp",EDGE,"E597"),sQuery(id+"F0.wireOp",EDGE,"E598"),sQuery(id+"F0.wireOp",EDGE,"E599"),sQuery(id+"F0.wireOp",EDGE,"E600"),sQuery(id+"F0.wireOp",EDGE,"E601"),sQuery(id+"F0.wireOp",EDGE,"E602"),sQuery(id+"F0.wireOp",EDGE,"E603"),sQuery(id+"F0.wireOp",EDGE,"E604"),sQuery(id+"F0.wireOp",EDGE,"E605"),sQuery(id+"F0.wireOp",EDGE,"E606"),sQuery(id+"F0.wireOp",EDGE,"E607"),sQuery(id+"F0.wireOp",EDGE,"E608"),sQuery(id+"F0.wireOp",EDGE,"E609"),sQuery(id+"F0.wireOp",EDGE,"E610"),sQuery(id+"F0.wireOp",EDGE,"E611"),sQuery(id+"F0.wireOp",EDGE,"E612"),sQuery(id+"F0.wireOp",EDGE,"E613"),sQuery(id+"F0.wireOp",EDGE,"E614"),sQuery(id+"F0.wireOp",EDGE,"E615"),sQuery(id+"F0.wireOp",EDGE,"E616"),sQuery(id+"F0.wireOp",EDGE,"E617"),sQuery(id+"F0.wireOp",EDGE,"E618"),sQuery(id+"F0.wireOp",EDGE,"E619"),sQuery(id+"F0.wireOp",EDGE,"E620"),sQuery(id+"F0.wireOp",EDGE,"E621"),sQuery(id+"F0.wireOp",EDGE,"E622"),sQuery(id+"F0.wireOp",EDGE,"E623"),sQuery(id+"F0.wireOp",EDGE,"E624"),sQuery(id+"F0.wireOp",EDGE,"E625"),sQuery(id+"F0.wireOp",EDGE,"E626"),sQuery(id+"F0.wireOp",EDGE,"E627"),sQuery(id+"F0.wireOp",EDGE,"E628"),sQuery(id+"F0.wireOp",EDGE,"E629"),sQuery(id+"F0.wireOp",EDGE,"E630"),sQuery(id+"F0.wireOp",EDGE,"E631"),sQuery(id+"F0.wireOp",EDGE,"E632"),sQuery(id+"F0.wireOp",EDGE,"E633"),sQuery(id+"F0.wireOp",EDGE,"E634"),sQuery(id+"F0.wireOp",EDGE,"E635"),sQuery(id+"F0.wireOp",EDGE,"E636"),sQuery(id+"F0.wireOp",EDGE,"E637"),sQuery(id+"F0.wireOp",EDGE,"E638"),sQuery(id+"F0.wireOp",EDGE,"E639"),sQuery(id+"F0.wireOp",EDGE,"E640"),sQuery(id+"F0.wireOp",EDGE,"E641"),sQuery(id+"F0.wireOp",EDGE,"E642"),sQuery(id+"F0.wireOp",EDGE,"E643"),sQuery(id+"F0.wireOp",EDGE,"E644"),sQuery(id+"F0.wireOp",EDGE,"E645"),sQuery(id+"F0.wireOp",EDGE,"E646"),sQuery(id+"F0.wireOp",EDGE,"E647"),sQuery(id+"F0.wireOp",EDGE,"E648"),sQuery(id+"F0.wireOp",EDGE,"E649"),sQuery(id+"F0.wireOp",EDGE,"E650"),sQuery(id+"F0.wireOp",EDGE,"E651"),sQuery(id+"F0.wireOp",EDGE,"E652"),sQuery(id+"F0.wireOp",EDGE,"E653"),sQuery(id+"F0.wireOp",EDGE,"E654"),sQuery(id+"F0.wireOp",EDGE,"E655"),sQuery(id+"F0.wireOp",EDGE,"E656"),sQuery(id+"F0.wireOp",EDGE,"E657"),sQuery(id+"F0.wireOp",EDGE,"E658"),sQuery(id+"F0.wireOp",EDGE,"E659"),sQuery(id+"F0.wireOp",EDGE,"E660"),sQuery(id+"F0.wireOp",EDGE,"E661"),sQuery(id+"F0.wireOp",EDGE,"E662"),sQuery(id+"F0.wireOp",EDGE,"E663"),sQuery(id+"F0.wireOp",EDGE,"E664"),sQuery(id+"F0.wireOp",EDGE,"E665"),sQuery(id+"F0.wireOp",EDGE,"E666"),sQuery(id+"F0.wireOp",EDGE,"E667"),sQuery(id+"F0.wireOp",EDGE,"E668"),sQuery(id+"F0.wireOp",EDGE,"E669"),sQuery(id+"F0.wireOp",EDGE,"E670"),sQuery(id+"F0.wireOp",EDGE,"E671"),sQuery(id+"F0.wireOp",EDGE,"E672"),sQuery(id+"F0.wireOp",EDGE,"E673"),sQuery(id+"F0.wireOp",EDGE,"E674"),sQuery(id+"F0.wireOp",EDGE,"E675"),sQuery(id+"F0.wireOp",EDGE,"E676"),sQuery(id+"F0.wireOp",EDGE,"E677"),sQuery(id+"F0.wireOp",EDGE,"E678"),sQuery(id+"F0.wireOp",EDGE,"E679"),sQuery(id+"F0.wireOp",EDGE,"E680"),sQuery(id+"F0.wireOp",EDGE,"E681"),sQuery(id+"F0.wireOp",EDGE,"E682"),sQuery(id+"F0.wireOp",EDGE,"E683"),sQuery(id+"F0.wireOp",EDGE,"E684"),sQuery(id+"F0.wireOp",EDGE,"E685"),sQuery(id+"F0.wireOp",EDGE,"E686"),sQuery(id+"F0.wireOp",EDGE,"E687"),sQuery(id+"F0.wireOp",EDGE,"E688"),sQuery(id+"F0.wireOp",EDGE,"E689"),sQuery(id+"F0.wireOp",EDGE,"E690"),sQuery(id+"F0.wireOp",EDGE,"E691"),sQuery(id+"F0.wireOp",EDGE,"E692"),sQuery(id+"F0.wireOp",EDGE,"E693"),sQuery(id+"F0.wireOp",EDGE,"E694"),sQuery(id+"F0.wireOp",EDGE,"E695"),sQuery(id+"F0.wireOp",EDGE,"E696"),sQuery(id+"F0.wireOp",EDGE,"E697"),sQuery(id+"F0.wireOp",EDGE,"E698"),sQuery(id+"F0.wireOp",EDGE,"E699"),sQuery(id+"F0.wireOp",EDGE,"E700"),sQuery(id+"F0.wireOp",EDGE,"E701"),sQuery(id+"F0.wireOp",EDGE,"E702"),sQuery(id+"F0.wireOp",EDGE,"E703"),sQuery(id+"F0.wireOp",EDGE,"E704"),sQuery(id+"F0.wireOp",EDGE,"E705"),sQuery(id+"F0.wireOp",EDGE,"E706"),sQuery(id+"F0.wireOp",EDGE,"E707"),sQuery(id+"F0.wireOp",EDGE,"E708"),sQuery(id+"F0.wireOp",EDGE,"E709"),sQuery(id+"F0.wireOp",EDGE,"E710"),sQuery(id+"F0.wireOp",EDGE,"E711"),sQuery(id+"F0.wireOp",EDGE,"E712"),sQuery(id+"F0.wireOp",EDGE,"E713"),sQuery(id+"F0.wireOp",EDGE,"E714"),sQuery(id+"F0.wireOp",EDGE,"E715"),sQuery(id+"F0.wireOp",EDGE,"E716"),sQuery(id+"F0.wireOp",EDGE,"E717"),sQuery(id+"F0.wireOp",EDGE,"E718"),sQuery(id+"F0.wireOp",EDGE,"E719"),sQuery(id+"F0.wireOp",EDGE,"E720"),sQuery(id+"F0.wireOp",EDGE,"E721"),sQuery(id+"F0.wireOp",EDGE,"E722"),sQuery(id+"F0.wireOp",EDGE,"E723"),sQuery(id+"F0.wireOp",EDGE,"E724"),sQuery(id+"F0.wireOp",EDGE,"E725"),sQuery(id+"F0.wireOp",EDGE,"E726"),sQuery(id+"F0.wireOp",EDGE,"E727"),sQuery(id+"F0.wireOp",EDGE,"E728"),sQuery(id+"F0.wireOp",EDGE,"E729"),sQuery(id+"F0.wireOp",EDGE,"E730"),sQuery(id+"F0.wireOp",EDGE,"E731"),sQuery(id+"F0.wireOp",EDGE,"E732"),sQuery(id+"F0.wireOp",EDGE,"E733"),sQuery(id+"F0.wireOp",EDGE,"E734"),sQuery(id+"F0.wireOp",EDGE,"E735"),sQuery(id+"F0.wireOp",EDGE,"E736"),sQuery(id+"F0.wireOp",EDGE,"E737"),sQuery(id+"F0.wireOp",EDGE,"E738"),sQuery(id+"F0.wireOp",EDGE,"E739"),sQuery(id+"F0.wireOp",EDGE,"E740"),sQuery(id+"F0.wireOp",EDGE,"E741"),sQuery(id+"F0.wireOp",EDGE,"E742"),sQuery(id+"F0.wireOp",EDGE,"E743"),sQuery(id+"F0.wireOp",EDGE,"E744"),sQuery(id+"F0.wireOp",EDGE,"E745"),sQuery(id+"F0.wireOp",EDGE,"E746"),sQuery(id+"F0.wireOp",EDGE,"E747"),sQuery(id+"F0.wireOp",EDGE,"E748"),sQuery(id+"F0.wireOp",EDGE,"E749"),sQuery(id+"F0.wireOp",EDGE,"E750"),sQuery(id+"F0.wireOp",EDGE,"E751"),sQuery(id+"F0.wireOp",EDGE,"E752"),sQuery(id+"F0.wireOp",EDGE,"E753"),sQuery(id+"F0.wireOp",EDGE,"E754"),sQuery(id+"F0.wireOp",EDGE,"E755"),sQuery(id+"F0.wireOp",EDGE,"E756"),sQuery(id+"F0.wireOp",EDGE,"E757"),sQuery(id+"F0.wireOp",EDGE,"E758"),sQuery(id+"F0.wireOp",EDGE,"E759"),sQuery(id+"F0.wireOp",EDGE,"E760"),sQuery(id+"F0.wireOp",EDGE,"E761"),sQuery(id+"F0.wireOp",EDGE,"E762"),sQuery(id+"F0.wireOp",EDGE,"E763"),sQuery(id+"F0.wireOp",EDGE,"E764"),sQuery(id+"F0.wireOp",EDGE,"E765"),sQuery(id+"F0.wireOp",EDGE,"E766"),sQuery(id+"F0.wireOp",EDGE,"E767"),sQuery(id+"F0.wireOp",EDGE,"E768"),sQuery(id+"F0.wireOp",EDGE,"E769"),sQuery(id+"F0.wireOp",EDGE,"E770"),sQuery(id+"F0.wireOp",EDGE,"E771"),sQuery(id+"F0.wireOp",EDGE,"E772"),sQuery(id+"F0.wireOp",EDGE,"E773"),sQuery(id+"F0.wireOp",EDGE,"E774"),sQuery(id+"F0.wireOp",EDGE,"E775"),sQuery(id+"F0.wireOp",EDGE,"E776"),sQuery(id+"F0.wireOp",EDGE,"E777"),sQuery(id+"F0.wireOp",EDGE,"E778"),sQuery(id+"F0.wireOp",EDGE,"E779"),sQuery(id+"F0.wireOp",EDGE,"E780"),sQuery(id+"F0.wireOp",EDGE,"E781"),sQuery(id+"F0.wireOp",EDGE,"E782"),sQuery(id+"F0.wireOp",EDGE,"E783"),sQuery(id+"F0.wireOp",EDGE,"E784"),sQuery(id+"F0.wireOp",EDGE,"E785"),sQuery(id+"F0.wireOp",EDGE,"E786"),sQuery(id+"F0.wireOp",EDGE,"E787"),sQuery(id+"F0.wireOp",EDGE,"E788"),sQuery(id+"F0.wireOp",EDGE,"E789"),sQuery(id+"F0.wireOp",EDGE,"E790"),sQuery(id+"F0.wireOp",EDGE,"E791"),sQuery(id+"F0.wireOp",EDGE,"E792"),sQuery(id+"F0.wireOp",EDGE,"E793"),sQuery(id+"F0.wireOp",EDGE,"E794"),sQuery(id+"F0.wireOp",EDGE,"E795"),sQuery(id+"F0.wireOp",EDGE,"E796"),sQuery(id+"F0.wireOp",EDGE,"E797"),sQuery(id+"F0.wireOp",EDGE,"E798"),sQuery(id+"F0.wireOp",EDGE,"E799"),sQuery(id+"F0.wireOp",EDGE,"E800"),sQuery(id+"F0.wireOp",EDGE,"E801"),sQuery(id+"F0.wireOp",EDGE,"E802"),sQuery(id+"F0.wireOp",EDGE,"E803"),sQuery(id+"F0.wireOp",EDGE,"E804"),sQuery(id+"F0.wireOp",EDGE,"E805"),sQuery(id+"F0.wireOp",EDGE,"E806"),sQuery(id+"F0.wireOp",EDGE,"E807"),sQuery(id+"F0.wireOp",EDGE,"E808"),sQuery(id+"F0.wireOp",EDGE,"E809"),sQuery(id+"F0.wireOp",EDGE,"E810"),sQuery(id+"F0.wireOp",EDGE,"E811"),sQuery(id+"F0.wireOp",EDGE,"E812"),sQuery(id+"F0.wireOp",EDGE,"E813"),sQuery(id+"F0.wireOp",EDGE,"E814"),sQuery(id+"F0.wireOp",EDGE,"E815"),sQuery(id+"F0.wireOp",EDGE,"E816"),sQuery(id+"F0.wireOp",EDGE,"E817"),sQuery(id+"F0.wireOp",EDGE,"E818"),sQuery(id+"F0.wireOp",EDGE,"E819"),sQuery(id+"F0.wireOp",EDGE,"E820"),sQuery(id+"F0.wireOp",EDGE,"E821"),sQuery(id+"F0.wireOp",EDGE,"E822"),sQuery(id+"F0.wireOp",EDGE,"E823"),sQuery(id+"F0.wireOp",EDGE,"E824"),sQuery(id+"F0.wireOp",EDGE,"E825"),sQuery(id+"F0.wireOp",EDGE,"E826"),sQuery(id+"F0.wireOp",EDGE,"E827"),sQuery(id+"F0.wireOp",EDGE,"E828"),sQuery(id+"F0.wireOp",EDGE,"E829"),sQuery(id+"F0.wireOp",EDGE,"E830"),sQuery(id+"F0.wireOp",EDGE,"E831"),sQuery(id+"F0.wireOp",EDGE,"E832"),sQuery(id+"F0.wireOp",EDGE,"E833"),sQuery(id+"F0.wireOp",EDGE,"E834"),sQuery(id+"F0.wireOp",EDGE,"E835"),sQuery(id+"F0.wireOp",EDGE,"E836"),sQuery(id+"F0.wireOp",EDGE,"E837"),sQuery(id+"F0.wireOp",EDGE,"E838"),sQuery(id+"F0.wireOp",EDGE,"E839")])],"isStart":false});
            var sketch = newSketch(context, id + "F4", { "sketchPlane" : qUnion([Q0])});
            skLineSegment(sketch, "E841", {"start": v(-179.6, -111.13) * mm, "end": v(215.6, -111.13) * mm, "construction": true});
            skCircle(sketch, "E842", {"center": v(0, 0) * mm, "radius": 199.23 * mm});
            skLineSegment(sketch, "E843", {"start": v(-165.36, -111.13) * mm, "end": v(165.36, -111.13) * mm});
            skSolve(sketch);
        }
        {
            var Q0;
            {var subQ5=makeQuery(id+"F1.opExtrude","CAP_EDGE",EDGE,{"disambiguationData":[OSD([sQuery(id+"F0.wireOp",EDGE,"E513")])],"isStart":false});Q0=makeQuery(id+"F4.imprint","IMPRINT",FACE,{"disambiguationData":[TD([[makeQuery(id+"F4.imprint","IMPRINT",EDGE,{"derivedFrom":subQ5}),-1.0]])]});}
            extrude(context, id + "F5", {"entities" : qUnion([Q0]), "operationType" : NewBodyOperationType.ADD, "oppositeDirection" : true, "depth" : 3.17 * mm});
        }
    });
